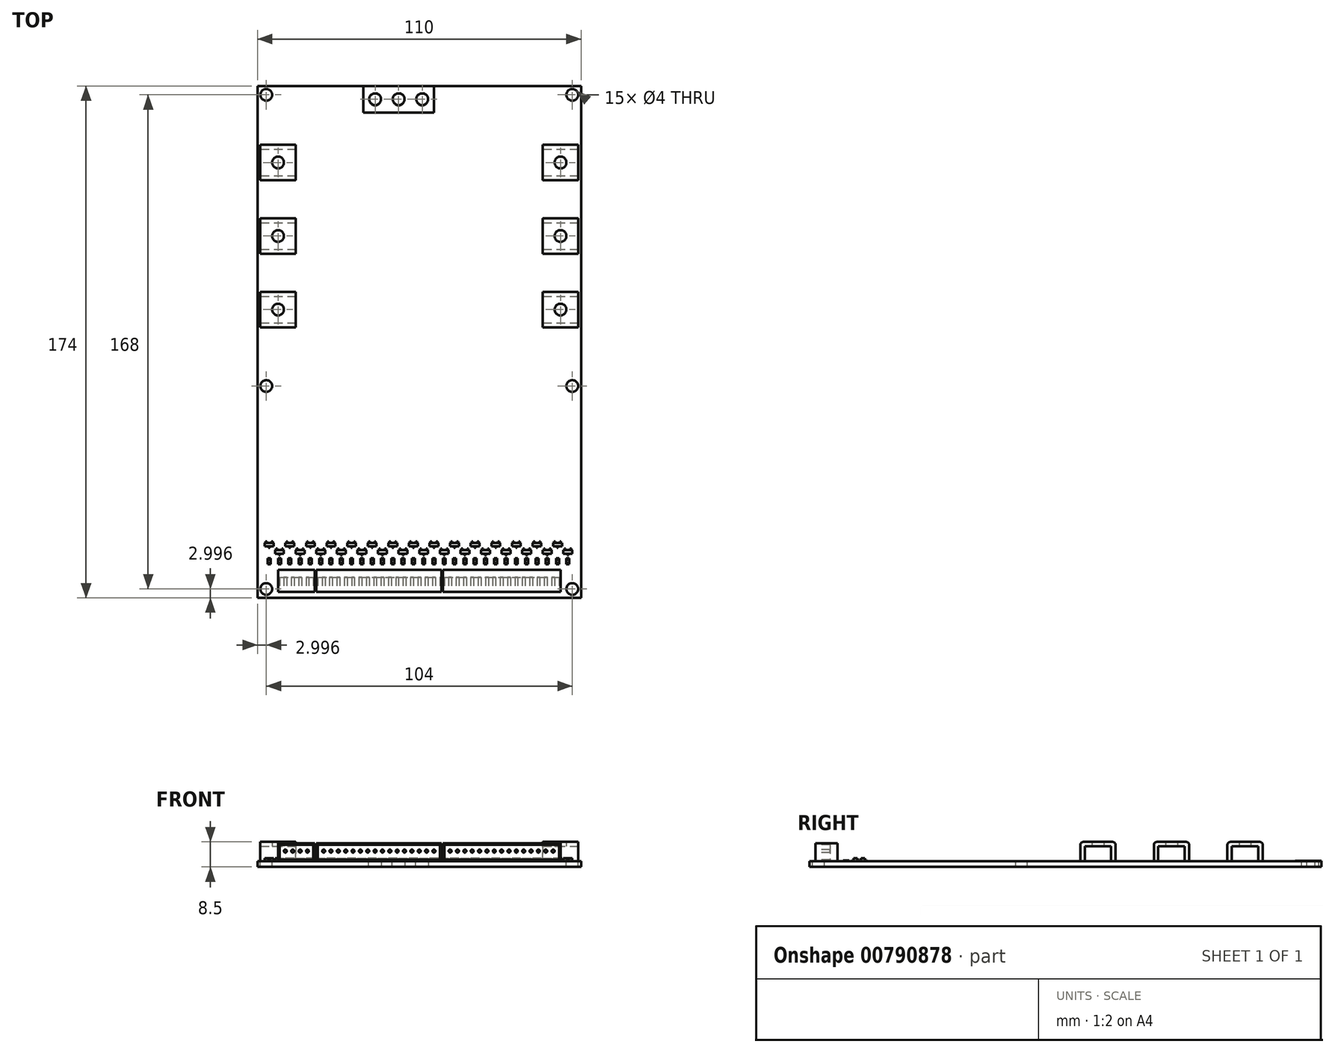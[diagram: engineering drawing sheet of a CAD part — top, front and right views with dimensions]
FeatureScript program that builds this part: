
annotation { "Feature Type Name" : "Feature", "Feature Type Description" : "" }
export const myFeature = defineFeature(function(context is Context, id is Id, definition is map)
    precondition{}
    {
        {
            var Q0;
            Q0=qCreatedBy(makeId("Top.planeOp"),FACE);
            var sketch = newSketch(context, id + "F0", { "sketchPlane" : qUnion([Q0])});
            skLineSegment(sketch, "E0.bottom", {"start": v(-29.84, -54.87) * mm, "end": v(80.16, -54.87) * mm});
            skLineSegment(sketch, "E0.top", {"start": v(-29.84, 119.13) * mm, "end": v(80.16, 119.13) * mm});
            skLineSegment(sketch, "E0.left", {"start": v(-29.84, -54.87) * mm, "end": v(-29.84, 119.13) * mm});
            skLineSegment(sketch, "E0.right", {"start": v(80.16, -54.87) * mm, "end": v(80.16, 119.13) * mm});
            skSolve(sketch);
        }
        {
            var Q0;
            Q0=makeQuery(id+"F0.imprint","IMPRINT",FACE,{"disambiguationData":[TD([[makeQuery(id+"F0.imprint","IMPRINT",EDGE,{"derivedFrom":sQuery(id+"F0.wireOp",EDGE,"E0.bottom")}),1.0]])]});
            extrude(context, id + "F1", {"entities" : qUnion([Q0]), "depth" : 2 * mm, "offsetDistance" : 25 * mm});
        }
        {
            var Q0;
            Q0=makeQuery(id+"F1.opExtrude","CAP_FACE",FACE,{"disambiguationData":[OSD([sQuery(id+"F0.wireOp",EDGE,"E0.bottom"),sQuery(id+"F0.wireOp",EDGE,"E0.top"),sQuery(id+"F0.wireOp",EDGE,"E0.left"),sQuery(id+"F0.wireOp",EDGE,"E0.right")])],"isStart":false});
            var sketch = newSketch(context, id + "F2", { "sketchPlane" : qUnion([Q0])});
            skPoint(sketch, "E1", {"position": v(77.16, 116.13) * mm});
            skPoint(sketch, "E2", {"position": v(-26.84, 116.13) * mm});
            skPoint(sketch, "E3", {"position": v(77.16, -51.87) * mm});
            skPoint(sketch, "E4", {"position": v(-26.84, -51.87) * mm});
            skPoint(sketch, "E5", {"position": v(77.16, 17.13) * mm});
            skPoint(sketch, "E6", {"position": v(-26.84, 17.13) * mm});
            skSolve(sketch);
        }
        {
            var Q0;
            Q0=sQuery(id+"F2.wireOp",VERTEX,"E1");
            var Q1;
            Q1=sQuery(id+"F2.wireOp",VERTEX,"E2");
            var Q2;
            Q2=sQuery(id+"F2.wireOp",VERTEX,"E6");
            var Q3;
            Q3=sQuery(id+"F2.wireOp",VERTEX,"E5");
            var Q4;
            Q4=sQuery(id+"F2.wireOp",VERTEX,"E3");
            var Q5;
            Q5=sQuery(id+"F2.wireOp",VERTEX,"E4");
            var Q6;
            Q6=makeQuery(id+"F1.opExtrude","SWEPT_BODY",BODY,{"disambiguationData":[OSD([sQuery(id+"F0.wireOp",EDGE,"E0.bottom"),sQuery(id+"F0.wireOp",EDGE,"E0.top"),sQuery(id+"F0.wireOp",EDGE,"E0.left"),sQuery(id+"F0.wireOp",EDGE,"E0.right")])]});
            hole(context, id + "F3", {"style" : HoleStyle.SIMPLE, "endStyle" : HoleEndStyle.THROUGH, "holeDiameter" : 4 * mm, "majorDiameter" : 5 * mm, "isTappedThrough" : true, "tappedDepth" : 12 * mm, "tapClearance" : 3, "locations" : qUnion([Q0, Q1, Q2, Q3, Q4, Q5]), "scope" : qUnion([Q6])});
        }
        {
            var Q0;
            Q0=makeQuery(id+"F1.opExtrude","CAP_FACE",FACE,{"disambiguationData":[OSD([sQuery(id+"F0.wireOp",EDGE,"E0.bottom"),sQuery(id+"F0.wireOp",EDGE,"E0.top"),sQuery(id+"F0.wireOp",EDGE,"E0.left"),sQuery(id+"F0.wireOp",EDGE,"E0.right")])],"isStart":false});
            var sketch = newSketch(context, id + "F4", { "sketchPlane" : qUnion([Q0])});
            skLineSegment(sketch, "E7.bottom", {"start": v(74.16, -38.67) * mm, "end": v(77.16, -38.67) * mm});
            skLineSegment(sketch, "E7.top", {"start": v(74.16, -39.87) * mm, "end": v(77.16, -39.87) * mm});
            skLineSegment(sketch, "E7.left", {"start": v(74.16, -38.67) * mm, "end": v(74.16, -39.87) * mm});
            skLineSegment(sketch, "E7.right", {"start": v(77.16, -38.67) * mm, "end": v(77.16, -39.87) * mm});
            skLineSegment(sketch, "E8.1.0.0", {"start": v(67.16, -39.87) * mm, "end": v(70.16, -39.87) * mm});
            skLineSegment(sketch, "E8.1.0.1", {"start": v(67.16, -38.67) * mm, "end": v(70.16, -38.67) * mm});
            skLineSegment(sketch, "E8.1.0.2", {"start": v(70.16, -38.67) * mm, "end": v(70.16, -39.87) * mm});
            skLineSegment(sketch, "E8.1.0.3", {"start": v(67.16, -38.67) * mm, "end": v(67.16, -39.87) * mm});
            skLineSegment(sketch, "E8.2.0.0", {"start": v(60.16, -39.87) * mm, "end": v(63.16, -39.87) * mm});
            skLineSegment(sketch, "E8.2.0.1", {"start": v(60.16, -38.67) * mm, "end": v(63.16, -38.67) * mm});
            skLineSegment(sketch, "E8.2.0.2", {"start": v(63.16, -38.67) * mm, "end": v(63.16, -39.87) * mm});
            skLineSegment(sketch, "E8.2.0.3", {"start": v(60.16, -38.67) * mm, "end": v(60.16, -39.87) * mm});
            skLineSegment(sketch, "E8.3.0.0", {"start": v(53.16, -39.87) * mm, "end": v(56.16, -39.87) * mm});
            skLineSegment(sketch, "E8.3.0.1", {"start": v(53.16, -38.67) * mm, "end": v(56.16, -38.67) * mm});
            skLineSegment(sketch, "E8.3.0.2", {"start": v(56.16, -38.67) * mm, "end": v(56.16, -39.87) * mm});
            skLineSegment(sketch, "E8.3.0.3", {"start": v(53.16, -38.67) * mm, "end": v(53.16, -39.87) * mm});
            skLineSegment(sketch, "E8.4.0.0", {"start": v(46.16, -39.87) * mm, "end": v(49.16, -39.87) * mm});
            skLineSegment(sketch, "E8.4.0.1", {"start": v(46.16, -38.67) * mm, "end": v(49.16, -38.67) * mm});
            skLineSegment(sketch, "E8.4.0.2", {"start": v(49.16, -38.67) * mm, "end": v(49.16, -39.87) * mm});
            skLineSegment(sketch, "E8.4.0.3", {"start": v(46.16, -38.67) * mm, "end": v(46.16, -39.87) * mm});
            skLineSegment(sketch, "E8.5.0.0", {"start": v(39.16, -39.87) * mm, "end": v(42.16, -39.87) * mm});
            skLineSegment(sketch, "E8.5.0.1", {"start": v(39.16, -38.67) * mm, "end": v(42.16, -38.67) * mm});
            skLineSegment(sketch, "E8.5.0.2", {"start": v(42.16, -38.67) * mm, "end": v(42.16, -39.87) * mm});
            skLineSegment(sketch, "E8.5.0.3", {"start": v(39.16, -38.67) * mm, "end": v(39.16, -39.87) * mm});
            skLineSegment(sketch, "E8.6.0.0", {"start": v(32.16, -39.87) * mm, "end": v(35.16, -39.87) * mm});
            skLineSegment(sketch, "E8.6.0.1", {"start": v(32.16, -38.67) * mm, "end": v(35.16, -38.67) * mm});
            skLineSegment(sketch, "E8.6.0.2", {"start": v(35.16, -38.67) * mm, "end": v(35.16, -39.87) * mm});
            skLineSegment(sketch, "E8.6.0.3", {"start": v(32.16, -38.67) * mm, "end": v(32.16, -39.87) * mm});
            skLineSegment(sketch, "E8.7.0.0", {"start": v(25.16, -39.87) * mm, "end": v(28.16, -39.87) * mm});
            skLineSegment(sketch, "E8.7.0.1", {"start": v(25.16, -38.67) * mm, "end": v(28.16, -38.67) * mm});
            skLineSegment(sketch, "E8.7.0.2", {"start": v(28.16, -38.67) * mm, "end": v(28.16, -39.87) * mm});
            skLineSegment(sketch, "E8.7.0.3", {"start": v(25.16, -38.67) * mm, "end": v(25.16, -39.87) * mm});
            skLineSegment(sketch, "E8.8.0.0", {"start": v(18.16, -39.87) * mm, "end": v(21.16, -39.87) * mm});
            skLineSegment(sketch, "E8.8.0.1", {"start": v(18.16, -38.67) * mm, "end": v(21.16, -38.67) * mm});
            skLineSegment(sketch, "E8.8.0.2", {"start": v(21.16, -38.67) * mm, "end": v(21.16, -39.87) * mm});
            skLineSegment(sketch, "E8.8.0.3", {"start": v(18.16, -38.67) * mm, "end": v(18.16, -39.87) * mm});
            skLineSegment(sketch, "E8.9.0.0", {"start": v(11.16, -39.87) * mm, "end": v(14.16, -39.87) * mm});
            skLineSegment(sketch, "E8.9.0.1", {"start": v(11.16, -38.67) * mm, "end": v(14.16, -38.67) * mm});
            skLineSegment(sketch, "E8.9.0.2", {"start": v(14.16, -38.67) * mm, "end": v(14.16, -39.87) * mm});
            skLineSegment(sketch, "E8.9.0.3", {"start": v(11.16, -38.67) * mm, "end": v(11.16, -39.87) * mm});
            skLineSegment(sketch, "E8.10.0.0", {"start": v(4.16, -39.87) * mm, "end": v(7.16, -39.87) * mm});
            skLineSegment(sketch, "E8.10.0.1", {"start": v(4.16, -38.67) * mm, "end": v(7.16, -38.67) * mm});
            skLineSegment(sketch, "E8.10.0.2", {"start": v(7.16, -38.67) * mm, "end": v(7.16, -39.87) * mm});
            skLineSegment(sketch, "E8.10.0.3", {"start": v(4.16, -38.67) * mm, "end": v(4.16, -39.87) * mm});
            skLineSegment(sketch, "E8.11.0.0", {"start": v(-2.84, -39.87) * mm, "end": v(0.16, -39.87) * mm});
            skLineSegment(sketch, "E8.11.0.1", {"start": v(-2.84, -38.67) * mm, "end": v(0.16, -38.67) * mm});
            skLineSegment(sketch, "E8.11.0.2", {"start": v(0.16, -38.67) * mm, "end": v(0.16, -39.87) * mm});
            skLineSegment(sketch, "E8.11.0.3", {"start": v(-2.84, -38.67) * mm, "end": v(-2.84, -39.87) * mm});
            skLineSegment(sketch, "E8.12.0.0", {"start": v(-9.84, -39.87) * mm, "end": v(-6.84, -39.87) * mm});
            skLineSegment(sketch, "E8.12.0.1", {"start": v(-9.84, -38.67) * mm, "end": v(-6.84, -38.67) * mm});
            skLineSegment(sketch, "E8.12.0.2", {"start": v(-6.84, -38.67) * mm, "end": v(-6.84, -39.87) * mm});
            skLineSegment(sketch, "E8.12.0.3", {"start": v(-9.84, -38.67) * mm, "end": v(-9.84, -39.87) * mm});
            skLineSegment(sketch, "E8.13.0.0", {"start": v(-16.84, -39.87) * mm, "end": v(-13.84, -39.87) * mm});
            skLineSegment(sketch, "E8.13.0.1", {"start": v(-16.84, -38.67) * mm, "end": v(-13.84, -38.67) * mm});
            skLineSegment(sketch, "E8.13.0.2", {"start": v(-13.84, -38.67) * mm, "end": v(-13.84, -39.87) * mm});
            skLineSegment(sketch, "E8.13.0.3", {"start": v(-16.84, -38.67) * mm, "end": v(-16.84, -39.87) * mm});
            skLineSegment(sketch, "E8.14.0.0", {"start": v(-23.84, -39.87) * mm, "end": v(-20.84, -39.87) * mm});
            skLineSegment(sketch, "E8.14.0.1", {"start": v(-23.84, -38.67) * mm, "end": v(-20.84, -38.67) * mm});
            skLineSegment(sketch, "E8.14.0.2", {"start": v(-20.84, -38.67) * mm, "end": v(-20.84, -39.87) * mm});
            skLineSegment(sketch, "E8.14.0.3", {"start": v(-23.84, -38.67) * mm, "end": v(-23.84, -39.87) * mm});
            skLineSegment(sketch, "E8.direction1", {"start": v(74.16, -39.87) * mm, "end": v(67.16, -39.87) * mm, "construction": true});
            skLineSegment(sketch, "E9.bottom", {"start": v(73.66, -36.17) * mm, "end": v(70.66, -36.17) * mm});
            skLineSegment(sketch, "E9.top", {"start": v(73.66, -37.37) * mm, "end": v(70.66, -37.37) * mm});
            skLineSegment(sketch, "E9.left", {"start": v(73.66, -36.17) * mm, "end": v(73.66, -37.37) * mm});
            skLineSegment(sketch, "E9.right", {"start": v(70.66, -36.17) * mm, "end": v(70.66, -37.37) * mm});
            skLineSegment(sketch, "E10.1.0.0", {"start": v(66.66, -36.17) * mm, "end": v(63.66, -36.17) * mm});
            skLineSegment(sketch, "E10.1.0.1", {"start": v(66.66, -37.37) * mm, "end": v(63.66, -37.37) * mm});
            skLineSegment(sketch, "E10.1.0.2", {"start": v(66.66, -36.17) * mm, "end": v(66.66, -37.37) * mm});
            skLineSegment(sketch, "E10.1.0.3", {"start": v(63.66, -36.17) * mm, "end": v(63.66, -37.37) * mm});
            skLineSegment(sketch, "E10.2.0.0", {"start": v(59.66, -36.17) * mm, "end": v(56.66, -36.17) * mm});
            skLineSegment(sketch, "E10.2.0.1", {"start": v(59.66, -37.37) * mm, "end": v(56.66, -37.37) * mm});
            skLineSegment(sketch, "E10.2.0.2", {"start": v(59.66, -36.17) * mm, "end": v(59.66, -37.37) * mm});
            skLineSegment(sketch, "E10.2.0.3", {"start": v(56.66, -36.17) * mm, "end": v(56.66, -37.37) * mm});
            skLineSegment(sketch, "E10.3.0.0", {"start": v(52.66, -36.17) * mm, "end": v(49.66, -36.17) * mm});
            skLineSegment(sketch, "E10.3.0.1", {"start": v(52.66, -37.37) * mm, "end": v(49.66, -37.37) * mm});
            skLineSegment(sketch, "E10.3.0.2", {"start": v(52.66, -36.17) * mm, "end": v(52.66, -37.37) * mm});
            skLineSegment(sketch, "E10.3.0.3", {"start": v(49.66, -36.17) * mm, "end": v(49.66, -37.37) * mm});
            skLineSegment(sketch, "E10.4.0.0", {"start": v(45.66, -36.17) * mm, "end": v(42.66, -36.17) * mm});
            skLineSegment(sketch, "E10.4.0.1", {"start": v(45.66, -37.37) * mm, "end": v(42.66, -37.37) * mm});
            skLineSegment(sketch, "E10.4.0.2", {"start": v(45.66, -36.17) * mm, "end": v(45.66, -37.37) * mm});
            skLineSegment(sketch, "E10.4.0.3", {"start": v(42.66, -36.17) * mm, "end": v(42.66, -37.37) * mm});
            skLineSegment(sketch, "E10.5.0.0", {"start": v(38.66, -36.17) * mm, "end": v(35.66, -36.17) * mm});
            skLineSegment(sketch, "E10.5.0.1", {"start": v(38.66, -37.37) * mm, "end": v(35.66, -37.37) * mm});
            skLineSegment(sketch, "E10.5.0.2", {"start": v(38.66, -36.17) * mm, "end": v(38.66, -37.37) * mm});
            skLineSegment(sketch, "E10.5.0.3", {"start": v(35.66, -36.17) * mm, "end": v(35.66, -37.37) * mm});
            skLineSegment(sketch, "E10.6.0.0", {"start": v(31.66, -36.17) * mm, "end": v(28.66, -36.17) * mm});
            skLineSegment(sketch, "E10.6.0.1", {"start": v(31.66, -37.37) * mm, "end": v(28.66, -37.37) * mm});
            skLineSegment(sketch, "E10.6.0.2", {"start": v(31.66, -36.17) * mm, "end": v(31.66, -37.37) * mm});
            skLineSegment(sketch, "E10.6.0.3", {"start": v(28.66, -36.17) * mm, "end": v(28.66, -37.37) * mm});
            skLineSegment(sketch, "E10.7.0.0", {"start": v(24.66, -36.17) * mm, "end": v(21.66, -36.17) * mm});
            skLineSegment(sketch, "E10.7.0.1", {"start": v(24.66, -37.37) * mm, "end": v(21.66, -37.37) * mm});
            skLineSegment(sketch, "E10.7.0.2", {"start": v(24.66, -36.17) * mm, "end": v(24.66, -37.37) * mm});
            skLineSegment(sketch, "E10.7.0.3", {"start": v(21.66, -36.17) * mm, "end": v(21.66, -37.37) * mm});
            skLineSegment(sketch, "E10.8.0.0", {"start": v(17.66, -36.17) * mm, "end": v(14.66, -36.17) * mm});
            skLineSegment(sketch, "E10.8.0.1", {"start": v(17.66, -37.37) * mm, "end": v(14.66, -37.37) * mm});
            skLineSegment(sketch, "E10.8.0.2", {"start": v(17.66, -36.17) * mm, "end": v(17.66, -37.37) * mm});
            skLineSegment(sketch, "E10.8.0.3", {"start": v(14.66, -36.17) * mm, "end": v(14.66, -37.37) * mm});
            skLineSegment(sketch, "E10.9.0.0", {"start": v(10.66, -36.17) * mm, "end": v(7.66, -36.17) * mm});
            skLineSegment(sketch, "E10.9.0.1", {"start": v(10.66, -37.37) * mm, "end": v(7.66, -37.37) * mm});
            skLineSegment(sketch, "E10.9.0.2", {"start": v(10.66, -36.17) * mm, "end": v(10.66, -37.37) * mm});
            skLineSegment(sketch, "E10.9.0.3", {"start": v(7.66, -36.17) * mm, "end": v(7.66, -37.37) * mm});
            skLineSegment(sketch, "E10.10.0.0", {"start": v(3.66, -36.17) * mm, "end": v(0.66, -36.17) * mm});
            skLineSegment(sketch, "E10.10.0.1", {"start": v(3.66, -37.37) * mm, "end": v(0.66, -37.37) * mm});
            skLineSegment(sketch, "E10.10.0.2", {"start": v(3.66, -36.17) * mm, "end": v(3.66, -37.37) * mm});
            skLineSegment(sketch, "E10.10.0.3", {"start": v(0.66, -36.17) * mm, "end": v(0.66, -37.37) * mm});
            skLineSegment(sketch, "E10.11.0.0", {"start": v(-3.34, -36.17) * mm, "end": v(-6.34, -36.17) * mm});
            skLineSegment(sketch, "E10.11.0.1", {"start": v(-3.34, -37.37) * mm, "end": v(-6.34, -37.37) * mm});
            skLineSegment(sketch, "E10.11.0.2", {"start": v(-3.34, -36.17) * mm, "end": v(-3.34, -37.37) * mm});
            skLineSegment(sketch, "E10.11.0.3", {"start": v(-6.34, -36.17) * mm, "end": v(-6.34, -37.37) * mm});
            skLineSegment(sketch, "E10.12.0.0", {"start": v(-10.34, -36.17) * mm, "end": v(-13.34, -36.17) * mm});
            skLineSegment(sketch, "E10.12.0.1", {"start": v(-10.34, -37.37) * mm, "end": v(-13.34, -37.37) * mm});
            skLineSegment(sketch, "E10.12.0.2", {"start": v(-10.34, -36.17) * mm, "end": v(-10.34, -37.37) * mm});
            skLineSegment(sketch, "E10.12.0.3", {"start": v(-13.34, -36.17) * mm, "end": v(-13.34, -37.37) * mm});
            skLineSegment(sketch, "E10.13.0.0", {"start": v(-17.34, -36.17) * mm, "end": v(-20.34, -36.17) * mm});
            skLineSegment(sketch, "E10.13.0.1", {"start": v(-17.34, -37.37) * mm, "end": v(-20.34, -37.37) * mm});
            skLineSegment(sketch, "E10.13.0.2", {"start": v(-17.34, -36.17) * mm, "end": v(-17.34, -37.37) * mm});
            skLineSegment(sketch, "E10.13.0.3", {"start": v(-20.34, -36.17) * mm, "end": v(-20.34, -37.37) * mm});
            skLineSegment(sketch, "E10.14.0.0", {"start": v(-24.34, -36.17) * mm, "end": v(-27.34, -36.17) * mm});
            skLineSegment(sketch, "E10.14.0.1", {"start": v(-24.34, -37.37) * mm, "end": v(-27.34, -37.37) * mm});
            skLineSegment(sketch, "E10.14.0.2", {"start": v(-24.34, -36.17) * mm, "end": v(-24.34, -37.37) * mm});
            skLineSegment(sketch, "E10.14.0.3", {"start": v(-27.34, -36.17) * mm, "end": v(-27.34, -37.37) * mm});
            skLineSegment(sketch, "E10.direction1", {"start": v(70.66, -37.37) * mm, "end": v(63.66, -37.37) * mm, "construction": true});
            skLineSegment(sketch, "E11.bottom", {"start": v(75.16, -41.87) * mm, "end": v(76.16, -41.87) * mm});
            skLineSegment(sketch, "E11.top", {"start": v(75.16, -43.07) * mm, "end": v(76.16, -43.07) * mm});
            skLineSegment(sketch, "E11.left", {"start": v(75.16, -41.87) * mm, "end": v(75.16, -43.07) * mm});
            skLineSegment(sketch, "E11.right", {"start": v(76.16, -41.87) * mm, "end": v(76.16, -43.07) * mm});
            skLineSegment(sketch, "E12.1.0.0", {"start": v(71.66, -43.07) * mm, "end": v(72.66, -43.07) * mm});
            skLineSegment(sketch, "E12.1.0.1", {"start": v(71.66, -41.87) * mm, "end": v(71.66, -43.07) * mm});
            skLineSegment(sketch, "E12.1.0.2", {"start": v(72.66, -41.87) * mm, "end": v(72.66, -43.07) * mm});
            skLineSegment(sketch, "E12.1.0.3", {"start": v(71.66, -41.87) * mm, "end": v(72.66, -41.87) * mm});
            skLineSegment(sketch, "E12.2.0.0", {"start": v(68.16, -43.07) * mm, "end": v(69.16, -43.07) * mm});
            skLineSegment(sketch, "E12.2.0.1", {"start": v(68.16, -41.87) * mm, "end": v(68.16, -43.07) * mm});
            skLineSegment(sketch, "E12.2.0.2", {"start": v(69.16, -41.87) * mm, "end": v(69.16, -43.07) * mm});
            skLineSegment(sketch, "E12.2.0.3", {"start": v(68.16, -41.87) * mm, "end": v(69.16, -41.87) * mm});
            skLineSegment(sketch, "E12.3.0.0", {"start": v(64.66, -43.07) * mm, "end": v(65.66, -43.07) * mm});
            skLineSegment(sketch, "E12.3.0.1", {"start": v(64.66, -41.87) * mm, "end": v(64.66, -43.07) * mm});
            skLineSegment(sketch, "E12.3.0.2", {"start": v(65.66, -41.87) * mm, "end": v(65.66, -43.07) * mm});
            skLineSegment(sketch, "E12.3.0.3", {"start": v(64.66, -41.87) * mm, "end": v(65.66, -41.87) * mm});
            skLineSegment(sketch, "E12.4.0.0", {"start": v(61.16, -43.07) * mm, "end": v(62.16, -43.07) * mm});
            skLineSegment(sketch, "E12.4.0.1", {"start": v(61.16, -41.87) * mm, "end": v(61.16, -43.07) * mm});
            skLineSegment(sketch, "E12.4.0.2", {"start": v(62.16, -41.87) * mm, "end": v(62.16, -43.07) * mm});
            skLineSegment(sketch, "E12.4.0.3", {"start": v(61.16, -41.87) * mm, "end": v(62.16, -41.87) * mm});
            skLineSegment(sketch, "E12.5.0.0", {"start": v(57.66, -43.07) * mm, "end": v(58.66, -43.07) * mm});
            skLineSegment(sketch, "E12.5.0.1", {"start": v(57.66, -41.87) * mm, "end": v(57.66, -43.07) * mm});
            skLineSegment(sketch, "E12.5.0.2", {"start": v(58.66, -41.87) * mm, "end": v(58.66, -43.07) * mm});
            skLineSegment(sketch, "E12.5.0.3", {"start": v(57.66, -41.87) * mm, "end": v(58.66, -41.87) * mm});
            skLineSegment(sketch, "E12.6.0.0", {"start": v(54.16, -43.07) * mm, "end": v(55.16, -43.07) * mm});
            skLineSegment(sketch, "E12.6.0.1", {"start": v(54.16, -41.87) * mm, "end": v(54.16, -43.07) * mm});
            skLineSegment(sketch, "E12.6.0.2", {"start": v(55.16, -41.87) * mm, "end": v(55.16, -43.07) * mm});
            skLineSegment(sketch, "E12.6.0.3", {"start": v(54.16, -41.87) * mm, "end": v(55.16, -41.87) * mm});
            skLineSegment(sketch, "E12.7.0.0", {"start": v(50.66, -43.07) * mm, "end": v(51.66, -43.07) * mm});
            skLineSegment(sketch, "E12.7.0.1", {"start": v(50.66, -41.87) * mm, "end": v(50.66, -43.07) * mm});
            skLineSegment(sketch, "E12.7.0.2", {"start": v(51.66, -41.87) * mm, "end": v(51.66, -43.07) * mm});
            skLineSegment(sketch, "E12.7.0.3", {"start": v(50.66, -41.87) * mm, "end": v(51.66, -41.87) * mm});
            skLineSegment(sketch, "E12.8.0.0", {"start": v(47.16, -43.07) * mm, "end": v(48.16, -43.07) * mm});
            skLineSegment(sketch, "E12.8.0.1", {"start": v(47.16, -41.87) * mm, "end": v(47.16, -43.07) * mm});
            skLineSegment(sketch, "E12.8.0.2", {"start": v(48.16, -41.87) * mm, "end": v(48.16, -43.07) * mm});
            skLineSegment(sketch, "E12.8.0.3", {"start": v(47.16, -41.87) * mm, "end": v(48.16, -41.87) * mm});
            skLineSegment(sketch, "E12.9.0.0", {"start": v(43.66, -43.07) * mm, "end": v(44.66, -43.07) * mm});
            skLineSegment(sketch, "E12.9.0.1", {"start": v(43.66, -41.87) * mm, "end": v(43.66, -43.07) * mm});
            skLineSegment(sketch, "E12.9.0.2", {"start": v(44.66, -41.87) * mm, "end": v(44.66, -43.07) * mm});
            skLineSegment(sketch, "E12.9.0.3", {"start": v(43.66, -41.87) * mm, "end": v(44.66, -41.87) * mm});
            skLineSegment(sketch, "E12.10.0.0", {"start": v(40.16, -43.07) * mm, "end": v(41.16, -43.07) * mm});
            skLineSegment(sketch, "E12.10.0.1", {"start": v(40.16, -41.87) * mm, "end": v(40.16, -43.07) * mm});
            skLineSegment(sketch, "E12.10.0.2", {"start": v(41.16, -41.87) * mm, "end": v(41.16, -43.07) * mm});
            skLineSegment(sketch, "E12.10.0.3", {"start": v(40.16, -41.87) * mm, "end": v(41.16, -41.87) * mm});
            skLineSegment(sketch, "E12.11.0.0", {"start": v(36.66, -43.07) * mm, "end": v(37.66, -43.07) * mm});
            skLineSegment(sketch, "E12.11.0.1", {"start": v(36.66, -41.87) * mm, "end": v(36.66, -43.07) * mm});
            skLineSegment(sketch, "E12.11.0.2", {"start": v(37.66, -41.87) * mm, "end": v(37.66, -43.07) * mm});
            skLineSegment(sketch, "E12.11.0.3", {"start": v(36.66, -41.87) * mm, "end": v(37.66, -41.87) * mm});
            skLineSegment(sketch, "E12.12.0.0", {"start": v(33.16, -43.07) * mm, "end": v(34.16, -43.07) * mm});
            skLineSegment(sketch, "E12.12.0.1", {"start": v(33.16, -41.87) * mm, "end": v(33.16, -43.07) * mm});
            skLineSegment(sketch, "E12.12.0.2", {"start": v(34.16, -41.87) * mm, "end": v(34.16, -43.07) * mm});
            skLineSegment(sketch, "E12.12.0.3", {"start": v(33.16, -41.87) * mm, "end": v(34.16, -41.87) * mm});
            skLineSegment(sketch, "E12.13.0.0", {"start": v(29.66, -43.07) * mm, "end": v(30.66, -43.07) * mm});
            skLineSegment(sketch, "E12.13.0.1", {"start": v(29.66, -41.87) * mm, "end": v(29.66, -43.07) * mm});
            skLineSegment(sketch, "E12.13.0.2", {"start": v(30.66, -41.87) * mm, "end": v(30.66, -43.07) * mm});
            skLineSegment(sketch, "E12.13.0.3", {"start": v(29.66, -41.87) * mm, "end": v(30.66, -41.87) * mm});
            skLineSegment(sketch, "E12.14.0.0", {"start": v(26.16, -43.07) * mm, "end": v(27.16, -43.07) * mm});
            skLineSegment(sketch, "E12.14.0.1", {"start": v(26.16, -41.87) * mm, "end": v(26.16, -43.07) * mm});
            skLineSegment(sketch, "E12.14.0.2", {"start": v(27.16, -41.87) * mm, "end": v(27.16, -43.07) * mm});
            skLineSegment(sketch, "E12.14.0.3", {"start": v(26.16, -41.87) * mm, "end": v(27.16, -41.87) * mm});
            skLineSegment(sketch, "E12.15.0.0", {"start": v(22.66, -43.07) * mm, "end": v(23.66, -43.07) * mm});
            skLineSegment(sketch, "E12.15.0.1", {"start": v(22.66, -41.87) * mm, "end": v(22.66, -43.07) * mm});
            skLineSegment(sketch, "E12.15.0.2", {"start": v(23.66, -41.87) * mm, "end": v(23.66, -43.07) * mm});
            skLineSegment(sketch, "E12.15.0.3", {"start": v(22.66, -41.87) * mm, "end": v(23.66, -41.87) * mm});
            skLineSegment(sketch, "E12.16.0.0", {"start": v(19.16, -43.07) * mm, "end": v(20.16, -43.07) * mm});
            skLineSegment(sketch, "E12.16.0.1", {"start": v(19.16, -41.87) * mm, "end": v(19.16, -43.07) * mm});
            skLineSegment(sketch, "E12.16.0.2", {"start": v(20.16, -41.87) * mm, "end": v(20.16, -43.07) * mm});
            skLineSegment(sketch, "E12.16.0.3", {"start": v(19.16, -41.87) * mm, "end": v(20.16, -41.87) * mm});
            skLineSegment(sketch, "E12.17.0.0", {"start": v(15.66, -43.07) * mm, "end": v(16.66, -43.07) * mm});
            skLineSegment(sketch, "E12.17.0.1", {"start": v(15.66, -41.87) * mm, "end": v(15.66, -43.07) * mm});
            skLineSegment(sketch, "E12.17.0.2", {"start": v(16.66, -41.87) * mm, "end": v(16.66, -43.07) * mm});
            skLineSegment(sketch, "E12.17.0.3", {"start": v(15.66, -41.87) * mm, "end": v(16.66, -41.87) * mm});
            skLineSegment(sketch, "E12.18.0.0", {"start": v(12.16, -43.07) * mm, "end": v(13.16, -43.07) * mm});
            skLineSegment(sketch, "E12.18.0.1", {"start": v(12.16, -41.87) * mm, "end": v(12.16, -43.07) * mm});
            skLineSegment(sketch, "E12.18.0.2", {"start": v(13.16, -41.87) * mm, "end": v(13.16, -43.07) * mm});
            skLineSegment(sketch, "E12.18.0.3", {"start": v(12.16, -41.87) * mm, "end": v(13.16, -41.87) * mm});
            skLineSegment(sketch, "E12.19.0.0", {"start": v(8.66, -43.07) * mm, "end": v(9.66, -43.07) * mm});
            skLineSegment(sketch, "E12.19.0.1", {"start": v(8.66, -41.87) * mm, "end": v(8.66, -43.07) * mm});
            skLineSegment(sketch, "E12.19.0.2", {"start": v(9.66, -41.87) * mm, "end": v(9.66, -43.07) * mm});
            skLineSegment(sketch, "E12.19.0.3", {"start": v(8.66, -41.87) * mm, "end": v(9.66, -41.87) * mm});
            skLineSegment(sketch, "E12.20.0.0", {"start": v(5.16, -43.07) * mm, "end": v(6.16, -43.07) * mm});
            skLineSegment(sketch, "E12.20.0.1", {"start": v(5.16, -41.87) * mm, "end": v(5.16, -43.07) * mm});
            skLineSegment(sketch, "E12.20.0.2", {"start": v(6.16, -41.87) * mm, "end": v(6.16, -43.07) * mm});
            skLineSegment(sketch, "E12.20.0.3", {"start": v(5.16, -41.87) * mm, "end": v(6.16, -41.87) * mm});
            skLineSegment(sketch, "E12.21.0.0", {"start": v(1.66, -43.07) * mm, "end": v(2.66, -43.07) * mm});
            skLineSegment(sketch, "E12.21.0.1", {"start": v(1.66, -41.87) * mm, "end": v(1.66, -43.07) * mm});
            skLineSegment(sketch, "E12.21.0.2", {"start": v(2.66, -41.87) * mm, "end": v(2.66, -43.07) * mm});
            skLineSegment(sketch, "E12.21.0.3", {"start": v(1.66, -41.87) * mm, "end": v(2.66, -41.87) * mm});
            skLineSegment(sketch, "E12.22.0.0", {"start": v(-1.84, -43.07) * mm, "end": v(-0.84, -43.07) * mm});
            skLineSegment(sketch, "E12.22.0.1", {"start": v(-1.84, -41.87) * mm, "end": v(-1.84, -43.07) * mm});
            skLineSegment(sketch, "E12.22.0.2", {"start": v(-0.84, -41.87) * mm, "end": v(-0.84, -43.07) * mm});
            skLineSegment(sketch, "E12.22.0.3", {"start": v(-1.84, -41.87) * mm, "end": v(-0.84, -41.87) * mm});
            skLineSegment(sketch, "E12.23.0.0", {"start": v(-5.34, -43.07) * mm, "end": v(-4.34, -43.07) * mm});
            skLineSegment(sketch, "E12.23.0.1", {"start": v(-5.34, -41.87) * mm, "end": v(-5.34, -43.07) * mm});
            skLineSegment(sketch, "E12.23.0.2", {"start": v(-4.34, -41.87) * mm, "end": v(-4.34, -43.07) * mm});
            skLineSegment(sketch, "E12.23.0.3", {"start": v(-5.34, -41.87) * mm, "end": v(-4.34, -41.87) * mm});
            skLineSegment(sketch, "E12.24.0.0", {"start": v(-8.84, -43.07) * mm, "end": v(-7.84, -43.07) * mm});
            skLineSegment(sketch, "E12.24.0.1", {"start": v(-8.84, -41.87) * mm, "end": v(-8.84, -43.07) * mm});
            skLineSegment(sketch, "E12.24.0.2", {"start": v(-7.84, -41.87) * mm, "end": v(-7.84, -43.07) * mm});
            skLineSegment(sketch, "E12.24.0.3", {"start": v(-8.84, -41.87) * mm, "end": v(-7.84, -41.87) * mm});
            skLineSegment(sketch, "E12.25.0.0", {"start": v(-12.34, -43.07) * mm, "end": v(-11.34, -43.07) * mm});
            skLineSegment(sketch, "E12.25.0.1", {"start": v(-12.34, -41.87) * mm, "end": v(-12.34, -43.07) * mm});
            skLineSegment(sketch, "E12.25.0.2", {"start": v(-11.34, -41.87) * mm, "end": v(-11.34, -43.07) * mm});
            skLineSegment(sketch, "E12.25.0.3", {"start": v(-12.34, -41.87) * mm, "end": v(-11.34, -41.87) * mm});
            skLineSegment(sketch, "E12.26.0.0", {"start": v(-15.84, -43.07) * mm, "end": v(-14.84, -43.07) * mm});
            skLineSegment(sketch, "E12.26.0.1", {"start": v(-15.84, -41.87) * mm, "end": v(-15.84, -43.07) * mm});
            skLineSegment(sketch, "E12.26.0.2", {"start": v(-14.84, -41.87) * mm, "end": v(-14.84, -43.07) * mm});
            skLineSegment(sketch, "E12.26.0.3", {"start": v(-15.84, -41.87) * mm, "end": v(-14.84, -41.87) * mm});
            skLineSegment(sketch, "E12.27.0.0", {"start": v(-19.34, -43.07) * mm, "end": v(-18.34, -43.07) * mm});
            skLineSegment(sketch, "E12.27.0.1", {"start": v(-19.34, -41.87) * mm, "end": v(-19.34, -43.07) * mm});
            skLineSegment(sketch, "E12.27.0.2", {"start": v(-18.34, -41.87) * mm, "end": v(-18.34, -43.07) * mm});
            skLineSegment(sketch, "E12.27.0.3", {"start": v(-19.34, -41.87) * mm, "end": v(-18.34, -41.87) * mm});
            skLineSegment(sketch, "E12.28.0.0", {"start": v(-22.84, -43.07) * mm, "end": v(-21.84, -43.07) * mm});
            skLineSegment(sketch, "E12.28.0.1", {"start": v(-22.84, -41.87) * mm, "end": v(-22.84, -43.07) * mm});
            skLineSegment(sketch, "E12.28.0.2", {"start": v(-21.84, -41.87) * mm, "end": v(-21.84, -43.07) * mm});
            skLineSegment(sketch, "E12.28.0.3", {"start": v(-22.84, -41.87) * mm, "end": v(-21.84, -41.87) * mm});
            skLineSegment(sketch, "E12.29.0.0", {"start": v(-26.34, -43.07) * mm, "end": v(-25.34, -43.07) * mm});
            skLineSegment(sketch, "E12.29.0.1", {"start": v(-26.34, -41.87) * mm, "end": v(-26.34, -43.07) * mm});
            skLineSegment(sketch, "E12.29.0.2", {"start": v(-25.34, -41.87) * mm, "end": v(-25.34, -43.07) * mm});
            skLineSegment(sketch, "E12.29.0.3", {"start": v(-26.34, -41.87) * mm, "end": v(-25.34, -41.87) * mm});
            skLineSegment(sketch, "E12.direction1", {"start": v(75.16, -43.07) * mm, "end": v(71.66, -43.07) * mm, "construction": true});
            skSolve(sketch);
        }
        {
            var Q0;
            Q0=makeQuery(id+"F4.imprint","IMPRINT",FACE,{"disambiguationData":[TD([[makeQuery(id+"F4.imprint","IMPRINT",EDGE,{"derivedFrom":sQuery(id+"F4.wireOp",EDGE,"E8.5.0.0")}),1.0]])]});
            var Q1;
            Q1=makeQuery(id+"F4.imprint","IMPRINT",FACE,{"disambiguationData":[TD([[makeQuery(id+"F4.imprint","IMPRINT",EDGE,{"derivedFrom":sQuery(id+"F4.wireOp",EDGE,"E7.bottom")}),-1.0]])]});
            var Q2;
            Q2=makeQuery(id+"F4.imprint","IMPRINT",FACE,{"disambiguationData":[TD([[makeQuery(id+"F4.imprint","IMPRINT",EDGE,{"derivedFrom":sQuery(id+"F4.wireOp",EDGE,"E10.9.0.0")}),1.0]])]});
            var Q3;
            Q3=makeQuery(id+"F4.imprint","IMPRINT",FACE,{"disambiguationData":[TD([[makeQuery(id+"F4.imprint","IMPRINT",EDGE,{"derivedFrom":sQuery(id+"F4.wireOp",EDGE,"E10.12.0.0")}),1.0]])]});
            var Q4;
            Q4=makeQuery(id+"F4.imprint","IMPRINT",FACE,{"disambiguationData":[TD([[makeQuery(id+"F4.imprint","IMPRINT",EDGE,{"derivedFrom":sQuery(id+"F4.wireOp",EDGE,"E10.7.0.0")}),1.0]])]});
            var Q5;
            Q5=makeQuery(id+"F4.imprint","IMPRINT",FACE,{"disambiguationData":[TD([[makeQuery(id+"F4.imprint","IMPRINT",EDGE,{"derivedFrom":sQuery(id+"F4.wireOp",EDGE,"E10.13.0.0")}),1.0]])]});
            var Q6;
            Q6=makeQuery(id+"F4.imprint","IMPRINT",FACE,{"disambiguationData":[TD([[makeQuery(id+"F4.imprint","IMPRINT",EDGE,{"derivedFrom":sQuery(id+"F4.wireOp",EDGE,"E8.11.0.0")}),1.0]])]});
            var Q7;
            Q7=makeQuery(id+"F4.imprint","IMPRINT",FACE,{"disambiguationData":[TD([[makeQuery(id+"F4.imprint","IMPRINT",EDGE,{"derivedFrom":sQuery(id+"F4.wireOp",EDGE,"E8.9.0.0")}),1.0]])]});
            var Q8;
            Q8=makeQuery(id+"F4.imprint","IMPRINT",FACE,{"disambiguationData":[TD([[makeQuery(id+"F4.imprint","IMPRINT",EDGE,{"derivedFrom":sQuery(id+"F4.wireOp",EDGE,"E10.3.0.0")}),1.0]])]});
            var Q9;
            Q9=makeQuery(id+"F4.imprint","IMPRINT",FACE,{"disambiguationData":[TD([[makeQuery(id+"F4.imprint","IMPRINT",EDGE,{"derivedFrom":sQuery(id+"F4.wireOp",EDGE,"E9.bottom")}),1.0]])]});
            var Q10;
            Q10=makeQuery(id+"F4.imprint","IMPRINT",FACE,{"disambiguationData":[TD([[makeQuery(id+"F4.imprint","IMPRINT",EDGE,{"derivedFrom":sQuery(id+"F4.wireOp",EDGE,"E8.13.0.0")}),1.0]])]});
            var Q11;
            Q11=makeQuery(id+"F4.imprint","IMPRINT",FACE,{"disambiguationData":[TD([[makeQuery(id+"F4.imprint","IMPRINT",EDGE,{"derivedFrom":sQuery(id+"F4.wireOp",EDGE,"E8.3.0.0")}),1.0]])]});
            var Q12;
            Q12=makeQuery(id+"F4.imprint","IMPRINT",FACE,{"disambiguationData":[TD([[makeQuery(id+"F4.imprint","IMPRINT",EDGE,{"derivedFrom":sQuery(id+"F4.wireOp",EDGE,"E8.1.0.0")}),1.0]])]});
            var Q13;
            Q13=makeQuery(id+"F4.imprint","IMPRINT",FACE,{"disambiguationData":[TD([[makeQuery(id+"F4.imprint","IMPRINT",EDGE,{"derivedFrom":sQuery(id+"F4.wireOp",EDGE,"E8.7.0.0")}),1.0]])]});
            var Q14;
            Q14=makeQuery(id+"F4.imprint","IMPRINT",FACE,{"disambiguationData":[TD([[makeQuery(id+"F4.imprint","IMPRINT",EDGE,{"derivedFrom":sQuery(id+"F4.wireOp",EDGE,"E10.4.0.0")}),1.0]])]});
            var Q15;
            Q15=makeQuery(id+"F4.imprint","IMPRINT",FACE,{"disambiguationData":[TD([[makeQuery(id+"F4.imprint","IMPRINT",EDGE,{"derivedFrom":sQuery(id+"F4.wireOp",EDGE,"E10.5.0.0")}),1.0]])]});
            var Q16;
            Q16=makeQuery(id+"F4.imprint","IMPRINT",FACE,{"disambiguationData":[TD([[makeQuery(id+"F4.imprint","IMPRINT",EDGE,{"derivedFrom":sQuery(id+"F4.wireOp",EDGE,"E8.14.0.0")}),1.0]])]});
            var Q17;
            Q17=makeQuery(id+"F4.imprint","IMPRINT",FACE,{"disambiguationData":[TD([[makeQuery(id+"F4.imprint","IMPRINT",EDGE,{"derivedFrom":sQuery(id+"F4.wireOp",EDGE,"E8.10.0.0")}),1.0]])]});
            var Q18;
            Q18=makeQuery(id+"F4.imprint","IMPRINT",FACE,{"disambiguationData":[TD([[makeQuery(id+"F4.imprint","IMPRINT",EDGE,{"derivedFrom":sQuery(id+"F4.wireOp",EDGE,"E10.8.0.0")}),1.0]])]});
            var Q19;
            Q19=makeQuery(id+"F4.imprint","IMPRINT",FACE,{"disambiguationData":[TD([[makeQuery(id+"F4.imprint","IMPRINT",EDGE,{"derivedFrom":sQuery(id+"F4.wireOp",EDGE,"E10.11.0.0")}),1.0]])]});
            var Q20;
            Q20=makeQuery(id+"F4.imprint","IMPRINT",FACE,{"disambiguationData":[TD([[makeQuery(id+"F4.imprint","IMPRINT",EDGE,{"derivedFrom":sQuery(id+"F4.wireOp",EDGE,"E8.6.0.0")}),1.0]])]});
            var Q21;
            Q21=makeQuery(id+"F4.imprint","IMPRINT",FACE,{"disambiguationData":[TD([[makeQuery(id+"F4.imprint","IMPRINT",EDGE,{"derivedFrom":sQuery(id+"F4.wireOp",EDGE,"E8.4.0.0")}),1.0]])]});
            var Q22;
            Q22=makeQuery(id+"F4.imprint","IMPRINT",FACE,{"disambiguationData":[TD([[makeQuery(id+"F4.imprint","IMPRINT",EDGE,{"derivedFrom":sQuery(id+"F4.wireOp",EDGE,"E8.2.0.0")}),1.0]])]});
            var Q23;
            Q23=makeQuery(id+"F4.imprint","IMPRINT",FACE,{"disambiguationData":[TD([[makeQuery(id+"F4.imprint","IMPRINT",EDGE,{"derivedFrom":sQuery(id+"F4.wireOp",EDGE,"E8.8.0.0")}),1.0]])]});
            var Q24;
            Q24=makeQuery(id+"F4.imprint","IMPRINT",FACE,{"disambiguationData":[TD([[makeQuery(id+"F4.imprint","IMPRINT",EDGE,{"derivedFrom":sQuery(id+"F4.wireOp",EDGE,"E10.2.0.0")}),1.0]])]});
            var Q25;
            Q25=makeQuery(id+"F4.imprint","IMPRINT",FACE,{"disambiguationData":[TD([[makeQuery(id+"F4.imprint","IMPRINT",EDGE,{"derivedFrom":sQuery(id+"F4.wireOp",EDGE,"E10.1.0.0")}),1.0]])]});
            var Q26;
            Q26=makeQuery(id+"F4.imprint","IMPRINT",FACE,{"disambiguationData":[TD([[makeQuery(id+"F4.imprint","IMPRINT",EDGE,{"derivedFrom":sQuery(id+"F4.wireOp",EDGE,"E8.12.0.0")}),1.0]])]});
            var Q27;
            Q27=makeQuery(id+"F4.imprint","IMPRINT",FACE,{"disambiguationData":[TD([[makeQuery(id+"F4.imprint","IMPRINT",EDGE,{"derivedFrom":sQuery(id+"F4.wireOp",EDGE,"E10.14.0.0")}),1.0]])]});
            var Q28;
            Q28=makeQuery(id+"F4.imprint","IMPRINT",FACE,{"disambiguationData":[TD([[makeQuery(id+"F4.imprint","IMPRINT",EDGE,{"derivedFrom":sQuery(id+"F4.wireOp",EDGE,"E10.6.0.0")}),1.0]])]});
            var Q29;
            Q29=makeQuery(id+"F4.imprint","IMPRINT",FACE,{"disambiguationData":[TD([[makeQuery(id+"F4.imprint","IMPRINT",EDGE,{"derivedFrom":sQuery(id+"F4.wireOp",EDGE,"E10.10.0.0")}),1.0]])]});
            extrude(context, id + "F5", {"entities" : qUnion([Q0, Q1, Q2, Q3, Q4, Q5, Q6, Q7, Q8, Q9, Q10, Q11, Q12, Q13, Q14, Q15, Q16, Q17, Q18, Q19, Q20, Q21, Q22, Q23, Q24, Q25, Q26, Q27, Q28, Q29]), "depth" : 1 * mm, "offsetDistance" : 25 * mm});
        }
        {
            var Q0;
            Q0=makeQuery(id+"F4.imprint","IMPRINT",FACE,{"disambiguationData":[TD([[makeQuery(id+"F4.imprint","IMPRINT",EDGE,{"derivedFrom":sQuery(id+"F4.wireOp",EDGE,"E7.bottom")}),1.0]])]});
            var sketch = newSketch(context, id + "F6", { "sketchPlane" : qUnion([Q0])});
            skLineSegment(sketch, "E13.bottom", {"start": v(72.38, -37.37) * mm, "end": v(71.93, -37.37) * mm});
            skLineSegment(sketch, "E13.top", {"start": v(72.38, -37.87) * mm, "end": v(71.93, -37.87) * mm});
            skLineSegment(sketch, "E13.left", {"start": v(72.38, -37.37) * mm, "end": v(72.38, -37.87) * mm});
            skLineSegment(sketch, "E13.right", {"start": v(71.93, -37.37) * mm, "end": v(71.93, -37.87) * mm});
            skLineSegment(sketch, "E14.bottom", {"start": v(73.38, -35.67) * mm, "end": v(72.93, -35.67) * mm});
            skLineSegment(sketch, "E14.top", {"start": v(73.38, -36.17) * mm, "end": v(72.93, -36.17) * mm});
            skLineSegment(sketch, "E14.left", {"start": v(73.38, -35.67) * mm, "end": v(73.38, -36.17) * mm});
            skLineSegment(sketch, "E14.right", {"start": v(72.93, -35.67) * mm, "end": v(72.93, -36.17) * mm});
            skLineSegment(sketch, "E15.bottom", {"start": v(74.88, -38.17) * mm, "end": v(74.43, -38.17) * mm});
            skLineSegment(sketch, "E15.top", {"start": v(74.88, -38.67) * mm, "end": v(74.43, -38.67) * mm});
            skLineSegment(sketch, "E15.left", {"start": v(74.88, -38.17) * mm, "end": v(74.88, -38.67) * mm});
            skLineSegment(sketch, "E15.right", {"start": v(74.43, -38.17) * mm, "end": v(74.43, -38.67) * mm});
            skLineSegment(sketch, "E16.bottom", {"start": v(76.88, -38.17) * mm, "end": v(76.43, -38.17) * mm});
            skLineSegment(sketch, "E16.top", {"start": v(76.88, -38.67) * mm, "end": v(76.43, -38.67) * mm});
            skLineSegment(sketch, "E16.left", {"start": v(76.88, -38.17) * mm, "end": v(76.88, -38.67) * mm});
            skLineSegment(sketch, "E16.right", {"start": v(76.43, -38.17) * mm, "end": v(76.43, -38.67) * mm});
            skLineSegment(sketch, "E17.bottom", {"start": v(75.88, -39.87) * mm, "end": v(75.43, -39.87) * mm});
            skLineSegment(sketch, "E17.top", {"start": v(75.88, -40.37) * mm, "end": v(75.43, -40.37) * mm});
            skLineSegment(sketch, "E17.left", {"start": v(75.88, -39.87) * mm, "end": v(75.88, -40.37) * mm});
            skLineSegment(sketch, "E17.right", {"start": v(75.43, -39.87) * mm, "end": v(75.43, -40.37) * mm});
            skLineSegment(sketch, "E18.bottom", {"start": v(71.38, -35.67) * mm, "end": v(70.93, -35.67) * mm});
            skLineSegment(sketch, "E18.top", {"start": v(71.38, -36.17) * mm, "end": v(70.93, -36.17) * mm});
            skLineSegment(sketch, "E18.left", {"start": v(71.38, -35.67) * mm, "end": v(71.38, -36.17) * mm});
            skLineSegment(sketch, "E18.right", {"start": v(70.93, -35.67) * mm, "end": v(70.93, -36.17) * mm});
            skPoint(sketch, "E19", {"position": v(72.16, -37.37) * mm});
            skPoint(sketch, "E20", {"position": v(75.66, -39.87) * mm});
            skPoint(sketch, "E21", {"position": v(73.16, -36.17) * mm});
            skPoint(sketch, "E22", {"position": v(71.16, -36.17) * mm});
            skPoint(sketch, "E23", {"position": v(74.66, -38.67) * mm});
            skPoint(sketch, "E24", {"position": v(76.66, -38.67) * mm});
            skPoint(sketch, "E25.1.0.0", {"position": v(65.16, -37.37) * mm});
            skPoint(sketch, "E25.1.0.1", {"position": v(67.66, -38.67) * mm});
            skPoint(sketch, "E25.1.0.2", {"position": v(64.16, -36.17) * mm});
            skPoint(sketch, "E25.1.0.3", {"position": v(68.66, -39.87) * mm});
            skPoint(sketch, "E25.1.0.4", {"position": v(69.66, -38.67) * mm});
            skPoint(sketch, "E25.1.0.5", {"position": v(66.16, -36.17) * mm});
            skLineSegment(sketch, "E25.1.0.6", {"start": v(68.88, -40.37) * mm, "end": v(68.43, -40.37) * mm});
            skLineSegment(sketch, "E25.1.0.7", {"start": v(68.88, -39.87) * mm, "end": v(68.88, -40.37) * mm});
            skLineSegment(sketch, "E25.1.0.8", {"start": v(67.88, -38.17) * mm, "end": v(67.43, -38.17) * mm});
            skLineSegment(sketch, "E25.1.0.9", {"start": v(66.38, -36.17) * mm, "end": v(65.93, -36.17) * mm});
            skLineSegment(sketch, "E25.1.0.10", {"start": v(69.88, -38.17) * mm, "end": v(69.43, -38.17) * mm});
            skLineSegment(sketch, "E25.1.0.11", {"start": v(64.38, -35.67) * mm, "end": v(63.93, -35.67) * mm});
            skLineSegment(sketch, "E25.1.0.12", {"start": v(64.38, -36.17) * mm, "end": v(63.93, -36.17) * mm});
            skLineSegment(sketch, "E25.1.0.13", {"start": v(65.38, -37.37) * mm, "end": v(65.38, -37.87) * mm});
            skLineSegment(sketch, "E25.1.0.14", {"start": v(68.88, -39.87) * mm, "end": v(68.43, -39.87) * mm});
            skLineSegment(sketch, "E25.1.0.15", {"start": v(66.38, -35.67) * mm, "end": v(66.38, -36.17) * mm});
            skLineSegment(sketch, "E25.1.0.16", {"start": v(64.38, -35.67) * mm, "end": v(64.38, -36.17) * mm});
            skLineSegment(sketch, "E25.1.0.17", {"start": v(67.88, -38.17) * mm, "end": v(67.88, -38.67) * mm});
            skLineSegment(sketch, "E25.1.0.18", {"start": v(66.38, -35.67) * mm, "end": v(65.93, -35.67) * mm});
            skLineSegment(sketch, "E25.1.0.19", {"start": v(69.88, -38.17) * mm, "end": v(69.88, -38.67) * mm});
            skLineSegment(sketch, "E25.1.0.20", {"start": v(65.38, -37.37) * mm, "end": v(64.93, -37.37) * mm});
            skLineSegment(sketch, "E25.1.0.21", {"start": v(65.93, -35.67) * mm, "end": v(65.93, -36.17) * mm});
            skLineSegment(sketch, "E25.1.0.22", {"start": v(65.38, -37.87) * mm, "end": v(64.93, -37.87) * mm});
            skLineSegment(sketch, "E25.1.0.23", {"start": v(68.43, -39.87) * mm, "end": v(68.43, -40.37) * mm});
            skLineSegment(sketch, "E25.1.0.24", {"start": v(67.43, -38.17) * mm, "end": v(67.43, -38.67) * mm});
            skLineSegment(sketch, "E25.1.0.25", {"start": v(69.88, -38.67) * mm, "end": v(69.43, -38.67) * mm});
            skLineSegment(sketch, "E25.1.0.26", {"start": v(69.43, -38.17) * mm, "end": v(69.43, -38.67) * mm});
            skLineSegment(sketch, "E25.1.0.27", {"start": v(67.88, -38.67) * mm, "end": v(67.43, -38.67) * mm});
            skLineSegment(sketch, "E25.1.0.28", {"start": v(63.93, -35.67) * mm, "end": v(63.93, -36.17) * mm});
            skLineSegment(sketch, "E25.1.0.29", {"start": v(64.93, -37.37) * mm, "end": v(64.93, -37.87) * mm});
            skPoint(sketch, "E25.2.0.0", {"position": v(58.16, -37.37) * mm});
            skPoint(sketch, "E25.2.0.1", {"position": v(60.66, -38.67) * mm});
            skPoint(sketch, "E25.2.0.2", {"position": v(57.16, -36.17) * mm});
            skPoint(sketch, "E25.2.0.3", {"position": v(61.66, -39.87) * mm});
            skPoint(sketch, "E25.2.0.4", {"position": v(62.66, -38.67) * mm});
            skPoint(sketch, "E25.2.0.5", {"position": v(59.16, -36.17) * mm});
            skLineSegment(sketch, "E25.2.0.6", {"start": v(61.88, -40.37) * mm, "end": v(61.43, -40.37) * mm});
            skLineSegment(sketch, "E25.2.0.7", {"start": v(61.88, -39.87) * mm, "end": v(61.88, -40.37) * mm});
            skLineSegment(sketch, "E25.2.0.8", {"start": v(60.88, -38.17) * mm, "end": v(60.43, -38.17) * mm});
            skLineSegment(sketch, "E25.2.0.9", {"start": v(59.38, -36.17) * mm, "end": v(58.93, -36.17) * mm});
            skLineSegment(sketch, "E25.2.0.10", {"start": v(62.88, -38.17) * mm, "end": v(62.43, -38.17) * mm});
            skLineSegment(sketch, "E25.2.0.11", {"start": v(57.38, -35.67) * mm, "end": v(56.93, -35.67) * mm});
            skLineSegment(sketch, "E25.2.0.12", {"start": v(57.38, -36.17) * mm, "end": v(56.93, -36.17) * mm});
            skLineSegment(sketch, "E25.2.0.13", {"start": v(58.38, -37.37) * mm, "end": v(58.38, -37.87) * mm});
            skLineSegment(sketch, "E25.2.0.14", {"start": v(61.88, -39.87) * mm, "end": v(61.43, -39.87) * mm});
            skLineSegment(sketch, "E25.2.0.15", {"start": v(59.38, -35.67) * mm, "end": v(59.38, -36.17) * mm});
            skLineSegment(sketch, "E25.2.0.16", {"start": v(57.38, -35.67) * mm, "end": v(57.38, -36.17) * mm});
            skLineSegment(sketch, "E25.2.0.17", {"start": v(60.88, -38.17) * mm, "end": v(60.88, -38.67) * mm});
            skLineSegment(sketch, "E25.2.0.18", {"start": v(59.38, -35.67) * mm, "end": v(58.93, -35.67) * mm});
            skLineSegment(sketch, "E25.2.0.19", {"start": v(62.88, -38.17) * mm, "end": v(62.88, -38.67) * mm});
            skLineSegment(sketch, "E25.2.0.20", {"start": v(58.38, -37.37) * mm, "end": v(57.93, -37.37) * mm});
            skLineSegment(sketch, "E25.2.0.21", {"start": v(58.93, -35.67) * mm, "end": v(58.93, -36.17) * mm});
            skLineSegment(sketch, "E25.2.0.22", {"start": v(58.38, -37.87) * mm, "end": v(57.93, -37.87) * mm});
            skLineSegment(sketch, "E25.2.0.23", {"start": v(61.43, -39.87) * mm, "end": v(61.43, -40.37) * mm});
            skLineSegment(sketch, "E25.2.0.24", {"start": v(60.43, -38.17) * mm, "end": v(60.43, -38.67) * mm});
            skLineSegment(sketch, "E25.2.0.25", {"start": v(62.88, -38.67) * mm, "end": v(62.43, -38.67) * mm});
            skLineSegment(sketch, "E25.2.0.26", {"start": v(62.43, -38.17) * mm, "end": v(62.43, -38.67) * mm});
            skLineSegment(sketch, "E25.2.0.27", {"start": v(60.88, -38.67) * mm, "end": v(60.43, -38.67) * mm});
            skLineSegment(sketch, "E25.2.0.28", {"start": v(56.93, -35.67) * mm, "end": v(56.93, -36.17) * mm});
            skLineSegment(sketch, "E25.2.0.29", {"start": v(57.93, -37.37) * mm, "end": v(57.93, -37.87) * mm});
            skPoint(sketch, "E25.3.0.0", {"position": v(51.16, -37.37) * mm});
            skPoint(sketch, "E25.3.0.1", {"position": v(53.66, -38.67) * mm});
            skPoint(sketch, "E25.3.0.2", {"position": v(50.16, -36.17) * mm});
            skPoint(sketch, "E25.3.0.3", {"position": v(54.66, -39.87) * mm});
            skPoint(sketch, "E25.3.0.4", {"position": v(55.66, -38.67) * mm});
            skPoint(sketch, "E25.3.0.5", {"position": v(52.16, -36.17) * mm});
            skLineSegment(sketch, "E25.3.0.6", {"start": v(54.88, -40.37) * mm, "end": v(54.43, -40.37) * mm});
            skLineSegment(sketch, "E25.3.0.7", {"start": v(54.88, -39.87) * mm, "end": v(54.88, -40.37) * mm});
            skLineSegment(sketch, "E25.3.0.8", {"start": v(53.88, -38.17) * mm, "end": v(53.43, -38.17) * mm});
            skLineSegment(sketch, "E25.3.0.9", {"start": v(52.38, -36.17) * mm, "end": v(51.93, -36.17) * mm});
            skLineSegment(sketch, "E25.3.0.10", {"start": v(55.88, -38.17) * mm, "end": v(55.43, -38.17) * mm});
            skLineSegment(sketch, "E25.3.0.11", {"start": v(50.38, -35.67) * mm, "end": v(49.93, -35.67) * mm});
            skLineSegment(sketch, "E25.3.0.12", {"start": v(50.38, -36.17) * mm, "end": v(49.93, -36.17) * mm});
            skLineSegment(sketch, "E25.3.0.13", {"start": v(51.38, -37.37) * mm, "end": v(51.38, -37.87) * mm});
            skLineSegment(sketch, "E25.3.0.14", {"start": v(54.88, -39.87) * mm, "end": v(54.43, -39.87) * mm});
            skLineSegment(sketch, "E25.3.0.15", {"start": v(52.38, -35.67) * mm, "end": v(52.38, -36.17) * mm});
            skLineSegment(sketch, "E25.3.0.16", {"start": v(50.38, -35.67) * mm, "end": v(50.38, -36.17) * mm});
            skLineSegment(sketch, "E25.3.0.17", {"start": v(53.88, -38.17) * mm, "end": v(53.88, -38.67) * mm});
            skLineSegment(sketch, "E25.3.0.18", {"start": v(52.38, -35.67) * mm, "end": v(51.93, -35.67) * mm});
            skLineSegment(sketch, "E25.3.0.19", {"start": v(55.88, -38.17) * mm, "end": v(55.88, -38.67) * mm});
            skLineSegment(sketch, "E25.3.0.20", {"start": v(51.38, -37.37) * mm, "end": v(50.93, -37.37) * mm});
            skLineSegment(sketch, "E25.3.0.21", {"start": v(51.93, -35.67) * mm, "end": v(51.93, -36.17) * mm});
            skLineSegment(sketch, "E25.3.0.22", {"start": v(51.38, -37.87) * mm, "end": v(50.93, -37.87) * mm});
            skLineSegment(sketch, "E25.3.0.23", {"start": v(54.43, -39.87) * mm, "end": v(54.43, -40.37) * mm});
            skLineSegment(sketch, "E25.3.0.24", {"start": v(53.43, -38.17) * mm, "end": v(53.43, -38.67) * mm});
            skLineSegment(sketch, "E25.3.0.25", {"start": v(55.88, -38.67) * mm, "end": v(55.43, -38.67) * mm});
            skLineSegment(sketch, "E25.3.0.26", {"start": v(55.43, -38.17) * mm, "end": v(55.43, -38.67) * mm});
            skLineSegment(sketch, "E25.3.0.27", {"start": v(53.88, -38.67) * mm, "end": v(53.43, -38.67) * mm});
            skLineSegment(sketch, "E25.3.0.28", {"start": v(49.93, -35.67) * mm, "end": v(49.93, -36.17) * mm});
            skLineSegment(sketch, "E25.3.0.29", {"start": v(50.93, -37.37) * mm, "end": v(50.93, -37.87) * mm});
            skPoint(sketch, "E25.4.0.0", {"position": v(44.16, -37.37) * mm});
            skPoint(sketch, "E25.4.0.1", {"position": v(46.66, -38.67) * mm});
            skPoint(sketch, "E25.4.0.2", {"position": v(43.16, -36.17) * mm});
            skPoint(sketch, "E25.4.0.3", {"position": v(47.66, -39.87) * mm});
            skPoint(sketch, "E25.4.0.4", {"position": v(48.66, -38.67) * mm});
            skPoint(sketch, "E25.4.0.5", {"position": v(45.16, -36.17) * mm});
            skLineSegment(sketch, "E25.4.0.6", {"start": v(47.88, -40.37) * mm, "end": v(47.43, -40.37) * mm});
            skLineSegment(sketch, "E25.4.0.7", {"start": v(47.88, -39.87) * mm, "end": v(47.88, -40.37) * mm});
            skLineSegment(sketch, "E25.4.0.8", {"start": v(46.88, -38.17) * mm, "end": v(46.43, -38.17) * mm});
            skLineSegment(sketch, "E25.4.0.9", {"start": v(45.38, -36.17) * mm, "end": v(44.93, -36.17) * mm});
            skLineSegment(sketch, "E25.4.0.10", {"start": v(48.88, -38.17) * mm, "end": v(48.43, -38.17) * mm});
            skLineSegment(sketch, "E25.4.0.11", {"start": v(43.38, -35.67) * mm, "end": v(42.93, -35.67) * mm});
            skLineSegment(sketch, "E25.4.0.12", {"start": v(43.38, -36.17) * mm, "end": v(42.93, -36.17) * mm});
            skLineSegment(sketch, "E25.4.0.13", {"start": v(44.38, -37.37) * mm, "end": v(44.38, -37.87) * mm});
            skLineSegment(sketch, "E25.4.0.14", {"start": v(47.88, -39.87) * mm, "end": v(47.43, -39.87) * mm});
            skLineSegment(sketch, "E25.4.0.15", {"start": v(45.38, -35.67) * mm, "end": v(45.38, -36.17) * mm});
            skLineSegment(sketch, "E25.4.0.16", {"start": v(43.38, -35.67) * mm, "end": v(43.38, -36.17) * mm});
            skLineSegment(sketch, "E25.4.0.17", {"start": v(46.88, -38.17) * mm, "end": v(46.88, -38.67) * mm});
            skLineSegment(sketch, "E25.4.0.18", {"start": v(45.38, -35.67) * mm, "end": v(44.93, -35.67) * mm});
            skLineSegment(sketch, "E25.4.0.19", {"start": v(48.88, -38.17) * mm, "end": v(48.88, -38.67) * mm});
            skLineSegment(sketch, "E25.4.0.20", {"start": v(44.38, -37.37) * mm, "end": v(43.93, -37.37) * mm});
            skLineSegment(sketch, "E25.4.0.21", {"start": v(44.93, -35.67) * mm, "end": v(44.93, -36.17) * mm});
            skLineSegment(sketch, "E25.4.0.22", {"start": v(44.38, -37.87) * mm, "end": v(43.93, -37.87) * mm});
            skLineSegment(sketch, "E25.4.0.23", {"start": v(47.43, -39.87) * mm, "end": v(47.43, -40.37) * mm});
            skLineSegment(sketch, "E25.4.0.24", {"start": v(46.43, -38.17) * mm, "end": v(46.43, -38.67) * mm});
            skLineSegment(sketch, "E25.4.0.25", {"start": v(48.88, -38.67) * mm, "end": v(48.43, -38.67) * mm});
            skLineSegment(sketch, "E25.4.0.26", {"start": v(48.43, -38.17) * mm, "end": v(48.43, -38.67) * mm});
            skLineSegment(sketch, "E25.4.0.27", {"start": v(46.88, -38.67) * mm, "end": v(46.43, -38.67) * mm});
            skLineSegment(sketch, "E25.4.0.28", {"start": v(42.93, -35.67) * mm, "end": v(42.93, -36.17) * mm});
            skLineSegment(sketch, "E25.4.0.29", {"start": v(43.93, -37.37) * mm, "end": v(43.93, -37.87) * mm});
            skPoint(sketch, "E25.5.0.0", {"position": v(37.16, -37.37) * mm});
            skPoint(sketch, "E25.5.0.1", {"position": v(39.66, -38.67) * mm});
            skPoint(sketch, "E25.5.0.2", {"position": v(36.16, -36.17) * mm});
            skPoint(sketch, "E25.5.0.3", {"position": v(40.66, -39.87) * mm});
            skPoint(sketch, "E25.5.0.4", {"position": v(41.66, -38.67) * mm});
            skPoint(sketch, "E25.5.0.5", {"position": v(38.16, -36.17) * mm});
            skLineSegment(sketch, "E25.5.0.6", {"start": v(40.88, -40.37) * mm, "end": v(40.43, -40.37) * mm});
            skLineSegment(sketch, "E25.5.0.7", {"start": v(40.88, -39.87) * mm, "end": v(40.88, -40.37) * mm});
            skLineSegment(sketch, "E25.5.0.8", {"start": v(39.88, -38.17) * mm, "end": v(39.43, -38.17) * mm});
            skLineSegment(sketch, "E25.5.0.9", {"start": v(38.38, -36.17) * mm, "end": v(37.93, -36.17) * mm});
            skLineSegment(sketch, "E25.5.0.10", {"start": v(41.88, -38.17) * mm, "end": v(41.43, -38.17) * mm});
            skLineSegment(sketch, "E25.5.0.11", {"start": v(36.38, -35.67) * mm, "end": v(35.93, -35.67) * mm});
            skLineSegment(sketch, "E25.5.0.12", {"start": v(36.38, -36.17) * mm, "end": v(35.93, -36.17) * mm});
            skLineSegment(sketch, "E25.5.0.13", {"start": v(37.38, -37.37) * mm, "end": v(37.38, -37.87) * mm});
            skLineSegment(sketch, "E25.5.0.14", {"start": v(40.88, -39.87) * mm, "end": v(40.43, -39.87) * mm});
            skLineSegment(sketch, "E25.5.0.15", {"start": v(38.38, -35.67) * mm, "end": v(38.38, -36.17) * mm});
            skLineSegment(sketch, "E25.5.0.16", {"start": v(36.38, -35.67) * mm, "end": v(36.38, -36.17) * mm});
            skLineSegment(sketch, "E25.5.0.17", {"start": v(39.88, -38.17) * mm, "end": v(39.88, -38.67) * mm});
            skLineSegment(sketch, "E25.5.0.18", {"start": v(38.38, -35.67) * mm, "end": v(37.93, -35.67) * mm});
            skLineSegment(sketch, "E25.5.0.19", {"start": v(41.88, -38.17) * mm, "end": v(41.88, -38.67) * mm});
            skLineSegment(sketch, "E25.5.0.20", {"start": v(37.38, -37.37) * mm, "end": v(36.93, -37.37) * mm});
            skLineSegment(sketch, "E25.5.0.21", {"start": v(37.93, -35.67) * mm, "end": v(37.93, -36.17) * mm});
            skLineSegment(sketch, "E25.5.0.22", {"start": v(37.38, -37.87) * mm, "end": v(36.93, -37.87) * mm});
            skLineSegment(sketch, "E25.5.0.23", {"start": v(40.43, -39.87) * mm, "end": v(40.43, -40.37) * mm});
            skLineSegment(sketch, "E25.5.0.24", {"start": v(39.43, -38.17) * mm, "end": v(39.43, -38.67) * mm});
            skLineSegment(sketch, "E25.5.0.25", {"start": v(41.88, -38.67) * mm, "end": v(41.43, -38.67) * mm});
            skLineSegment(sketch, "E25.5.0.26", {"start": v(41.43, -38.17) * mm, "end": v(41.43, -38.67) * mm});
            skLineSegment(sketch, "E25.5.0.27", {"start": v(39.88, -38.67) * mm, "end": v(39.43, -38.67) * mm});
            skLineSegment(sketch, "E25.5.0.28", {"start": v(35.93, -35.67) * mm, "end": v(35.93, -36.17) * mm});
            skLineSegment(sketch, "E25.5.0.29", {"start": v(36.93, -37.37) * mm, "end": v(36.93, -37.87) * mm});
            skPoint(sketch, "E25.6.0.0", {"position": v(30.16, -37.37) * mm});
            skPoint(sketch, "E25.6.0.1", {"position": v(32.66, -38.67) * mm});
            skPoint(sketch, "E25.6.0.2", {"position": v(29.16, -36.17) * mm});
            skPoint(sketch, "E25.6.0.3", {"position": v(33.66, -39.87) * mm});
            skPoint(sketch, "E25.6.0.4", {"position": v(34.66, -38.67) * mm});
            skPoint(sketch, "E25.6.0.5", {"position": v(31.16, -36.17) * mm});
            skLineSegment(sketch, "E25.6.0.6", {"start": v(33.88, -40.37) * mm, "end": v(33.43, -40.37) * mm});
            skLineSegment(sketch, "E25.6.0.7", {"start": v(33.88, -39.87) * mm, "end": v(33.88, -40.37) * mm});
            skLineSegment(sketch, "E25.6.0.8", {"start": v(32.88, -38.17) * mm, "end": v(32.43, -38.17) * mm});
            skLineSegment(sketch, "E25.6.0.9", {"start": v(31.38, -36.17) * mm, "end": v(30.93, -36.17) * mm});
            skLineSegment(sketch, "E25.6.0.10", {"start": v(34.88, -38.17) * mm, "end": v(34.43, -38.17) * mm});
            skLineSegment(sketch, "E25.6.0.11", {"start": v(29.38, -35.67) * mm, "end": v(28.93, -35.67) * mm});
            skLineSegment(sketch, "E25.6.0.12", {"start": v(29.38, -36.17) * mm, "end": v(28.93, -36.17) * mm});
            skLineSegment(sketch, "E25.6.0.13", {"start": v(30.38, -37.37) * mm, "end": v(30.38, -37.87) * mm});
            skLineSegment(sketch, "E25.6.0.14", {"start": v(33.88, -39.87) * mm, "end": v(33.43, -39.87) * mm});
            skLineSegment(sketch, "E25.6.0.15", {"start": v(31.38, -35.67) * mm, "end": v(31.38, -36.17) * mm});
            skLineSegment(sketch, "E25.6.0.16", {"start": v(29.38, -35.67) * mm, "end": v(29.38, -36.17) * mm});
            skLineSegment(sketch, "E25.6.0.17", {"start": v(32.88, -38.17) * mm, "end": v(32.88, -38.67) * mm});
            skLineSegment(sketch, "E25.6.0.18", {"start": v(31.38, -35.67) * mm, "end": v(30.93, -35.67) * mm});
            skLineSegment(sketch, "E25.6.0.19", {"start": v(34.88, -38.17) * mm, "end": v(34.88, -38.67) * mm});
            skLineSegment(sketch, "E25.6.0.20", {"start": v(30.38, -37.37) * mm, "end": v(29.93, -37.37) * mm});
            skLineSegment(sketch, "E25.6.0.21", {"start": v(30.93, -35.67) * mm, "end": v(30.93, -36.17) * mm});
            skLineSegment(sketch, "E25.6.0.22", {"start": v(30.38, -37.87) * mm, "end": v(29.93, -37.87) * mm});
            skLineSegment(sketch, "E25.6.0.23", {"start": v(33.43, -39.87) * mm, "end": v(33.43, -40.37) * mm});
            skLineSegment(sketch, "E25.6.0.24", {"start": v(32.43, -38.17) * mm, "end": v(32.43, -38.67) * mm});
            skLineSegment(sketch, "E25.6.0.25", {"start": v(34.88, -38.67) * mm, "end": v(34.43, -38.67) * mm});
            skLineSegment(sketch, "E25.6.0.26", {"start": v(34.43, -38.17) * mm, "end": v(34.43, -38.67) * mm});
            skLineSegment(sketch, "E25.6.0.27", {"start": v(32.88, -38.67) * mm, "end": v(32.43, -38.67) * mm});
            skLineSegment(sketch, "E25.6.0.28", {"start": v(28.93, -35.67) * mm, "end": v(28.93, -36.17) * mm});
            skLineSegment(sketch, "E25.6.0.29", {"start": v(29.93, -37.37) * mm, "end": v(29.93, -37.87) * mm});
            skPoint(sketch, "E25.7.0.0", {"position": v(23.16, -37.37) * mm});
            skPoint(sketch, "E25.7.0.1", {"position": v(25.66, -38.67) * mm});
            skPoint(sketch, "E25.7.0.2", {"position": v(22.16, -36.17) * mm});
            skPoint(sketch, "E25.7.0.3", {"position": v(26.66, -39.87) * mm});
            skPoint(sketch, "E25.7.0.4", {"position": v(27.66, -38.67) * mm});
            skPoint(sketch, "E25.7.0.5", {"position": v(24.16, -36.17) * mm});
            skLineSegment(sketch, "E25.7.0.6", {"start": v(26.88, -40.37) * mm, "end": v(26.43, -40.37) * mm});
            skLineSegment(sketch, "E25.7.0.7", {"start": v(26.88, -39.87) * mm, "end": v(26.88, -40.37) * mm});
            skLineSegment(sketch, "E25.7.0.8", {"start": v(25.88, -38.17) * mm, "end": v(25.43, -38.17) * mm});
            skLineSegment(sketch, "E25.7.0.9", {"start": v(24.38, -36.17) * mm, "end": v(23.93, -36.17) * mm});
            skLineSegment(sketch, "E25.7.0.10", {"start": v(27.88, -38.17) * mm, "end": v(27.43, -38.17) * mm});
            skLineSegment(sketch, "E25.7.0.11", {"start": v(22.38, -35.67) * mm, "end": v(21.93, -35.67) * mm});
            skLineSegment(sketch, "E25.7.0.12", {"start": v(22.38, -36.17) * mm, "end": v(21.93, -36.17) * mm});
            skLineSegment(sketch, "E25.7.0.13", {"start": v(23.38, -37.37) * mm, "end": v(23.38, -37.87) * mm});
            skLineSegment(sketch, "E25.7.0.14", {"start": v(26.88, -39.87) * mm, "end": v(26.43, -39.87) * mm});
            skLineSegment(sketch, "E25.7.0.15", {"start": v(24.38, -35.67) * mm, "end": v(24.38, -36.17) * mm});
            skLineSegment(sketch, "E25.7.0.16", {"start": v(22.38, -35.67) * mm, "end": v(22.38, -36.17) * mm});
            skLineSegment(sketch, "E25.7.0.17", {"start": v(25.88, -38.17) * mm, "end": v(25.88, -38.67) * mm});
            skLineSegment(sketch, "E25.7.0.18", {"start": v(24.38, -35.67) * mm, "end": v(23.93, -35.67) * mm});
            skLineSegment(sketch, "E25.7.0.19", {"start": v(27.88, -38.17) * mm, "end": v(27.88, -38.67) * mm});
            skLineSegment(sketch, "E25.7.0.20", {"start": v(23.38, -37.37) * mm, "end": v(22.93, -37.37) * mm});
            skLineSegment(sketch, "E25.7.0.21", {"start": v(23.93, -35.67) * mm, "end": v(23.93, -36.17) * mm});
            skLineSegment(sketch, "E25.7.0.22", {"start": v(23.38, -37.87) * mm, "end": v(22.93, -37.87) * mm});
            skLineSegment(sketch, "E25.7.0.23", {"start": v(26.43, -39.87) * mm, "end": v(26.43, -40.37) * mm});
            skLineSegment(sketch, "E25.7.0.24", {"start": v(25.43, -38.17) * mm, "end": v(25.43, -38.67) * mm});
            skLineSegment(sketch, "E25.7.0.25", {"start": v(27.88, -38.67) * mm, "end": v(27.43, -38.67) * mm});
            skLineSegment(sketch, "E25.7.0.26", {"start": v(27.43, -38.17) * mm, "end": v(27.43, -38.67) * mm});
            skLineSegment(sketch, "E25.7.0.27", {"start": v(25.88, -38.67) * mm, "end": v(25.43, -38.67) * mm});
            skLineSegment(sketch, "E25.7.0.28", {"start": v(21.93, -35.67) * mm, "end": v(21.93, -36.17) * mm});
            skLineSegment(sketch, "E25.7.0.29", {"start": v(22.93, -37.37) * mm, "end": v(22.93, -37.87) * mm});
            skPoint(sketch, "E25.8.0.0", {"position": v(16.16, -37.37) * mm});
            skPoint(sketch, "E25.8.0.1", {"position": v(18.66, -38.67) * mm});
            skPoint(sketch, "E25.8.0.2", {"position": v(15.16, -36.17) * mm});
            skPoint(sketch, "E25.8.0.3", {"position": v(19.66, -39.87) * mm});
            skPoint(sketch, "E25.8.0.4", {"position": v(20.66, -38.67) * mm});
            skPoint(sketch, "E25.8.0.5", {"position": v(17.16, -36.17) * mm});
            skLineSegment(sketch, "E25.8.0.6", {"start": v(19.88, -40.37) * mm, "end": v(19.43, -40.37) * mm});
            skLineSegment(sketch, "E25.8.0.7", {"start": v(19.88, -39.87) * mm, "end": v(19.88, -40.37) * mm});
            skLineSegment(sketch, "E25.8.0.8", {"start": v(18.88, -38.17) * mm, "end": v(18.43, -38.17) * mm});
            skLineSegment(sketch, "E25.8.0.9", {"start": v(17.38, -36.17) * mm, "end": v(16.93, -36.17) * mm});
            skLineSegment(sketch, "E25.8.0.10", {"start": v(20.88, -38.17) * mm, "end": v(20.43, -38.17) * mm});
            skLineSegment(sketch, "E25.8.0.11", {"start": v(15.38, -35.67) * mm, "end": v(14.93, -35.67) * mm});
            skLineSegment(sketch, "E25.8.0.12", {"start": v(15.38, -36.17) * mm, "end": v(14.93, -36.17) * mm});
            skLineSegment(sketch, "E25.8.0.13", {"start": v(16.38, -37.37) * mm, "end": v(16.38, -37.87) * mm});
            skLineSegment(sketch, "E25.8.0.14", {"start": v(19.88, -39.87) * mm, "end": v(19.43, -39.87) * mm});
            skLineSegment(sketch, "E25.8.0.15", {"start": v(17.38, -35.67) * mm, "end": v(17.38, -36.17) * mm});
            skLineSegment(sketch, "E25.8.0.16", {"start": v(15.38, -35.67) * mm, "end": v(15.38, -36.17) * mm});
            skLineSegment(sketch, "E25.8.0.17", {"start": v(18.88, -38.17) * mm, "end": v(18.88, -38.67) * mm});
            skLineSegment(sketch, "E25.8.0.18", {"start": v(17.38, -35.67) * mm, "end": v(16.93, -35.67) * mm});
            skLineSegment(sketch, "E25.8.0.19", {"start": v(20.88, -38.17) * mm, "end": v(20.88, -38.67) * mm});
            skLineSegment(sketch, "E25.8.0.20", {"start": v(16.38, -37.37) * mm, "end": v(15.93, -37.37) * mm});
            skLineSegment(sketch, "E25.8.0.21", {"start": v(16.93, -35.67) * mm, "end": v(16.93, -36.17) * mm});
            skLineSegment(sketch, "E25.8.0.22", {"start": v(16.38, -37.87) * mm, "end": v(15.93, -37.87) * mm});
            skLineSegment(sketch, "E25.8.0.23", {"start": v(19.43, -39.87) * mm, "end": v(19.43, -40.37) * mm});
            skLineSegment(sketch, "E25.8.0.24", {"start": v(18.43, -38.17) * mm, "end": v(18.43, -38.67) * mm});
            skLineSegment(sketch, "E25.8.0.25", {"start": v(20.88, -38.67) * mm, "end": v(20.43, -38.67) * mm});
            skLineSegment(sketch, "E25.8.0.26", {"start": v(20.43, -38.17) * mm, "end": v(20.43, -38.67) * mm});
            skLineSegment(sketch, "E25.8.0.27", {"start": v(18.88, -38.67) * mm, "end": v(18.43, -38.67) * mm});
            skLineSegment(sketch, "E25.8.0.28", {"start": v(14.93, -35.67) * mm, "end": v(14.93, -36.17) * mm});
            skLineSegment(sketch, "E25.8.0.29", {"start": v(15.93, -37.37) * mm, "end": v(15.93, -37.87) * mm});
            skPoint(sketch, "E25.9.0.0", {"position": v(9.16, -37.37) * mm});
            skPoint(sketch, "E25.9.0.1", {"position": v(11.66, -38.67) * mm});
            skPoint(sketch, "E25.9.0.2", {"position": v(8.16, -36.17) * mm});
            skPoint(sketch, "E25.9.0.3", {"position": v(12.66, -39.87) * mm});
            skPoint(sketch, "E25.9.0.4", {"position": v(13.66, -38.67) * mm});
            skPoint(sketch, "E25.9.0.5", {"position": v(10.16, -36.17) * mm});
            skLineSegment(sketch, "E25.9.0.6", {"start": v(12.88, -40.37) * mm, "end": v(12.43, -40.37) * mm});
            skLineSegment(sketch, "E25.9.0.7", {"start": v(12.88, -39.87) * mm, "end": v(12.88, -40.37) * mm});
            skLineSegment(sketch, "E25.9.0.8", {"start": v(11.88, -38.17) * mm, "end": v(11.43, -38.17) * mm});
            skLineSegment(sketch, "E25.9.0.9", {"start": v(10.38, -36.17) * mm, "end": v(9.93, -36.17) * mm});
            skLineSegment(sketch, "E25.9.0.10", {"start": v(13.88, -38.17) * mm, "end": v(13.43, -38.17) * mm});
            skLineSegment(sketch, "E25.9.0.11", {"start": v(8.38, -35.67) * mm, "end": v(7.93, -35.67) * mm});
            skLineSegment(sketch, "E25.9.0.12", {"start": v(8.38, -36.17) * mm, "end": v(7.93, -36.17) * mm});
            skLineSegment(sketch, "E25.9.0.13", {"start": v(9.38, -37.37) * mm, "end": v(9.38, -37.87) * mm});
            skLineSegment(sketch, "E25.9.0.14", {"start": v(12.88, -39.87) * mm, "end": v(12.43, -39.87) * mm});
            skLineSegment(sketch, "E25.9.0.15", {"start": v(10.38, -35.67) * mm, "end": v(10.38, -36.17) * mm});
            skLineSegment(sketch, "E25.9.0.16", {"start": v(8.38, -35.67) * mm, "end": v(8.38, -36.17) * mm});
            skLineSegment(sketch, "E25.9.0.17", {"start": v(11.88, -38.17) * mm, "end": v(11.88, -38.67) * mm});
            skLineSegment(sketch, "E25.9.0.18", {"start": v(10.38, -35.67) * mm, "end": v(9.93, -35.67) * mm});
            skLineSegment(sketch, "E25.9.0.19", {"start": v(13.88, -38.17) * mm, "end": v(13.88, -38.67) * mm});
            skLineSegment(sketch, "E25.9.0.20", {"start": v(9.38, -37.37) * mm, "end": v(8.93, -37.37) * mm});
            skLineSegment(sketch, "E25.9.0.21", {"start": v(9.93, -35.67) * mm, "end": v(9.93, -36.17) * mm});
            skLineSegment(sketch, "E25.9.0.22", {"start": v(9.38, -37.87) * mm, "end": v(8.93, -37.87) * mm});
            skLineSegment(sketch, "E25.9.0.23", {"start": v(12.43, -39.87) * mm, "end": v(12.43, -40.37) * mm});
            skLineSegment(sketch, "E25.9.0.24", {"start": v(11.43, -38.17) * mm, "end": v(11.43, -38.67) * mm});
            skLineSegment(sketch, "E25.9.0.25", {"start": v(13.88, -38.67) * mm, "end": v(13.43, -38.67) * mm});
            skLineSegment(sketch, "E25.9.0.26", {"start": v(13.43, -38.17) * mm, "end": v(13.43, -38.67) * mm});
            skLineSegment(sketch, "E25.9.0.27", {"start": v(11.88, -38.67) * mm, "end": v(11.43, -38.67) * mm});
            skLineSegment(sketch, "E25.9.0.28", {"start": v(7.93, -35.67) * mm, "end": v(7.93, -36.17) * mm});
            skLineSegment(sketch, "E25.9.0.29", {"start": v(8.93, -37.37) * mm, "end": v(8.93, -37.87) * mm});
            skPoint(sketch, "E25.10.0.0", {"position": v(2.16, -37.37) * mm});
            skPoint(sketch, "E25.10.0.1", {"position": v(4.66, -38.67) * mm});
            skPoint(sketch, "E25.10.0.2", {"position": v(1.16, -36.17) * mm});
            skPoint(sketch, "E25.10.0.3", {"position": v(5.66, -39.87) * mm});
            skPoint(sketch, "E25.10.0.4", {"position": v(6.66, -38.67) * mm});
            skPoint(sketch, "E25.10.0.5", {"position": v(3.16, -36.17) * mm});
            skLineSegment(sketch, "E25.10.0.6", {"start": v(5.88, -40.37) * mm, "end": v(5.43, -40.37) * mm});
            skLineSegment(sketch, "E25.10.0.7", {"start": v(5.88, -39.87) * mm, "end": v(5.88, -40.37) * mm});
            skLineSegment(sketch, "E25.10.0.8", {"start": v(4.88, -38.17) * mm, "end": v(4.43, -38.17) * mm});
            skLineSegment(sketch, "E25.10.0.9", {"start": v(3.38, -36.17) * mm, "end": v(2.93, -36.17) * mm});
            skLineSegment(sketch, "E25.10.0.10", {"start": v(6.88, -38.17) * mm, "end": v(6.43, -38.17) * mm});
            skLineSegment(sketch, "E25.10.0.11", {"start": v(1.38, -35.67) * mm, "end": v(0.93, -35.67) * mm});
            skLineSegment(sketch, "E25.10.0.12", {"start": v(1.38, -36.17) * mm, "end": v(0.93, -36.17) * mm});
            skLineSegment(sketch, "E25.10.0.13", {"start": v(2.38, -37.37) * mm, "end": v(2.38, -37.87) * mm});
            skLineSegment(sketch, "E25.10.0.14", {"start": v(5.88, -39.87) * mm, "end": v(5.43, -39.87) * mm});
            skLineSegment(sketch, "E25.10.0.15", {"start": v(3.38, -35.67) * mm, "end": v(3.38, -36.17) * mm});
            skLineSegment(sketch, "E25.10.0.16", {"start": v(1.38, -35.67) * mm, "end": v(1.38, -36.17) * mm});
            skLineSegment(sketch, "E25.10.0.17", {"start": v(4.88, -38.17) * mm, "end": v(4.88, -38.67) * mm});
            skLineSegment(sketch, "E25.10.0.18", {"start": v(3.38, -35.67) * mm, "end": v(2.93, -35.67) * mm});
            skLineSegment(sketch, "E25.10.0.19", {"start": v(6.88, -38.17) * mm, "end": v(6.88, -38.67) * mm});
            skLineSegment(sketch, "E25.10.0.20", {"start": v(2.38, -37.37) * mm, "end": v(1.93, -37.37) * mm});
            skLineSegment(sketch, "E25.10.0.21", {"start": v(2.93, -35.67) * mm, "end": v(2.93, -36.17) * mm});
            skLineSegment(sketch, "E25.10.0.22", {"start": v(2.38, -37.87) * mm, "end": v(1.93, -37.87) * mm});
            skLineSegment(sketch, "E25.10.0.23", {"start": v(5.43, -39.87) * mm, "end": v(5.43, -40.37) * mm});
            skLineSegment(sketch, "E25.10.0.24", {"start": v(4.43, -38.17) * mm, "end": v(4.43, -38.67) * mm});
            skLineSegment(sketch, "E25.10.0.25", {"start": v(6.88, -38.67) * mm, "end": v(6.43, -38.67) * mm});
            skLineSegment(sketch, "E25.10.0.26", {"start": v(6.43, -38.17) * mm, "end": v(6.43, -38.67) * mm});
            skLineSegment(sketch, "E25.10.0.27", {"start": v(4.88, -38.67) * mm, "end": v(4.43, -38.67) * mm});
            skLineSegment(sketch, "E25.10.0.28", {"start": v(0.93, -35.67) * mm, "end": v(0.93, -36.17) * mm});
            skLineSegment(sketch, "E25.10.0.29", {"start": v(1.93, -37.37) * mm, "end": v(1.93, -37.87) * mm});
            skPoint(sketch, "E25.11.0.0", {"position": v(-4.84, -37.37) * mm});
            skPoint(sketch, "E25.11.0.1", {"position": v(-2.34, -38.67) * mm});
            skPoint(sketch, "E25.11.0.2", {"position": v(-5.84, -36.17) * mm});
            skPoint(sketch, "E25.11.0.3", {"position": v(-1.34, -39.87) * mm});
            skPoint(sketch, "E25.11.0.4", {"position": v(-0.34, -38.67) * mm});
            skPoint(sketch, "E25.11.0.5", {"position": v(-3.84, -36.17) * mm});
            skLineSegment(sketch, "E25.11.0.6", {"start": v(-1.12, -40.37) * mm, "end": v(-1.57, -40.37) * mm});
            skLineSegment(sketch, "E25.11.0.7", {"start": v(-1.12, -39.87) * mm, "end": v(-1.12, -40.37) * mm});
            skLineSegment(sketch, "E25.11.0.8", {"start": v(-2.12, -38.17) * mm, "end": v(-2.57, -38.17) * mm});
            skLineSegment(sketch, "E25.11.0.9", {"start": v(-3.62, -36.17) * mm, "end": v(-4.07, -36.17) * mm});
            skLineSegment(sketch, "E25.11.0.10", {"start": v(-0.12, -38.17) * mm, "end": v(-0.57, -38.17) * mm});
            skLineSegment(sketch, "E25.11.0.11", {"start": v(-5.62, -35.67) * mm, "end": v(-6.07, -35.67) * mm});
            skLineSegment(sketch, "E25.11.0.12", {"start": v(-5.62, -36.17) * mm, "end": v(-6.07, -36.17) * mm});
            skLineSegment(sketch, "E25.11.0.13", {"start": v(-4.62, -37.37) * mm, "end": v(-4.62, -37.87) * mm});
            skLineSegment(sketch, "E25.11.0.14", {"start": v(-1.12, -39.87) * mm, "end": v(-1.57, -39.87) * mm});
            skLineSegment(sketch, "E25.11.0.15", {"start": v(-3.62, -35.67) * mm, "end": v(-3.62, -36.17) * mm});
            skLineSegment(sketch, "E25.11.0.16", {"start": v(-5.62, -35.67) * mm, "end": v(-5.62, -36.17) * mm});
            skLineSegment(sketch, "E25.11.0.17", {"start": v(-2.12, -38.17) * mm, "end": v(-2.12, -38.67) * mm});
            skLineSegment(sketch, "E25.11.0.18", {"start": v(-3.62, -35.67) * mm, "end": v(-4.07, -35.67) * mm});
            skLineSegment(sketch, "E25.11.0.19", {"start": v(-0.12, -38.17) * mm, "end": v(-0.12, -38.67) * mm});
            skLineSegment(sketch, "E25.11.0.20", {"start": v(-4.62, -37.37) * mm, "end": v(-5.07, -37.37) * mm});
            skLineSegment(sketch, "E25.11.0.21", {"start": v(-4.07, -35.67) * mm, "end": v(-4.07, -36.17) * mm});
            skLineSegment(sketch, "E25.11.0.22", {"start": v(-4.62, -37.87) * mm, "end": v(-5.07, -37.87) * mm});
            skLineSegment(sketch, "E25.11.0.23", {"start": v(-1.57, -39.87) * mm, "end": v(-1.57, -40.37) * mm});
            skLineSegment(sketch, "E25.11.0.24", {"start": v(-2.57, -38.17) * mm, "end": v(-2.57, -38.67) * mm});
            skLineSegment(sketch, "E25.11.0.25", {"start": v(-0.12, -38.67) * mm, "end": v(-0.57, -38.67) * mm});
            skLineSegment(sketch, "E25.11.0.26", {"start": v(-0.57, -38.17) * mm, "end": v(-0.57, -38.67) * mm});
            skLineSegment(sketch, "E25.11.0.27", {"start": v(-2.12, -38.67) * mm, "end": v(-2.57, -38.67) * mm});
            skLineSegment(sketch, "E25.11.0.28", {"start": v(-6.07, -35.67) * mm, "end": v(-6.07, -36.17) * mm});
            skLineSegment(sketch, "E25.11.0.29", {"start": v(-5.07, -37.37) * mm, "end": v(-5.07, -37.87) * mm});
            skPoint(sketch, "E25.12.0.0", {"position": v(-11.84, -37.37) * mm});
            skPoint(sketch, "E25.12.0.1", {"position": v(-9.34, -38.67) * mm});
            skPoint(sketch, "E25.12.0.2", {"position": v(-12.84, -36.17) * mm});
            skPoint(sketch, "E25.12.0.3", {"position": v(-8.34, -39.87) * mm});
            skPoint(sketch, "E25.12.0.4", {"position": v(-7.34, -38.67) * mm});
            skPoint(sketch, "E25.12.0.5", {"position": v(-10.84, -36.17) * mm});
            skLineSegment(sketch, "E25.12.0.6", {"start": v(-8.12, -40.37) * mm, "end": v(-8.57, -40.37) * mm});
            skLineSegment(sketch, "E25.12.0.7", {"start": v(-8.12, -39.87) * mm, "end": v(-8.12, -40.37) * mm});
            skLineSegment(sketch, "E25.12.0.8", {"start": v(-9.12, -38.17) * mm, "end": v(-9.57, -38.17) * mm});
            skLineSegment(sketch, "E25.12.0.9", {"start": v(-10.62, -36.17) * mm, "end": v(-11.07, -36.17) * mm});
            skLineSegment(sketch, "E25.12.0.10", {"start": v(-7.12, -38.17) * mm, "end": v(-7.57, -38.17) * mm});
            skLineSegment(sketch, "E25.12.0.11", {"start": v(-12.62, -35.67) * mm, "end": v(-13.07, -35.67) * mm});
            skLineSegment(sketch, "E25.12.0.12", {"start": v(-12.62, -36.17) * mm, "end": v(-13.07, -36.17) * mm});
            skLineSegment(sketch, "E25.12.0.13", {"start": v(-11.62, -37.37) * mm, "end": v(-11.62, -37.87) * mm});
            skLineSegment(sketch, "E25.12.0.14", {"start": v(-8.12, -39.87) * mm, "end": v(-8.57, -39.87) * mm});
            skLineSegment(sketch, "E25.12.0.15", {"start": v(-10.62, -35.67) * mm, "end": v(-10.62, -36.17) * mm});
            skLineSegment(sketch, "E25.12.0.16", {"start": v(-12.62, -35.67) * mm, "end": v(-12.62, -36.17) * mm});
            skLineSegment(sketch, "E25.12.0.17", {"start": v(-9.12, -38.17) * mm, "end": v(-9.12, -38.67) * mm});
            skLineSegment(sketch, "E25.12.0.18", {"start": v(-10.62, -35.67) * mm, "end": v(-11.07, -35.67) * mm});
            skLineSegment(sketch, "E25.12.0.19", {"start": v(-7.12, -38.17) * mm, "end": v(-7.12, -38.67) * mm});
            skLineSegment(sketch, "E25.12.0.20", {"start": v(-11.62, -37.37) * mm, "end": v(-12.07, -37.37) * mm});
            skLineSegment(sketch, "E25.12.0.21", {"start": v(-11.07, -35.67) * mm, "end": v(-11.07, -36.17) * mm});
            skLineSegment(sketch, "E25.12.0.22", {"start": v(-11.62, -37.87) * mm, "end": v(-12.07, -37.87) * mm});
            skLineSegment(sketch, "E25.12.0.23", {"start": v(-8.57, -39.87) * mm, "end": v(-8.57, -40.37) * mm});
            skLineSegment(sketch, "E25.12.0.24", {"start": v(-9.57, -38.17) * mm, "end": v(-9.57, -38.67) * mm});
            skLineSegment(sketch, "E25.12.0.25", {"start": v(-7.12, -38.67) * mm, "end": v(-7.57, -38.67) * mm});
            skLineSegment(sketch, "E25.12.0.26", {"start": v(-7.57, -38.17) * mm, "end": v(-7.57, -38.67) * mm});
            skLineSegment(sketch, "E25.12.0.27", {"start": v(-9.12, -38.67) * mm, "end": v(-9.57, -38.67) * mm});
            skLineSegment(sketch, "E25.12.0.28", {"start": v(-13.07, -35.67) * mm, "end": v(-13.07, -36.17) * mm});
            skLineSegment(sketch, "E25.12.0.29", {"start": v(-12.07, -37.37) * mm, "end": v(-12.07, -37.87) * mm});
            skPoint(sketch, "E25.13.0.0", {"position": v(-18.84, -37.37) * mm});
            skPoint(sketch, "E25.13.0.1", {"position": v(-16.34, -38.67) * mm});
            skPoint(sketch, "E25.13.0.2", {"position": v(-19.84, -36.17) * mm});
            skPoint(sketch, "E25.13.0.3", {"position": v(-15.34, -39.87) * mm});
            skPoint(sketch, "E25.13.0.4", {"position": v(-14.34, -38.67) * mm});
            skPoint(sketch, "E25.13.0.5", {"position": v(-17.84, -36.17) * mm});
            skLineSegment(sketch, "E25.13.0.6", {"start": v(-15.12, -40.37) * mm, "end": v(-15.57, -40.37) * mm});
            skLineSegment(sketch, "E25.13.0.7", {"start": v(-15.12, -39.87) * mm, "end": v(-15.12, -40.37) * mm});
            skLineSegment(sketch, "E25.13.0.8", {"start": v(-16.12, -38.17) * mm, "end": v(-16.57, -38.17) * mm});
            skLineSegment(sketch, "E25.13.0.9", {"start": v(-17.62, -36.17) * mm, "end": v(-18.07, -36.17) * mm});
            skLineSegment(sketch, "E25.13.0.10", {"start": v(-14.12, -38.17) * mm, "end": v(-14.57, -38.17) * mm});
            skLineSegment(sketch, "E25.13.0.11", {"start": v(-19.62, -35.67) * mm, "end": v(-20.07, -35.67) * mm});
            skLineSegment(sketch, "E25.13.0.12", {"start": v(-19.62, -36.17) * mm, "end": v(-20.07, -36.17) * mm});
            skLineSegment(sketch, "E25.13.0.13", {"start": v(-18.62, -37.37) * mm, "end": v(-18.62, -37.87) * mm});
            skLineSegment(sketch, "E25.13.0.14", {"start": v(-15.12, -39.87) * mm, "end": v(-15.57, -39.87) * mm});
            skLineSegment(sketch, "E25.13.0.15", {"start": v(-17.62, -35.67) * mm, "end": v(-17.62, -36.17) * mm});
            skLineSegment(sketch, "E25.13.0.16", {"start": v(-19.62, -35.67) * mm, "end": v(-19.62, -36.17) * mm});
            skLineSegment(sketch, "E25.13.0.17", {"start": v(-16.12, -38.17) * mm, "end": v(-16.12, -38.67) * mm});
            skLineSegment(sketch, "E25.13.0.18", {"start": v(-17.62, -35.67) * mm, "end": v(-18.07, -35.67) * mm});
            skLineSegment(sketch, "E25.13.0.19", {"start": v(-14.12, -38.17) * mm, "end": v(-14.12, -38.67) * mm});
            skLineSegment(sketch, "E25.13.0.20", {"start": v(-18.62, -37.37) * mm, "end": v(-19.07, -37.37) * mm});
            skLineSegment(sketch, "E25.13.0.21", {"start": v(-18.07, -35.67) * mm, "end": v(-18.07, -36.17) * mm});
            skLineSegment(sketch, "E25.13.0.22", {"start": v(-18.62, -37.87) * mm, "end": v(-19.07, -37.87) * mm});
            skLineSegment(sketch, "E25.13.0.23", {"start": v(-15.57, -39.87) * mm, "end": v(-15.57, -40.37) * mm});
            skLineSegment(sketch, "E25.13.0.24", {"start": v(-16.57, -38.17) * mm, "end": v(-16.57, -38.67) * mm});
            skLineSegment(sketch, "E25.13.0.25", {"start": v(-14.12, -38.67) * mm, "end": v(-14.57, -38.67) * mm});
            skLineSegment(sketch, "E25.13.0.26", {"start": v(-14.57, -38.17) * mm, "end": v(-14.57, -38.67) * mm});
            skLineSegment(sketch, "E25.13.0.27", {"start": v(-16.12, -38.67) * mm, "end": v(-16.57, -38.67) * mm});
            skLineSegment(sketch, "E25.13.0.28", {"start": v(-20.07, -35.67) * mm, "end": v(-20.07, -36.17) * mm});
            skLineSegment(sketch, "E25.13.0.29", {"start": v(-19.07, -37.37) * mm, "end": v(-19.07, -37.87) * mm});
            skPoint(sketch, "E25.14.0.0", {"position": v(-25.84, -37.37) * mm});
            skPoint(sketch, "E25.14.0.1", {"position": v(-23.34, -38.67) * mm});
            skPoint(sketch, "E25.14.0.2", {"position": v(-26.84, -36.17) * mm});
            skPoint(sketch, "E25.14.0.3", {"position": v(-22.34, -39.87) * mm});
            skPoint(sketch, "E25.14.0.4", {"position": v(-21.34, -38.67) * mm});
            skPoint(sketch, "E25.14.0.5", {"position": v(-24.84, -36.17) * mm});
            skLineSegment(sketch, "E25.14.0.6", {"start": v(-22.12, -40.37) * mm, "end": v(-22.57, -40.37) * mm});
            skLineSegment(sketch, "E25.14.0.7", {"start": v(-22.12, -39.87) * mm, "end": v(-22.12, -40.37) * mm});
            skLineSegment(sketch, "E25.14.0.8", {"start": v(-23.12, -38.17) * mm, "end": v(-23.57, -38.17) * mm});
            skLineSegment(sketch, "E25.14.0.9", {"start": v(-24.62, -36.17) * mm, "end": v(-25.07, -36.17) * mm});
            skLineSegment(sketch, "E25.14.0.10", {"start": v(-21.12, -38.17) * mm, "end": v(-21.57, -38.17) * mm});
            skLineSegment(sketch, "E25.14.0.11", {"start": v(-26.62, -35.67) * mm, "end": v(-27.07, -35.67) * mm});
            skLineSegment(sketch, "E25.14.0.12", {"start": v(-26.62, -36.17) * mm, "end": v(-27.07, -36.17) * mm});
            skLineSegment(sketch, "E25.14.0.13", {"start": v(-25.62, -37.37) * mm, "end": v(-25.62, -37.87) * mm});
            skLineSegment(sketch, "E25.14.0.14", {"start": v(-22.12, -39.87) * mm, "end": v(-22.57, -39.87) * mm});
            skLineSegment(sketch, "E25.14.0.15", {"start": v(-24.62, -35.67) * mm, "end": v(-24.62, -36.17) * mm});
            skLineSegment(sketch, "E25.14.0.16", {"start": v(-26.62, -35.67) * mm, "end": v(-26.62, -36.17) * mm});
            skLineSegment(sketch, "E25.14.0.17", {"start": v(-23.12, -38.17) * mm, "end": v(-23.12, -38.67) * mm});
            skLineSegment(sketch, "E25.14.0.18", {"start": v(-24.62, -35.67) * mm, "end": v(-25.07, -35.67) * mm});
            skLineSegment(sketch, "E25.14.0.19", {"start": v(-21.12, -38.17) * mm, "end": v(-21.12, -38.67) * mm});
            skLineSegment(sketch, "E25.14.0.20", {"start": v(-25.62, -37.37) * mm, "end": v(-26.07, -37.37) * mm});
            skLineSegment(sketch, "E25.14.0.21", {"start": v(-25.07, -35.67) * mm, "end": v(-25.07, -36.17) * mm});
            skLineSegment(sketch, "E25.14.0.22", {"start": v(-25.62, -37.87) * mm, "end": v(-26.07, -37.87) * mm});
            skLineSegment(sketch, "E25.14.0.23", {"start": v(-22.57, -39.87) * mm, "end": v(-22.57, -40.37) * mm});
            skLineSegment(sketch, "E25.14.0.24", {"start": v(-23.57, -38.17) * mm, "end": v(-23.57, -38.67) * mm});
            skLineSegment(sketch, "E25.14.0.25", {"start": v(-21.12, -38.67) * mm, "end": v(-21.57, -38.67) * mm});
            skLineSegment(sketch, "E25.14.0.26", {"start": v(-21.57, -38.17) * mm, "end": v(-21.57, -38.67) * mm});
            skLineSegment(sketch, "E25.14.0.27", {"start": v(-23.12, -38.67) * mm, "end": v(-23.57, -38.67) * mm});
            skLineSegment(sketch, "E25.14.0.28", {"start": v(-27.07, -35.67) * mm, "end": v(-27.07, -36.17) * mm});
            skLineSegment(sketch, "E25.14.0.29", {"start": v(-26.07, -37.37) * mm, "end": v(-26.07, -37.87) * mm});
            skLineSegment(sketch, "E25.direction1", {"start": v(71.93, -37.87) * mm, "end": v(64.93, -37.87) * mm, "construction": true});
            skLineSegment(sketch, "E26.bottom", {"start": v(75.16, -41.87) * mm, "end": v(76.16, -41.87) * mm});
            skLineSegment(sketch, "E26.top", {"start": v(75.16, -41.47) * mm, "end": v(76.16, -41.47) * mm});
            skLineSegment(sketch, "E26.left", {"start": v(75.16, -41.87) * mm, "end": v(75.16, -41.47) * mm});
            skLineSegment(sketch, "E26.right", {"start": v(76.16, -41.87) * mm, "end": v(76.16, -41.47) * mm});
            skLineSegment(sketch, "E27.bottom", {"start": v(75.16, -43.47) * mm, "end": v(76.16, -43.47) * mm});
            skLineSegment(sketch, "E27.top", {"start": v(75.16, -43.07) * mm, "end": v(76.16, -43.07) * mm});
            skLineSegment(sketch, "E27.left", {"start": v(75.16, -43.47) * mm, "end": v(75.16, -43.07) * mm});
            skLineSegment(sketch, "E27.right", {"start": v(76.16, -43.47) * mm, "end": v(76.16, -43.07) * mm});
            skLineSegment(sketch, "E28.1.0.0", {"start": v(71.66, -41.47) * mm, "end": v(72.66, -41.47) * mm});
            skLineSegment(sketch, "E28.1.0.1", {"start": v(72.66, -41.87) * mm, "end": v(72.66, -41.47) * mm});
            skLineSegment(sketch, "E28.1.0.2", {"start": v(71.66, -41.87) * mm, "end": v(71.66, -41.47) * mm});
            skLineSegment(sketch, "E28.1.0.3", {"start": v(71.66, -43.07) * mm, "end": v(72.66, -43.07) * mm});
            skLineSegment(sketch, "E28.1.0.4", {"start": v(71.66, -43.47) * mm, "end": v(72.66, -43.47) * mm});
            skLineSegment(sketch, "E28.1.0.5", {"start": v(72.66, -43.47) * mm, "end": v(72.66, -43.07) * mm});
            skLineSegment(sketch, "E28.1.0.6", {"start": v(71.66, -41.87) * mm, "end": v(72.66, -41.87) * mm});
            skLineSegment(sketch, "E28.1.0.7", {"start": v(71.66, -43.47) * mm, "end": v(71.66, -43.07) * mm});
            skLineSegment(sketch, "E28.2.0.0", {"start": v(68.16, -41.47) * mm, "end": v(69.16, -41.47) * mm});
            skLineSegment(sketch, "E28.2.0.1", {"start": v(69.16, -41.87) * mm, "end": v(69.16, -41.47) * mm});
            skLineSegment(sketch, "E28.2.0.2", {"start": v(68.16, -41.87) * mm, "end": v(68.16, -41.47) * mm});
            skLineSegment(sketch, "E28.2.0.3", {"start": v(68.16, -43.07) * mm, "end": v(69.16, -43.07) * mm});
            skLineSegment(sketch, "E28.2.0.4", {"start": v(68.16, -43.47) * mm, "end": v(69.16, -43.47) * mm});
            skLineSegment(sketch, "E28.2.0.5", {"start": v(69.16, -43.47) * mm, "end": v(69.16, -43.07) * mm});
            skLineSegment(sketch, "E28.2.0.6", {"start": v(68.16, -41.87) * mm, "end": v(69.16, -41.87) * mm});
            skLineSegment(sketch, "E28.2.0.7", {"start": v(68.16, -43.47) * mm, "end": v(68.16, -43.07) * mm});
            skLineSegment(sketch, "E28.3.0.0", {"start": v(64.66, -41.47) * mm, "end": v(65.66, -41.47) * mm});
            skLineSegment(sketch, "E28.3.0.1", {"start": v(65.66, -41.87) * mm, "end": v(65.66, -41.47) * mm});
            skLineSegment(sketch, "E28.3.0.2", {"start": v(64.66, -41.87) * mm, "end": v(64.66, -41.47) * mm});
            skLineSegment(sketch, "E28.3.0.3", {"start": v(64.66, -43.07) * mm, "end": v(65.66, -43.07) * mm});
            skLineSegment(sketch, "E28.3.0.4", {"start": v(64.66, -43.47) * mm, "end": v(65.66, -43.47) * mm});
            skLineSegment(sketch, "E28.3.0.5", {"start": v(65.66, -43.47) * mm, "end": v(65.66, -43.07) * mm});
            skLineSegment(sketch, "E28.3.0.6", {"start": v(64.66, -41.87) * mm, "end": v(65.66, -41.87) * mm});
            skLineSegment(sketch, "E28.3.0.7", {"start": v(64.66, -43.47) * mm, "end": v(64.66, -43.07) * mm});
            skLineSegment(sketch, "E28.4.0.0", {"start": v(61.16, -41.47) * mm, "end": v(62.16, -41.47) * mm});
            skLineSegment(sketch, "E28.4.0.1", {"start": v(62.16, -41.87) * mm, "end": v(62.16, -41.47) * mm});
            skLineSegment(sketch, "E28.4.0.2", {"start": v(61.16, -41.87) * mm, "end": v(61.16, -41.47) * mm});
            skLineSegment(sketch, "E28.4.0.3", {"start": v(61.16, -43.07) * mm, "end": v(62.16, -43.07) * mm});
            skLineSegment(sketch, "E28.4.0.4", {"start": v(61.16, -43.47) * mm, "end": v(62.16, -43.47) * mm});
            skLineSegment(sketch, "E28.4.0.5", {"start": v(62.16, -43.47) * mm, "end": v(62.16, -43.07) * mm});
            skLineSegment(sketch, "E28.4.0.6", {"start": v(61.16, -41.87) * mm, "end": v(62.16, -41.87) * mm});
            skLineSegment(sketch, "E28.4.0.7", {"start": v(61.16, -43.47) * mm, "end": v(61.16, -43.07) * mm});
            skLineSegment(sketch, "E28.5.0.0", {"start": v(57.66, -41.47) * mm, "end": v(58.66, -41.47) * mm});
            skLineSegment(sketch, "E28.5.0.1", {"start": v(58.66, -41.87) * mm, "end": v(58.66, -41.47) * mm});
            skLineSegment(sketch, "E28.5.0.2", {"start": v(57.66, -41.87) * mm, "end": v(57.66, -41.47) * mm});
            skLineSegment(sketch, "E28.5.0.3", {"start": v(57.66, -43.07) * mm, "end": v(58.66, -43.07) * mm});
            skLineSegment(sketch, "E28.5.0.4", {"start": v(57.66, -43.47) * mm, "end": v(58.66, -43.47) * mm});
            skLineSegment(sketch, "E28.5.0.5", {"start": v(58.66, -43.47) * mm, "end": v(58.66, -43.07) * mm});
            skLineSegment(sketch, "E28.5.0.6", {"start": v(57.66, -41.87) * mm, "end": v(58.66, -41.87) * mm});
            skLineSegment(sketch, "E28.5.0.7", {"start": v(57.66, -43.47) * mm, "end": v(57.66, -43.07) * mm});
            skLineSegment(sketch, "E28.6.0.0", {"start": v(54.16, -41.47) * mm, "end": v(55.16, -41.47) * mm});
            skLineSegment(sketch, "E28.6.0.1", {"start": v(55.16, -41.87) * mm, "end": v(55.16, -41.47) * mm});
            skLineSegment(sketch, "E28.6.0.2", {"start": v(54.16, -41.87) * mm, "end": v(54.16, -41.47) * mm});
            skLineSegment(sketch, "E28.6.0.3", {"start": v(54.16, -43.07) * mm, "end": v(55.16, -43.07) * mm});
            skLineSegment(sketch, "E28.6.0.4", {"start": v(54.16, -43.47) * mm, "end": v(55.16, -43.47) * mm});
            skLineSegment(sketch, "E28.6.0.5", {"start": v(55.16, -43.47) * mm, "end": v(55.16, -43.07) * mm});
            skLineSegment(sketch, "E28.6.0.6", {"start": v(54.16, -41.87) * mm, "end": v(55.16, -41.87) * mm});
            skLineSegment(sketch, "E28.6.0.7", {"start": v(54.16, -43.47) * mm, "end": v(54.16, -43.07) * mm});
            skLineSegment(sketch, "E28.7.0.0", {"start": v(50.66, -41.47) * mm, "end": v(51.66, -41.47) * mm});
            skLineSegment(sketch, "E28.7.0.1", {"start": v(51.66, -41.87) * mm, "end": v(51.66, -41.47) * mm});
            skLineSegment(sketch, "E28.7.0.2", {"start": v(50.66, -41.87) * mm, "end": v(50.66, -41.47) * mm});
            skLineSegment(sketch, "E28.7.0.3", {"start": v(50.66, -43.07) * mm, "end": v(51.66, -43.07) * mm});
            skLineSegment(sketch, "E28.7.0.4", {"start": v(50.66, -43.47) * mm, "end": v(51.66, -43.47) * mm});
            skLineSegment(sketch, "E28.7.0.5", {"start": v(51.66, -43.47) * mm, "end": v(51.66, -43.07) * mm});
            skLineSegment(sketch, "E28.7.0.6", {"start": v(50.66, -41.87) * mm, "end": v(51.66, -41.87) * mm});
            skLineSegment(sketch, "E28.7.0.7", {"start": v(50.66, -43.47) * mm, "end": v(50.66, -43.07) * mm});
            skLineSegment(sketch, "E28.8.0.0", {"start": v(47.16, -41.47) * mm, "end": v(48.16, -41.47) * mm});
            skLineSegment(sketch, "E28.8.0.1", {"start": v(48.16, -41.87) * mm, "end": v(48.16, -41.47) * mm});
            skLineSegment(sketch, "E28.8.0.2", {"start": v(47.16, -41.87) * mm, "end": v(47.16, -41.47) * mm});
            skLineSegment(sketch, "E28.8.0.3", {"start": v(47.16, -43.07) * mm, "end": v(48.16, -43.07) * mm});
            skLineSegment(sketch, "E28.8.0.4", {"start": v(47.16, -43.47) * mm, "end": v(48.16, -43.47) * mm});
            skLineSegment(sketch, "E28.8.0.5", {"start": v(48.16, -43.47) * mm, "end": v(48.16, -43.07) * mm});
            skLineSegment(sketch, "E28.8.0.6", {"start": v(47.16, -41.87) * mm, "end": v(48.16, -41.87) * mm});
            skLineSegment(sketch, "E28.8.0.7", {"start": v(47.16, -43.47) * mm, "end": v(47.16, -43.07) * mm});
            skLineSegment(sketch, "E28.9.0.0", {"start": v(43.66, -41.47) * mm, "end": v(44.66, -41.47) * mm});
            skLineSegment(sketch, "E28.9.0.1", {"start": v(44.66, -41.87) * mm, "end": v(44.66, -41.47) * mm});
            skLineSegment(sketch, "E28.9.0.2", {"start": v(43.66, -41.87) * mm, "end": v(43.66, -41.47) * mm});
            skLineSegment(sketch, "E28.9.0.3", {"start": v(43.66, -43.07) * mm, "end": v(44.66, -43.07) * mm});
            skLineSegment(sketch, "E28.9.0.4", {"start": v(43.66, -43.47) * mm, "end": v(44.66, -43.47) * mm});
            skLineSegment(sketch, "E28.9.0.5", {"start": v(44.66, -43.47) * mm, "end": v(44.66, -43.07) * mm});
            skLineSegment(sketch, "E28.9.0.6", {"start": v(43.66, -41.87) * mm, "end": v(44.66, -41.87) * mm});
            skLineSegment(sketch, "E28.9.0.7", {"start": v(43.66, -43.47) * mm, "end": v(43.66, -43.07) * mm});
            skLineSegment(sketch, "E28.10.0.0", {"start": v(40.16, -41.47) * mm, "end": v(41.16, -41.47) * mm});
            skLineSegment(sketch, "E28.10.0.1", {"start": v(41.16, -41.87) * mm, "end": v(41.16, -41.47) * mm});
            skLineSegment(sketch, "E28.10.0.2", {"start": v(40.16, -41.87) * mm, "end": v(40.16, -41.47) * mm});
            skLineSegment(sketch, "E28.10.0.3", {"start": v(40.16, -43.07) * mm, "end": v(41.16, -43.07) * mm});
            skLineSegment(sketch, "E28.10.0.4", {"start": v(40.16, -43.47) * mm, "end": v(41.16, -43.47) * mm});
            skLineSegment(sketch, "E28.10.0.5", {"start": v(41.16, -43.47) * mm, "end": v(41.16, -43.07) * mm});
            skLineSegment(sketch, "E28.10.0.6", {"start": v(40.16, -41.87) * mm, "end": v(41.16, -41.87) * mm});
            skLineSegment(sketch, "E28.10.0.7", {"start": v(40.16, -43.47) * mm, "end": v(40.16, -43.07) * mm});
            skLineSegment(sketch, "E28.11.0.0", {"start": v(36.66, -41.47) * mm, "end": v(37.66, -41.47) * mm});
            skLineSegment(sketch, "E28.11.0.1", {"start": v(37.66, -41.87) * mm, "end": v(37.66, -41.47) * mm});
            skLineSegment(sketch, "E28.11.0.2", {"start": v(36.66, -41.87) * mm, "end": v(36.66, -41.47) * mm});
            skLineSegment(sketch, "E28.11.0.3", {"start": v(36.66, -43.07) * mm, "end": v(37.66, -43.07) * mm});
            skLineSegment(sketch, "E28.11.0.4", {"start": v(36.66, -43.47) * mm, "end": v(37.66, -43.47) * mm});
            skLineSegment(sketch, "E28.11.0.5", {"start": v(37.66, -43.47) * mm, "end": v(37.66, -43.07) * mm});
            skLineSegment(sketch, "E28.11.0.6", {"start": v(36.66, -41.87) * mm, "end": v(37.66, -41.87) * mm});
            skLineSegment(sketch, "E28.11.0.7", {"start": v(36.66, -43.47) * mm, "end": v(36.66, -43.07) * mm});
            skLineSegment(sketch, "E28.12.0.0", {"start": v(33.16, -41.47) * mm, "end": v(34.16, -41.47) * mm});
            skLineSegment(sketch, "E28.12.0.1", {"start": v(34.16, -41.87) * mm, "end": v(34.16, -41.47) * mm});
            skLineSegment(sketch, "E28.12.0.2", {"start": v(33.16, -41.87) * mm, "end": v(33.16, -41.47) * mm});
            skLineSegment(sketch, "E28.12.0.3", {"start": v(33.16, -43.07) * mm, "end": v(34.16, -43.07) * mm});
            skLineSegment(sketch, "E28.12.0.4", {"start": v(33.16, -43.47) * mm, "end": v(34.16, -43.47) * mm});
            skLineSegment(sketch, "E28.12.0.5", {"start": v(34.16, -43.47) * mm, "end": v(34.16, -43.07) * mm});
            skLineSegment(sketch, "E28.12.0.6", {"start": v(33.16, -41.87) * mm, "end": v(34.16, -41.87) * mm});
            skLineSegment(sketch, "E28.12.0.7", {"start": v(33.16, -43.47) * mm, "end": v(33.16, -43.07) * mm});
            skLineSegment(sketch, "E28.13.0.0", {"start": v(29.66, -41.47) * mm, "end": v(30.66, -41.47) * mm});
            skLineSegment(sketch, "E28.13.0.1", {"start": v(30.66, -41.87) * mm, "end": v(30.66, -41.47) * mm});
            skLineSegment(sketch, "E28.13.0.2", {"start": v(29.66, -41.87) * mm, "end": v(29.66, -41.47) * mm});
            skLineSegment(sketch, "E28.13.0.3", {"start": v(29.66, -43.07) * mm, "end": v(30.66, -43.07) * mm});
            skLineSegment(sketch, "E28.13.0.4", {"start": v(29.66, -43.47) * mm, "end": v(30.66, -43.47) * mm});
            skLineSegment(sketch, "E28.13.0.5", {"start": v(30.66, -43.47) * mm, "end": v(30.66, -43.07) * mm});
            skLineSegment(sketch, "E28.13.0.6", {"start": v(29.66, -41.87) * mm, "end": v(30.66, -41.87) * mm});
            skLineSegment(sketch, "E28.13.0.7", {"start": v(29.66, -43.47) * mm, "end": v(29.66, -43.07) * mm});
            skLineSegment(sketch, "E28.14.0.0", {"start": v(26.16, -41.47) * mm, "end": v(27.16, -41.47) * mm});
            skLineSegment(sketch, "E28.14.0.1", {"start": v(27.16, -41.87) * mm, "end": v(27.16, -41.47) * mm});
            skLineSegment(sketch, "E28.14.0.2", {"start": v(26.16, -41.87) * mm, "end": v(26.16, -41.47) * mm});
            skLineSegment(sketch, "E28.14.0.3", {"start": v(26.16, -43.07) * mm, "end": v(27.16, -43.07) * mm});
            skLineSegment(sketch, "E28.14.0.4", {"start": v(26.16, -43.47) * mm, "end": v(27.16, -43.47) * mm});
            skLineSegment(sketch, "E28.14.0.5", {"start": v(27.16, -43.47) * mm, "end": v(27.16, -43.07) * mm});
            skLineSegment(sketch, "E28.14.0.6", {"start": v(26.16, -41.87) * mm, "end": v(27.16, -41.87) * mm});
            skLineSegment(sketch, "E28.14.0.7", {"start": v(26.16, -43.47) * mm, "end": v(26.16, -43.07) * mm});
            skLineSegment(sketch, "E28.15.0.0", {"start": v(22.66, -41.47) * mm, "end": v(23.66, -41.47) * mm});
            skLineSegment(sketch, "E28.15.0.1", {"start": v(23.66, -41.87) * mm, "end": v(23.66, -41.47) * mm});
            skLineSegment(sketch, "E28.15.0.2", {"start": v(22.66, -41.87) * mm, "end": v(22.66, -41.47) * mm});
            skLineSegment(sketch, "E28.15.0.3", {"start": v(22.66, -43.07) * mm, "end": v(23.66, -43.07) * mm});
            skLineSegment(sketch, "E28.15.0.4", {"start": v(22.66, -43.47) * mm, "end": v(23.66, -43.47) * mm});
            skLineSegment(sketch, "E28.15.0.5", {"start": v(23.66, -43.47) * mm, "end": v(23.66, -43.07) * mm});
            skLineSegment(sketch, "E28.15.0.6", {"start": v(22.66, -41.87) * mm, "end": v(23.66, -41.87) * mm});
            skLineSegment(sketch, "E28.15.0.7", {"start": v(22.66, -43.47) * mm, "end": v(22.66, -43.07) * mm});
            skLineSegment(sketch, "E28.16.0.0", {"start": v(19.16, -41.47) * mm, "end": v(20.16, -41.47) * mm});
            skLineSegment(sketch, "E28.16.0.1", {"start": v(20.16, -41.87) * mm, "end": v(20.16, -41.47) * mm});
            skLineSegment(sketch, "E28.16.0.2", {"start": v(19.16, -41.87) * mm, "end": v(19.16, -41.47) * mm});
            skLineSegment(sketch, "E28.16.0.3", {"start": v(19.16, -43.07) * mm, "end": v(20.16, -43.07) * mm});
            skLineSegment(sketch, "E28.16.0.4", {"start": v(19.16, -43.47) * mm, "end": v(20.16, -43.47) * mm});
            skLineSegment(sketch, "E28.16.0.5", {"start": v(20.16, -43.47) * mm, "end": v(20.16, -43.07) * mm});
            skLineSegment(sketch, "E28.16.0.6", {"start": v(19.16, -41.87) * mm, "end": v(20.16, -41.87) * mm});
            skLineSegment(sketch, "E28.16.0.7", {"start": v(19.16, -43.47) * mm, "end": v(19.16, -43.07) * mm});
            skLineSegment(sketch, "E28.17.0.0", {"start": v(15.66, -41.47) * mm, "end": v(16.66, -41.47) * mm});
            skLineSegment(sketch, "E28.17.0.1", {"start": v(16.66, -41.87) * mm, "end": v(16.66, -41.47) * mm});
            skLineSegment(sketch, "E28.17.0.2", {"start": v(15.66, -41.87) * mm, "end": v(15.66, -41.47) * mm});
            skLineSegment(sketch, "E28.17.0.3", {"start": v(15.66, -43.07) * mm, "end": v(16.66, -43.07) * mm});
            skLineSegment(sketch, "E28.17.0.4", {"start": v(15.66, -43.47) * mm, "end": v(16.66, -43.47) * mm});
            skLineSegment(sketch, "E28.17.0.5", {"start": v(16.66, -43.47) * mm, "end": v(16.66, -43.07) * mm});
            skLineSegment(sketch, "E28.17.0.6", {"start": v(15.66, -41.87) * mm, "end": v(16.66, -41.87) * mm});
            skLineSegment(sketch, "E28.17.0.7", {"start": v(15.66, -43.47) * mm, "end": v(15.66, -43.07) * mm});
            skLineSegment(sketch, "E28.18.0.0", {"start": v(12.16, -41.47) * mm, "end": v(13.16, -41.47) * mm});
            skLineSegment(sketch, "E28.18.0.1", {"start": v(13.16, -41.87) * mm, "end": v(13.16, -41.47) * mm});
            skLineSegment(sketch, "E28.18.0.2", {"start": v(12.16, -41.87) * mm, "end": v(12.16, -41.47) * mm});
            skLineSegment(sketch, "E28.18.0.3", {"start": v(12.16, -43.07) * mm, "end": v(13.16, -43.07) * mm});
            skLineSegment(sketch, "E28.18.0.4", {"start": v(12.16, -43.47) * mm, "end": v(13.16, -43.47) * mm});
            skLineSegment(sketch, "E28.18.0.5", {"start": v(13.16, -43.47) * mm, "end": v(13.16, -43.07) * mm});
            skLineSegment(sketch, "E28.18.0.6", {"start": v(12.16, -41.87) * mm, "end": v(13.16, -41.87) * mm});
            skLineSegment(sketch, "E28.18.0.7", {"start": v(12.16, -43.47) * mm, "end": v(12.16, -43.07) * mm});
            skLineSegment(sketch, "E28.19.0.0", {"start": v(8.66, -41.47) * mm, "end": v(9.66, -41.47) * mm});
            skLineSegment(sketch, "E28.19.0.1", {"start": v(9.66, -41.87) * mm, "end": v(9.66, -41.47) * mm});
            skLineSegment(sketch, "E28.19.0.2", {"start": v(8.66, -41.87) * mm, "end": v(8.66, -41.47) * mm});
            skLineSegment(sketch, "E28.19.0.3", {"start": v(8.66, -43.07) * mm, "end": v(9.66, -43.07) * mm});
            skLineSegment(sketch, "E28.19.0.4", {"start": v(8.66, -43.47) * mm, "end": v(9.66, -43.47) * mm});
            skLineSegment(sketch, "E28.19.0.5", {"start": v(9.66, -43.47) * mm, "end": v(9.66, -43.07) * mm});
            skLineSegment(sketch, "E28.19.0.6", {"start": v(8.66, -41.87) * mm, "end": v(9.66, -41.87) * mm});
            skLineSegment(sketch, "E28.19.0.7", {"start": v(8.66, -43.47) * mm, "end": v(8.66, -43.07) * mm});
            skLineSegment(sketch, "E28.20.0.0", {"start": v(5.16, -41.47) * mm, "end": v(6.16, -41.47) * mm});
            skLineSegment(sketch, "E28.20.0.1", {"start": v(6.16, -41.87) * mm, "end": v(6.16, -41.47) * mm});
            skLineSegment(sketch, "E28.20.0.2", {"start": v(5.16, -41.87) * mm, "end": v(5.16, -41.47) * mm});
            skLineSegment(sketch, "E28.20.0.3", {"start": v(5.16, -43.07) * mm, "end": v(6.16, -43.07) * mm});
            skLineSegment(sketch, "E28.20.0.4", {"start": v(5.16, -43.47) * mm, "end": v(6.16, -43.47) * mm});
            skLineSegment(sketch, "E28.20.0.5", {"start": v(6.16, -43.47) * mm, "end": v(6.16, -43.07) * mm});
            skLineSegment(sketch, "E28.20.0.6", {"start": v(5.16, -41.87) * mm, "end": v(6.16, -41.87) * mm});
            skLineSegment(sketch, "E28.20.0.7", {"start": v(5.16, -43.47) * mm, "end": v(5.16, -43.07) * mm});
            skLineSegment(sketch, "E28.21.0.0", {"start": v(1.66, -41.47) * mm, "end": v(2.66, -41.47) * mm});
            skLineSegment(sketch, "E28.21.0.1", {"start": v(2.66, -41.87) * mm, "end": v(2.66, -41.47) * mm});
            skLineSegment(sketch, "E28.21.0.2", {"start": v(1.66, -41.87) * mm, "end": v(1.66, -41.47) * mm});
            skLineSegment(sketch, "E28.21.0.3", {"start": v(1.66, -43.07) * mm, "end": v(2.66, -43.07) * mm});
            skLineSegment(sketch, "E28.21.0.4", {"start": v(1.66, -43.47) * mm, "end": v(2.66, -43.47) * mm});
            skLineSegment(sketch, "E28.21.0.5", {"start": v(2.66, -43.47) * mm, "end": v(2.66, -43.07) * mm});
            skLineSegment(sketch, "E28.21.0.6", {"start": v(1.66, -41.87) * mm, "end": v(2.66, -41.87) * mm});
            skLineSegment(sketch, "E28.21.0.7", {"start": v(1.66, -43.47) * mm, "end": v(1.66, -43.07) * mm});
            skLineSegment(sketch, "E28.22.0.0", {"start": v(-1.84, -41.47) * mm, "end": v(-0.84, -41.47) * mm});
            skLineSegment(sketch, "E28.22.0.1", {"start": v(-0.84, -41.87) * mm, "end": v(-0.84, -41.47) * mm});
            skLineSegment(sketch, "E28.22.0.2", {"start": v(-1.84, -41.87) * mm, "end": v(-1.84, -41.47) * mm});
            skLineSegment(sketch, "E28.22.0.3", {"start": v(-1.84, -43.07) * mm, "end": v(-0.84, -43.07) * mm});
            skLineSegment(sketch, "E28.22.0.4", {"start": v(-1.84, -43.47) * mm, "end": v(-0.84, -43.47) * mm});
            skLineSegment(sketch, "E28.22.0.5", {"start": v(-0.84, -43.47) * mm, "end": v(-0.84, -43.07) * mm});
            skLineSegment(sketch, "E28.22.0.6", {"start": v(-1.84, -41.87) * mm, "end": v(-0.84, -41.87) * mm});
            skLineSegment(sketch, "E28.22.0.7", {"start": v(-1.84, -43.47) * mm, "end": v(-1.84, -43.07) * mm});
            skLineSegment(sketch, "E28.23.0.0", {"start": v(-5.34, -41.47) * mm, "end": v(-4.34, -41.47) * mm});
            skLineSegment(sketch, "E28.23.0.1", {"start": v(-4.34, -41.87) * mm, "end": v(-4.34, -41.47) * mm});
            skLineSegment(sketch, "E28.23.0.2", {"start": v(-5.34, -41.87) * mm, "end": v(-5.34, -41.47) * mm});
            skLineSegment(sketch, "E28.23.0.3", {"start": v(-5.34, -43.07) * mm, "end": v(-4.34, -43.07) * mm});
            skLineSegment(sketch, "E28.23.0.4", {"start": v(-5.34, -43.47) * mm, "end": v(-4.34, -43.47) * mm});
            skLineSegment(sketch, "E28.23.0.5", {"start": v(-4.34, -43.47) * mm, "end": v(-4.34, -43.07) * mm});
            skLineSegment(sketch, "E28.23.0.6", {"start": v(-5.34, -41.87) * mm, "end": v(-4.34, -41.87) * mm});
            skLineSegment(sketch, "E28.23.0.7", {"start": v(-5.34, -43.47) * mm, "end": v(-5.34, -43.07) * mm});
            skLineSegment(sketch, "E28.24.0.0", {"start": v(-8.84, -41.47) * mm, "end": v(-7.84, -41.47) * mm});
            skLineSegment(sketch, "E28.24.0.1", {"start": v(-7.84, -41.87) * mm, "end": v(-7.84, -41.47) * mm});
            skLineSegment(sketch, "E28.24.0.2", {"start": v(-8.84, -41.87) * mm, "end": v(-8.84, -41.47) * mm});
            skLineSegment(sketch, "E28.24.0.3", {"start": v(-8.84, -43.07) * mm, "end": v(-7.84, -43.07) * mm});
            skLineSegment(sketch, "E28.24.0.4", {"start": v(-8.84, -43.47) * mm, "end": v(-7.84, -43.47) * mm});
            skLineSegment(sketch, "E28.24.0.5", {"start": v(-7.84, -43.47) * mm, "end": v(-7.84, -43.07) * mm});
            skLineSegment(sketch, "E28.24.0.6", {"start": v(-8.84, -41.87) * mm, "end": v(-7.84, -41.87) * mm});
            skLineSegment(sketch, "E28.24.0.7", {"start": v(-8.84, -43.47) * mm, "end": v(-8.84, -43.07) * mm});
            skLineSegment(sketch, "E28.25.0.0", {"start": v(-12.34, -41.47) * mm, "end": v(-11.34, -41.47) * mm});
            skLineSegment(sketch, "E28.25.0.1", {"start": v(-11.34, -41.87) * mm, "end": v(-11.34, -41.47) * mm});
            skLineSegment(sketch, "E28.25.0.2", {"start": v(-12.34, -41.87) * mm, "end": v(-12.34, -41.47) * mm});
            skLineSegment(sketch, "E28.25.0.3", {"start": v(-12.34, -43.07) * mm, "end": v(-11.34, -43.07) * mm});
            skLineSegment(sketch, "E28.25.0.4", {"start": v(-12.34, -43.47) * mm, "end": v(-11.34, -43.47) * mm});
            skLineSegment(sketch, "E28.25.0.5", {"start": v(-11.34, -43.47) * mm, "end": v(-11.34, -43.07) * mm});
            skLineSegment(sketch, "E28.25.0.6", {"start": v(-12.34, -41.87) * mm, "end": v(-11.34, -41.87) * mm});
            skLineSegment(sketch, "E28.25.0.7", {"start": v(-12.34, -43.47) * mm, "end": v(-12.34, -43.07) * mm});
            skLineSegment(sketch, "E28.26.0.0", {"start": v(-15.84, -41.47) * mm, "end": v(-14.84, -41.47) * mm});
            skLineSegment(sketch, "E28.26.0.1", {"start": v(-14.84, -41.87) * mm, "end": v(-14.84, -41.47) * mm});
            skLineSegment(sketch, "E28.26.0.2", {"start": v(-15.84, -41.87) * mm, "end": v(-15.84, -41.47) * mm});
            skLineSegment(sketch, "E28.26.0.3", {"start": v(-15.84, -43.07) * mm, "end": v(-14.84, -43.07) * mm});
            skLineSegment(sketch, "E28.26.0.4", {"start": v(-15.84, -43.47) * mm, "end": v(-14.84, -43.47) * mm});
            skLineSegment(sketch, "E28.26.0.5", {"start": v(-14.84, -43.47) * mm, "end": v(-14.84, -43.07) * mm});
            skLineSegment(sketch, "E28.26.0.6", {"start": v(-15.84, -41.87) * mm, "end": v(-14.84, -41.87) * mm});
            skLineSegment(sketch, "E28.26.0.7", {"start": v(-15.84, -43.47) * mm, "end": v(-15.84, -43.07) * mm});
            skLineSegment(sketch, "E28.27.0.0", {"start": v(-19.34, -41.47) * mm, "end": v(-18.34, -41.47) * mm});
            skLineSegment(sketch, "E28.27.0.1", {"start": v(-18.34, -41.87) * mm, "end": v(-18.34, -41.47) * mm});
            skLineSegment(sketch, "E28.27.0.2", {"start": v(-19.34, -41.87) * mm, "end": v(-19.34, -41.47) * mm});
            skLineSegment(sketch, "E28.27.0.3", {"start": v(-19.34, -43.07) * mm, "end": v(-18.34, -43.07) * mm});
            skLineSegment(sketch, "E28.27.0.4", {"start": v(-19.34, -43.47) * mm, "end": v(-18.34, -43.47) * mm});
            skLineSegment(sketch, "E28.27.0.5", {"start": v(-18.34, -43.47) * mm, "end": v(-18.34, -43.07) * mm});
            skLineSegment(sketch, "E28.27.0.6", {"start": v(-19.34, -41.87) * mm, "end": v(-18.34, -41.87) * mm});
            skLineSegment(sketch, "E28.27.0.7", {"start": v(-19.34, -43.47) * mm, "end": v(-19.34, -43.07) * mm});
            skLineSegment(sketch, "E28.28.0.0", {"start": v(-22.84, -41.47) * mm, "end": v(-21.84, -41.47) * mm});
            skLineSegment(sketch, "E28.28.0.1", {"start": v(-21.84, -41.87) * mm, "end": v(-21.84, -41.47) * mm});
            skLineSegment(sketch, "E28.28.0.2", {"start": v(-22.84, -41.87) * mm, "end": v(-22.84, -41.47) * mm});
            skLineSegment(sketch, "E28.28.0.3", {"start": v(-22.84, -43.07) * mm, "end": v(-21.84, -43.07) * mm});
            skLineSegment(sketch, "E28.28.0.4", {"start": v(-22.84, -43.47) * mm, "end": v(-21.84, -43.47) * mm});
            skLineSegment(sketch, "E28.28.0.5", {"start": v(-21.84, -43.47) * mm, "end": v(-21.84, -43.07) * mm});
            skLineSegment(sketch, "E28.28.0.6", {"start": v(-22.84, -41.87) * mm, "end": v(-21.84, -41.87) * mm});
            skLineSegment(sketch, "E28.28.0.7", {"start": v(-22.84, -43.47) * mm, "end": v(-22.84, -43.07) * mm});
            skLineSegment(sketch, "E28.29.0.0", {"start": v(-26.34, -41.47) * mm, "end": v(-25.34, -41.47) * mm});
            skLineSegment(sketch, "E28.29.0.1", {"start": v(-25.34, -41.87) * mm, "end": v(-25.34, -41.47) * mm});
            skLineSegment(sketch, "E28.29.0.2", {"start": v(-26.34, -41.87) * mm, "end": v(-26.34, -41.47) * mm});
            skLineSegment(sketch, "E28.29.0.3", {"start": v(-26.34, -43.07) * mm, "end": v(-25.34, -43.07) * mm});
            skLineSegment(sketch, "E28.29.0.4", {"start": v(-26.34, -43.47) * mm, "end": v(-25.34, -43.47) * mm});
            skLineSegment(sketch, "E28.29.0.5", {"start": v(-25.34, -43.47) * mm, "end": v(-25.34, -43.07) * mm});
            skLineSegment(sketch, "E28.29.0.6", {"start": v(-26.34, -41.87) * mm, "end": v(-25.34, -41.87) * mm});
            skLineSegment(sketch, "E28.29.0.7", {"start": v(-26.34, -43.47) * mm, "end": v(-26.34, -43.07) * mm});
            skLineSegment(sketch, "E28.direction1", {"start": v(75.16, -43.47) * mm, "end": v(71.66, -43.47) * mm, "construction": true});
            skSolve(sketch);
        }
        {
            var Q0;
            Q0=makeQuery(id+"F6.imprint","IMPRINT",FACE,{"disambiguationData":[TD([[makeQuery(id+"F6.imprint","IMPRINT",EDGE,{"derivedFrom":sQuery(id+"F6.wireOp",EDGE,"E25.9.0.6")}),-1.0]])]});
            var Q1;
            Q1=makeQuery(id+"F6.imprint","IMPRINT",FACE,{"disambiguationData":[TD([[makeQuery(id+"F6.imprint","IMPRINT",EDGE,{"derivedFrom":sQuery(id+"F6.wireOp",EDGE,"E25.11.0.10")}),1.0]])]});
            var Q2;
            Q2=makeQuery(id+"F6.imprint","IMPRINT",FACE,{"disambiguationData":[TD([[makeQuery(id+"F6.imprint","IMPRINT",EDGE,{"derivedFrom":sQuery(id+"F6.wireOp",EDGE,"E25.3.0.9")}),-1.0]])]});
            var Q3;
            Q3=makeQuery(id+"F6.imprint","IMPRINT",FACE,{"disambiguationData":[TD([[makeQuery(id+"F6.imprint","IMPRINT",EDGE,{"derivedFrom":sQuery(id+"F6.wireOp",EDGE,"E15.bottom")}),1.0]])]});
            var Q4;
            Q4=makeQuery(id+"F6.imprint","IMPRINT",FACE,{"disambiguationData":[TD([[makeQuery(id+"F6.imprint","IMPRINT",EDGE,{"derivedFrom":sQuery(id+"F6.wireOp",EDGE,"E25.1.0.8")}),1.0]])]});
            var Q5;
            Q5=makeQuery(id+"F6.imprint","IMPRINT",FACE,{"disambiguationData":[TD([[makeQuery(id+"F6.imprint","IMPRINT",EDGE,{"derivedFrom":sQuery(id+"F6.wireOp",EDGE,"E25.7.0.8")}),1.0]])]});
            var Q6;
            Q6=makeQuery(id+"F6.imprint","IMPRINT",FACE,{"disambiguationData":[TD([[makeQuery(id+"F6.imprint","IMPRINT",EDGE,{"derivedFrom":sQuery(id+"F6.wireOp",EDGE,"E18.bottom")}),1.0]])]});
            var Q7;
            Q7=makeQuery(id+"F6.imprint","IMPRINT",FACE,{"disambiguationData":[TD([[makeQuery(id+"F6.imprint","IMPRINT",EDGE,{"derivedFrom":sQuery(id+"F6.wireOp",EDGE,"E25.13.0.6")}),-1.0]])]});
            var Q8;
            Q8=makeQuery(id+"F6.imprint","IMPRINT",FACE,{"disambiguationData":[TD([[makeQuery(id+"F6.imprint","IMPRINT",EDGE,{"derivedFrom":sQuery(id+"F6.wireOp",EDGE,"E25.8.0.11")}),1.0]])]});
            var Q9;
            Q9=makeQuery(id+"F6.imprint","IMPRINT",FACE,{"disambiguationData":[TD([[makeQuery(id+"F6.imprint","IMPRINT",EDGE,{"derivedFrom":sQuery(id+"F6.wireOp",EDGE,"E25.14.0.8")}),1.0]])]});
            var Q10;
            Q10=makeQuery(id+"F6.imprint","IMPRINT",FACE,{"disambiguationData":[TD([[makeQuery(id+"F6.imprint","IMPRINT",EDGE,{"derivedFrom":sQuery(id+"F6.wireOp",EDGE,"E25.9.0.10")}),1.0]])]});
            var Q11;
            Q11=makeQuery(id+"F6.imprint","IMPRINT",FACE,{"disambiguationData":[TD([[makeQuery(id+"F6.imprint","IMPRINT",EDGE,{"derivedFrom":sQuery(id+"F6.wireOp",EDGE,"E25.11.0.11")}),1.0]])]});
            var Q12;
            Q12=makeQuery(id+"F6.imprint","IMPRINT",FACE,{"disambiguationData":[TD([[makeQuery(id+"F6.imprint","IMPRINT",EDGE,{"derivedFrom":sQuery(id+"F6.wireOp",EDGE,"E25.7.0.10")}),1.0]])]});
            var Q13;
            Q13=makeQuery(id+"F6.imprint","IMPRINT",FACE,{"disambiguationData":[TD([[makeQuery(id+"F6.imprint","IMPRINT",EDGE,{"derivedFrom":sQuery(id+"F6.wireOp",EDGE,"E25.4.0.11")}),1.0]])]});
            var Q14;
            Q14=makeQuery(id+"F6.imprint","IMPRINT",FACE,{"disambiguationData":[TD([[makeQuery(id+"F6.imprint","IMPRINT",EDGE,{"derivedFrom":sQuery(id+"F6.wireOp",EDGE,"E25.5.0.10")}),1.0]])]});
            var Q15;
            Q15=makeQuery(id+"F6.imprint","IMPRINT",FACE,{"disambiguationData":[TD([[makeQuery(id+"F6.imprint","IMPRINT",EDGE,{"derivedFrom":sQuery(id+"F6.wireOp",EDGE,"E25.12.0.9")}),-1.0]])]});
            var Q16;
            Q16=makeQuery(id+"F6.imprint","IMPRINT",FACE,{"disambiguationData":[TD([[makeQuery(id+"F6.imprint","IMPRINT",EDGE,{"derivedFrom":sQuery(id+"F6.wireOp",EDGE,"E25.13.0.11")}),1.0]])]});
            var Q17;
            Q17=makeQuery(id+"F6.imprint","IMPRINT",FACE,{"disambiguationData":[TD([[makeQuery(id+"F6.imprint","IMPRINT",EDGE,{"derivedFrom":sQuery(id+"F6.wireOp",EDGE,"E25.4.0.13")}),-1.0]])]});
            var Q18;
            Q18=makeQuery(id+"F6.imprint","IMPRINT",FACE,{"disambiguationData":[TD([[makeQuery(id+"F6.imprint","IMPRINT",EDGE,{"derivedFrom":sQuery(id+"F6.wireOp",EDGE,"E25.8.0.10")}),1.0]])]});
            var Q19;
            Q19=makeQuery(id+"F6.imprint","IMPRINT",FACE,{"disambiguationData":[TD([[makeQuery(id+"F6.imprint","IMPRINT",EDGE,{"derivedFrom":sQuery(id+"F6.wireOp",EDGE,"E25.4.0.8")}),1.0]])]});
            var Q20;
            Q20=makeQuery(id+"F6.imprint","IMPRINT",FACE,{"disambiguationData":[TD([[makeQuery(id+"F6.imprint","IMPRINT",EDGE,{"derivedFrom":sQuery(id+"F6.wireOp",EDGE,"E25.11.0.8")}),1.0]])]});
            var Q21;
            Q21=makeQuery(id+"F6.imprint","IMPRINT",FACE,{"disambiguationData":[TD([[makeQuery(id+"F6.imprint","IMPRINT",EDGE,{"derivedFrom":sQuery(id+"F6.wireOp",EDGE,"E25.12.0.6")}),-1.0]])]});
            var Q22;
            Q22=makeQuery(id+"F6.imprint","IMPRINT",FACE,{"disambiguationData":[TD([[makeQuery(id+"F6.imprint","IMPRINT",EDGE,{"derivedFrom":sQuery(id+"F6.wireOp",EDGE,"E25.13.0.13")}),-1.0]])]});
            var Q23;
            Q23=makeQuery(id+"F6.imprint","IMPRINT",FACE,{"disambiguationData":[TD([[makeQuery(id+"F6.imprint","IMPRINT",EDGE,{"derivedFrom":sQuery(id+"F6.wireOp",EDGE,"E25.11.0.6")}),-1.0]])]});
            var Q24;
            Q24=makeQuery(id+"F6.imprint","IMPRINT",FACE,{"disambiguationData":[TD([[makeQuery(id+"F6.imprint","IMPRINT",EDGE,{"derivedFrom":sQuery(id+"F6.wireOp",EDGE,"E25.6.0.8")}),1.0]])]});
            var Q25;
            Q25=makeQuery(id+"F6.imprint","IMPRINT",FACE,{"disambiguationData":[TD([[makeQuery(id+"F6.imprint","IMPRINT",EDGE,{"derivedFrom":sQuery(id+"F6.wireOp",EDGE,"E25.1.0.9")}),-1.0]])]});
            var Q26;
            Q26=makeQuery(id+"F6.imprint","IMPRINT",FACE,{"disambiguationData":[TD([[makeQuery(id+"F6.imprint","IMPRINT",EDGE,{"derivedFrom":sQuery(id+"F6.wireOp",EDGE,"E25.8.0.13")}),-1.0]])]});
            var Q27;
            Q27=makeQuery(id+"F6.imprint","IMPRINT",FACE,{"disambiguationData":[TD([[makeQuery(id+"F6.imprint","IMPRINT",EDGE,{"derivedFrom":sQuery(id+"F6.wireOp",EDGE,"E25.7.0.6")}),-1.0]])]});
            var Q28;
            Q28=makeQuery(id+"F6.imprint","IMPRINT",FACE,{"disambiguationData":[TD([[makeQuery(id+"F6.imprint","IMPRINT",EDGE,{"derivedFrom":sQuery(id+"F6.wireOp",EDGE,"E25.3.0.11")}),1.0]])]});
            var Q29;
            Q29=makeQuery(id+"F6.imprint","IMPRINT",FACE,{"disambiguationData":[TD([[makeQuery(id+"F6.imprint","IMPRINT",EDGE,{"derivedFrom":sQuery(id+"F6.wireOp",EDGE,"E25.7.0.9")}),-1.0]])]});
            var Q30;
            Q30=makeQuery(id+"F6.imprint","IMPRINT",FACE,{"disambiguationData":[TD([[makeQuery(id+"F6.imprint","IMPRINT",EDGE,{"derivedFrom":sQuery(id+"F6.wireOp",EDGE,"E25.5.0.11")}),1.0]])]});
            var Q31;
            Q31=makeQuery(id+"F6.imprint","IMPRINT",FACE,{"disambiguationData":[TD([[makeQuery(id+"F6.imprint","IMPRINT",EDGE,{"derivedFrom":sQuery(id+"F6.wireOp",EDGE,"E25.5.0.13")}),-1.0]])]});
            var Q32;
            Q32=makeQuery(id+"F6.imprint","IMPRINT",FACE,{"disambiguationData":[TD([[makeQuery(id+"F6.imprint","IMPRINT",EDGE,{"derivedFrom":sQuery(id+"F6.wireOp",EDGE,"E25.6.0.10")}),1.0]])]});
            var Q33;
            Q33=makeQuery(id+"F6.imprint","IMPRINT",FACE,{"disambiguationData":[TD([[makeQuery(id+"F6.imprint","IMPRINT",EDGE,{"derivedFrom":sQuery(id+"F6.wireOp",EDGE,"E25.3.0.8")}),1.0]])]});
            var Q34;
            Q34=makeQuery(id+"F6.imprint","IMPRINT",FACE,{"disambiguationData":[TD([[makeQuery(id+"F6.imprint","IMPRINT",EDGE,{"derivedFrom":sQuery(id+"F6.wireOp",EDGE,"E25.3.0.10")}),1.0]])]});
            var Q35;
            Q35=makeQuery(id+"F6.imprint","IMPRINT",FACE,{"disambiguationData":[TD([[makeQuery(id+"F6.imprint","IMPRINT",EDGE,{"derivedFrom":sQuery(id+"F6.wireOp",EDGE,"E25.11.0.9")}),-1.0]])]});
            var Q36;
            Q36=makeQuery(id+"F6.imprint","IMPRINT",FACE,{"disambiguationData":[TD([[makeQuery(id+"F6.imprint","IMPRINT",EDGE,{"derivedFrom":sQuery(id+"F6.wireOp",EDGE,"E25.8.0.9")}),-1.0]])]});
            var Q37;
            Q37=makeQuery(id+"F6.imprint","IMPRINT",FACE,{"disambiguationData":[TD([[makeQuery(id+"F6.imprint","IMPRINT",EDGE,{"derivedFrom":sQuery(id+"F6.wireOp",EDGE,"E25.14.0.10")}),1.0]])]});
            var Q38;
            Q38=makeQuery(id+"F6.imprint","IMPRINT",FACE,{"disambiguationData":[TD([[makeQuery(id+"F6.imprint","IMPRINT",EDGE,{"derivedFrom":sQuery(id+"F6.wireOp",EDGE,"E25.3.0.6")}),-1.0]])]});
            var Q39;
            Q39=makeQuery(id+"F6.imprint","IMPRINT",FACE,{"disambiguationData":[TD([[makeQuery(id+"F6.imprint","IMPRINT",EDGE,{"derivedFrom":sQuery(id+"F6.wireOp",EDGE,"E25.1.0.6")}),-1.0]])]});
            var Q40;
            Q40=makeQuery(id+"F6.imprint","IMPRINT",FACE,{"disambiguationData":[TD([[makeQuery(id+"F6.imprint","IMPRINT",EDGE,{"derivedFrom":sQuery(id+"F6.wireOp",EDGE,"E25.12.0.10")}),1.0]])]});
            var Q41;
            Q41=makeQuery(id+"F6.imprint","IMPRINT",FACE,{"disambiguationData":[TD([[makeQuery(id+"F6.imprint","IMPRINT",EDGE,{"derivedFrom":sQuery(id+"F6.wireOp",EDGE,"E25.5.0.6")}),-1.0]])]});
            var Q42;
            Q42=makeQuery(id+"F6.imprint","IMPRINT",FACE,{"disambiguationData":[TD([[makeQuery(id+"F6.imprint","IMPRINT",EDGE,{"derivedFrom":sQuery(id+"F6.wireOp",EDGE,"E25.2.0.10")}),1.0]])]});
            var Q43;
            Q43=makeQuery(id+"F6.imprint","IMPRINT",FACE,{"disambiguationData":[TD([[makeQuery(id+"F6.imprint","IMPRINT",EDGE,{"derivedFrom":sQuery(id+"F6.wireOp",EDGE,"E25.6.0.11")}),1.0]])]});
            var Q44;
            Q44=makeQuery(id+"F6.imprint","IMPRINT",FACE,{"disambiguationData":[TD([[makeQuery(id+"F6.imprint","IMPRINT",EDGE,{"derivedFrom":sQuery(id+"F6.wireOp",EDGE,"E25.11.0.13")}),-1.0]])]});
            var Q45;
            Q45=makeQuery(id+"F6.imprint","IMPRINT",FACE,{"disambiguationData":[TD([[makeQuery(id+"F6.imprint","IMPRINT",EDGE,{"derivedFrom":sQuery(id+"F6.wireOp",EDGE,"E25.1.0.11")}),1.0]])]});
            var Q46;
            Q46=makeQuery(id+"F6.imprint","IMPRINT",FACE,{"disambiguationData":[TD([[makeQuery(id+"F6.imprint","IMPRINT",EDGE,{"derivedFrom":sQuery(id+"F6.wireOp",EDGE,"E25.9.0.11")}),1.0]])]});
            var Q47;
            Q47=makeQuery(id+"F6.imprint","IMPRINT",FACE,{"disambiguationData":[TD([[makeQuery(id+"F6.imprint","IMPRINT",EDGE,{"derivedFrom":sQuery(id+"F6.wireOp",EDGE,"E25.4.0.10")}),1.0]])]});
            var Q48;
            Q48=makeQuery(id+"F6.imprint","IMPRINT",FACE,{"disambiguationData":[TD([[makeQuery(id+"F6.imprint","IMPRINT",EDGE,{"derivedFrom":sQuery(id+"F6.wireOp",EDGE,"E25.13.0.9")}),-1.0]])]});
            var Q49;
            Q49=makeQuery(id+"F6.imprint","IMPRINT",FACE,{"disambiguationData":[TD([[makeQuery(id+"F6.imprint","IMPRINT",EDGE,{"derivedFrom":sQuery(id+"F6.wireOp",EDGE,"E25.5.0.9")}),-1.0]])]});
            var Q50;
            Q50=makeQuery(id+"F6.imprint","IMPRINT",FACE,{"disambiguationData":[TD([[makeQuery(id+"F6.imprint","IMPRINT",EDGE,{"derivedFrom":sQuery(id+"F6.wireOp",EDGE,"E25.1.0.10")}),1.0]])]});
            var Q51;
            Q51=makeQuery(id+"F6.imprint","IMPRINT",FACE,{"disambiguationData":[TD([[makeQuery(id+"F6.imprint","IMPRINT",EDGE,{"derivedFrom":sQuery(id+"F6.wireOp",EDGE,"E25.9.0.9")}),-1.0]])]});
            var Q52;
            Q52=makeQuery(id+"F6.imprint","IMPRINT",FACE,{"disambiguationData":[TD([[makeQuery(id+"F6.imprint","IMPRINT",EDGE,{"derivedFrom":sQuery(id+"F6.wireOp",EDGE,"E25.14.0.11")}),1.0]])]});
            var Q53;
            Q53=makeQuery(id+"F6.imprint","IMPRINT",FACE,{"disambiguationData":[TD([[makeQuery(id+"F6.imprint","IMPRINT",EDGE,{"derivedFrom":sQuery(id+"F6.wireOp",EDGE,"E25.2.0.11")}),1.0]])]});
            var Q54;
            Q54=makeQuery(id+"F6.imprint","IMPRINT",FACE,{"disambiguationData":[TD([[makeQuery(id+"F6.imprint","IMPRINT",EDGE,{"derivedFrom":sQuery(id+"F6.wireOp",EDGE,"E16.bottom")}),1.0]])]});
            var Q55;
            Q55=makeQuery(id+"F6.imprint","IMPRINT",FACE,{"disambiguationData":[TD([[makeQuery(id+"F6.imprint","IMPRINT",EDGE,{"derivedFrom":sQuery(id+"F6.wireOp",EDGE,"E25.5.0.8")}),1.0]])]});
            var Q56;
            Q56=makeQuery(id+"F6.imprint","IMPRINT",FACE,{"disambiguationData":[TD([[makeQuery(id+"F6.imprint","IMPRINT",EDGE,{"derivedFrom":sQuery(id+"F6.wireOp",EDGE,"E25.1.0.13")}),-1.0]])]});
            var Q57;
            Q57=makeQuery(id+"F6.imprint","IMPRINT",FACE,{"disambiguationData":[TD([[makeQuery(id+"F6.imprint","IMPRINT",EDGE,{"derivedFrom":sQuery(id+"F6.wireOp",EDGE,"E25.9.0.8")}),1.0]])]});
            var Q58;
            Q58=makeQuery(id+"F6.imprint","IMPRINT",FACE,{"disambiguationData":[TD([[makeQuery(id+"F6.imprint","IMPRINT",EDGE,{"derivedFrom":sQuery(id+"F6.wireOp",EDGE,"E25.7.0.13")}),-1.0]])]});
            var Q59;
            Q59=makeQuery(id+"F6.imprint","IMPRINT",FACE,{"disambiguationData":[TD([[makeQuery(id+"F6.imprint","IMPRINT",EDGE,{"derivedFrom":sQuery(id+"F6.wireOp",EDGE,"E25.10.0.11")}),1.0]])]});
            var Q60;
            Q60=makeQuery(id+"F6.imprint","IMPRINT",FACE,{"disambiguationData":[TD([[makeQuery(id+"F6.imprint","IMPRINT",EDGE,{"derivedFrom":sQuery(id+"F6.wireOp",EDGE,"E25.3.0.13")}),-1.0]])]});
            var Q61;
            Q61=makeQuery(id+"F6.imprint","IMPRINT",FACE,{"disambiguationData":[TD([[makeQuery(id+"F6.imprint","IMPRINT",EDGE,{"derivedFrom":sQuery(id+"F6.wireOp",EDGE,"E25.7.0.11")}),1.0]])]});
            var Q62;
            Q62=makeQuery(id+"F6.imprint","IMPRINT",FACE,{"disambiguationData":[TD([[makeQuery(id+"F6.imprint","IMPRINT",EDGE,{"derivedFrom":sQuery(id+"F6.wireOp",EDGE,"E25.12.0.11")}),1.0]])]});
            var Q63;
            Q63=makeQuery(id+"F6.imprint","IMPRINT",FACE,{"disambiguationData":[TD([[makeQuery(id+"F6.imprint","IMPRINT",EDGE,{"derivedFrom":sQuery(id+"F6.wireOp",EDGE,"E25.9.0.13")}),-1.0]])]});
            var Q64;
            Q64=makeQuery(id+"F6.imprint","IMPRINT",FACE,{"disambiguationData":[TD([[makeQuery(id+"F6.imprint","IMPRINT",EDGE,{"derivedFrom":sQuery(id+"F6.wireOp",EDGE,"E25.8.0.6")}),-1.0]])]});
            var Q65;
            Q65=makeQuery(id+"F6.imprint","IMPRINT",FACE,{"disambiguationData":[TD([[makeQuery(id+"F6.imprint","IMPRINT",EDGE,{"derivedFrom":sQuery(id+"F6.wireOp",EDGE,"E25.10.0.10")}),1.0]])]});
            var Q66;
            Q66=makeQuery(id+"F6.imprint","IMPRINT",FACE,{"disambiguationData":[TD([[makeQuery(id+"F6.imprint","IMPRINT",EDGE,{"derivedFrom":sQuery(id+"F6.wireOp",EDGE,"E25.13.0.8")}),1.0]])]});
            var Q67;
            Q67=makeQuery(id+"F6.imprint","IMPRINT",FACE,{"disambiguationData":[TD([[makeQuery(id+"F6.imprint","IMPRINT",EDGE,{"derivedFrom":sQuery(id+"F6.wireOp",EDGE,"E25.14.0.6")}),-1.0]])]});
            var Q68;
            Q68=makeQuery(id+"F6.imprint","IMPRINT",FACE,{"disambiguationData":[TD([[makeQuery(id+"F6.imprint","IMPRINT",EDGE,{"derivedFrom":sQuery(id+"F6.wireOp",EDGE,"E25.13.0.10")}),1.0]])]});
            var Q69;
            Q69=makeQuery(id+"F6.imprint","IMPRINT",FACE,{"disambiguationData":[TD([[makeQuery(id+"F6.imprint","IMPRINT",EDGE,{"derivedFrom":sQuery(id+"F6.wireOp",EDGE,"E17.bottom")}),-1.0]])]});
            var Q70;
            Q70=makeQuery(id+"F6.imprint","IMPRINT",FACE,{"disambiguationData":[TD([[makeQuery(id+"F6.imprint","IMPRINT",EDGE,{"derivedFrom":sQuery(id+"F6.wireOp",EDGE,"E14.bottom")}),1.0]])]});
            var Q71;
            Q71=makeQuery(id+"F6.imprint","IMPRINT",FACE,{"disambiguationData":[TD([[makeQuery(id+"F6.imprint","IMPRINT",EDGE,{"derivedFrom":sQuery(id+"F6.wireOp",EDGE,"E25.10.0.13")}),-1.0]])]});
            var Q72;
            Q72=makeQuery(id+"F6.imprint","IMPRINT",FACE,{"disambiguationData":[TD([[makeQuery(id+"F6.imprint","IMPRINT",EDGE,{"derivedFrom":sQuery(id+"F6.wireOp",EDGE,"E25.4.0.9")}),-1.0]])]});
            var Q73;
            Q73=makeQuery(id+"F6.imprint","IMPRINT",FACE,{"disambiguationData":[TD([[makeQuery(id+"F6.imprint","IMPRINT",EDGE,{"derivedFrom":sQuery(id+"F6.wireOp",EDGE,"E25.14.0.9")}),-1.0]])]});
            var Q74;
            Q74=makeQuery(id+"F6.imprint","IMPRINT",FACE,{"disambiguationData":[TD([[makeQuery(id+"F6.imprint","IMPRINT",EDGE,{"derivedFrom":sQuery(id+"F6.wireOp",EDGE,"E25.2.0.13")}),-1.0]])]});
            var Q75;
            Q75=makeQuery(id+"F6.imprint","IMPRINT",FACE,{"disambiguationData":[TD([[makeQuery(id+"F6.imprint","IMPRINT",EDGE,{"derivedFrom":sQuery(id+"F6.wireOp",EDGE,"E25.8.0.8")}),1.0]])]});
            var Q76;
            Q76=makeQuery(id+"F6.imprint","IMPRINT",FACE,{"disambiguationData":[TD([[makeQuery(id+"F6.imprint","IMPRINT",EDGE,{"derivedFrom":sQuery(id+"F6.wireOp",EDGE,"E25.4.0.6")}),-1.0]])]});
            var Q77;
            Q77=makeQuery(id+"F6.imprint","IMPRINT",FACE,{"disambiguationData":[TD([[makeQuery(id+"F6.imprint","IMPRINT",EDGE,{"derivedFrom":sQuery(id+"F6.wireOp",EDGE,"E25.6.0.6")}),-1.0]])]});
            var Q78;
            Q78=makeQuery(id+"F6.imprint","IMPRINT",FACE,{"disambiguationData":[TD([[makeQuery(id+"F6.imprint","IMPRINT",EDGE,{"derivedFrom":sQuery(id+"F6.wireOp",EDGE,"E25.6.0.9")}),-1.0]])]});
            var Q79;
            Q79=makeQuery(id+"F6.imprint","IMPRINT",FACE,{"disambiguationData":[TD([[makeQuery(id+"F6.imprint","IMPRINT",EDGE,{"derivedFrom":sQuery(id+"F6.wireOp",EDGE,"E25.6.0.13")}),-1.0]])]});
            var Q80;
            Q80=makeQuery(id+"F6.imprint","IMPRINT",FACE,{"disambiguationData":[TD([[makeQuery(id+"F6.imprint","IMPRINT",EDGE,{"derivedFrom":sQuery(id+"F6.wireOp",EDGE,"E25.14.0.13")}),-1.0]])]});
            var Q81;
            Q81=makeQuery(id+"F6.imprint","IMPRINT",FACE,{"disambiguationData":[TD([[makeQuery(id+"F6.imprint","IMPRINT",EDGE,{"derivedFrom":sQuery(id+"F6.wireOp",EDGE,"E25.2.0.8")}),1.0]])]});
            var Q82;
            Q82=makeQuery(id+"F6.imprint","IMPRINT",FACE,{"disambiguationData":[TD([[makeQuery(id+"F6.imprint","IMPRINT",EDGE,{"derivedFrom":sQuery(id+"F6.wireOp",EDGE,"E25.12.0.8")}),1.0]])]});
            var Q83;
            Q83=makeQuery(id+"F6.imprint","IMPRINT",FACE,{"disambiguationData":[TD([[makeQuery(id+"F6.imprint","IMPRINT",EDGE,{"derivedFrom":sQuery(id+"F6.wireOp",EDGE,"E25.2.0.6")}),-1.0]])]});
            var Q84;
            Q84=makeQuery(id+"F6.imprint","IMPRINT",FACE,{"disambiguationData":[TD([[makeQuery(id+"F6.imprint","IMPRINT",EDGE,{"derivedFrom":sQuery(id+"F6.wireOp",EDGE,"E25.12.0.13")}),-1.0]])]});
            var Q85;
            Q85=makeQuery(id+"F6.imprint","IMPRINT",FACE,{"disambiguationData":[TD([[makeQuery(id+"F6.imprint","IMPRINT",EDGE,{"derivedFrom":sQuery(id+"F6.wireOp",EDGE,"E25.10.0.9")}),-1.0]])]});
            var Q86;
            Q86=makeQuery(id+"F6.imprint","IMPRINT",FACE,{"disambiguationData":[TD([[makeQuery(id+"F6.imprint","IMPRINT",EDGE,{"derivedFrom":sQuery(id+"F6.wireOp",EDGE,"E25.10.0.6")}),-1.0]])]});
            var Q87;
            Q87=makeQuery(id+"F6.imprint","IMPRINT",FACE,{"disambiguationData":[TD([[makeQuery(id+"F6.imprint","IMPRINT",EDGE,{"derivedFrom":sQuery(id+"F6.wireOp",EDGE,"E25.2.0.9")}),-1.0]])]});
            var Q88;
            Q88=makeQuery(id+"F6.imprint","IMPRINT",FACE,{"disambiguationData":[TD([[makeQuery(id+"F6.imprint","IMPRINT",EDGE,{"derivedFrom":sQuery(id+"F6.wireOp",EDGE,"E25.10.0.8")}),1.0]])]});
            var Q89;
            Q89=makeQuery(id+"F6.imprint","IMPRINT",FACE,{"disambiguationData":[TD([[makeQuery(id+"F6.imprint","IMPRINT",EDGE,{"derivedFrom":sQuery(id+"F6.wireOp",EDGE,"E13.bottom")}),1.0]])]});
            extrude(context, id + "F7", {"entities" : qUnion([Q0, Q1, Q2, Q3, Q4, Q5, Q6, Q7, Q8, Q9, Q10, Q11, Q12, Q13, Q14, Q15, Q16, Q17, Q18, Q19, Q20, Q21, Q22, Q23, Q24, Q25, Q26, Q27, Q28, Q29, Q30, Q31, Q32, Q33, Q34, Q35, Q36, Q37, Q38, Q39, Q40, Q41, Q42, Q43, Q44, Q45, Q46, Q47, Q48, Q49, Q50, Q51, Q52, Q53, Q54, Q55, Q56, Q57, Q58, Q59, Q60, Q61, Q62, Q63, Q64, Q65, Q66, Q67, Q68, Q69, Q70, Q71, Q72, Q73, Q74, Q75, Q76, Q77, Q78, Q79, Q80, Q81, Q82, Q83, Q84, Q85, Q86, Q87, Q88, Q89]), "depth" : 0.5 * mm, "offsetDistance" : 25 * mm});
        }
        {
            var Q0;
            Q0=makeQuery(id+"F4.imprint","IMPRINT",FACE,{"disambiguationData":[TD([[makeQuery(id+"F4.imprint","IMPRINT",EDGE,{"derivedFrom":sQuery(id+"F4.wireOp",EDGE,"E12.27.0.0")}),1.0]])]});
            var Q1;
            Q1=makeQuery(id+"F4.imprint","IMPRINT",FACE,{"disambiguationData":[TD([[makeQuery(id+"F4.imprint","IMPRINT",EDGE,{"derivedFrom":sQuery(id+"F4.wireOp",EDGE,"E12.28.0.0")}),1.0]])]});
            var Q2;
            Q2=makeQuery(id+"F4.imprint","IMPRINT",FACE,{"disambiguationData":[TD([[makeQuery(id+"F4.imprint","IMPRINT",EDGE,{"derivedFrom":sQuery(id+"F4.wireOp",EDGE,"E12.14.0.0")}),1.0]])]});
            var Q3;
            Q3=makeQuery(id+"F4.imprint","IMPRINT",FACE,{"disambiguationData":[TD([[makeQuery(id+"F4.imprint","IMPRINT",EDGE,{"derivedFrom":sQuery(id+"F4.wireOp",EDGE,"E12.29.0.0")}),1.0]])]});
            var Q4;
            Q4=makeQuery(id+"F4.imprint","IMPRINT",FACE,{"disambiguationData":[TD([[makeQuery(id+"F4.imprint","IMPRINT",EDGE,{"derivedFrom":sQuery(id+"F4.wireOp",EDGE,"E12.7.0.0")}),1.0]])]});
            var Q5;
            Q5=makeQuery(id+"F4.imprint","IMPRINT",FACE,{"disambiguationData":[TD([[makeQuery(id+"F4.imprint","IMPRINT",EDGE,{"derivedFrom":sQuery(id+"F4.wireOp",EDGE,"E12.9.0.0")}),1.0]])]});
            var Q6;
            Q6=makeQuery(id+"F4.imprint","IMPRINT",FACE,{"disambiguationData":[TD([[makeQuery(id+"F4.imprint","IMPRINT",EDGE,{"derivedFrom":sQuery(id+"F4.wireOp",EDGE,"E12.3.0.0")}),1.0]])]});
            var Q7;
            Q7=makeQuery(id+"F4.imprint","IMPRINT",FACE,{"disambiguationData":[TD([[makeQuery(id+"F4.imprint","IMPRINT",EDGE,{"derivedFrom":sQuery(id+"F4.wireOp",EDGE,"E12.4.0.0")}),1.0]])]});
            var Q8;
            Q8=makeQuery(id+"F4.imprint","IMPRINT",FACE,{"disambiguationData":[TD([[makeQuery(id+"F4.imprint","IMPRINT",EDGE,{"derivedFrom":sQuery(id+"F4.wireOp",EDGE,"E12.10.0.0")}),1.0]])]});
            var Q9;
            Q9=makeQuery(id+"F4.imprint","IMPRINT",FACE,{"disambiguationData":[TD([[makeQuery(id+"F4.imprint","IMPRINT",EDGE,{"derivedFrom":sQuery(id+"F4.wireOp",EDGE,"E12.12.0.0")}),1.0]])]});
            var Q10;
            Q10=makeQuery(id+"F4.imprint","IMPRINT",FACE,{"disambiguationData":[TD([[makeQuery(id+"F4.imprint","IMPRINT",EDGE,{"derivedFrom":sQuery(id+"F4.wireOp",EDGE,"E11.bottom")}),-1.0]])]});
            var Q11;
            Q11=makeQuery(id+"F4.imprint","IMPRINT",FACE,{"disambiguationData":[TD([[makeQuery(id+"F4.imprint","IMPRINT",EDGE,{"derivedFrom":sQuery(id+"F4.wireOp",EDGE,"E12.6.0.0")}),1.0]])]});
            var Q12;
            Q12=makeQuery(id+"F4.imprint","IMPRINT",FACE,{"disambiguationData":[TD([[makeQuery(id+"F4.imprint","IMPRINT",EDGE,{"derivedFrom":sQuery(id+"F4.wireOp",EDGE,"E12.8.0.0")}),1.0]])]});
            var Q13;
            Q13=makeQuery(id+"F4.imprint","IMPRINT",FACE,{"disambiguationData":[TD([[makeQuery(id+"F4.imprint","IMPRINT",EDGE,{"derivedFrom":sQuery(id+"F4.wireOp",EDGE,"E12.26.0.0")}),1.0]])]});
            var Q14;
            Q14=makeQuery(id+"F4.imprint","IMPRINT",FACE,{"disambiguationData":[TD([[makeQuery(id+"F4.imprint","IMPRINT",EDGE,{"derivedFrom":sQuery(id+"F4.wireOp",EDGE,"E12.18.0.0")}),1.0]])]});
            var Q15;
            Q15=makeQuery(id+"F4.imprint","IMPRINT",FACE,{"disambiguationData":[TD([[makeQuery(id+"F4.imprint","IMPRINT",EDGE,{"derivedFrom":sQuery(id+"F4.wireOp",EDGE,"E12.24.0.0")}),1.0]])]});
            var Q16;
            Q16=makeQuery(id+"F4.imprint","IMPRINT",FACE,{"disambiguationData":[TD([[makeQuery(id+"F4.imprint","IMPRINT",EDGE,{"derivedFrom":sQuery(id+"F4.wireOp",EDGE,"E12.22.0.0")}),1.0]])]});
            var Q17;
            Q17=makeQuery(id+"F4.imprint","IMPRINT",FACE,{"disambiguationData":[TD([[makeQuery(id+"F4.imprint","IMPRINT",EDGE,{"derivedFrom":sQuery(id+"F4.wireOp",EDGE,"E12.16.0.0")}),1.0]])]});
            var Q18;
            Q18=makeQuery(id+"F4.imprint","IMPRINT",FACE,{"disambiguationData":[TD([[makeQuery(id+"F4.imprint","IMPRINT",EDGE,{"derivedFrom":sQuery(id+"F4.wireOp",EDGE,"E12.20.0.0")}),1.0]])]});
            var Q19;
            Q19=makeQuery(id+"F4.imprint","IMPRINT",FACE,{"disambiguationData":[TD([[makeQuery(id+"F4.imprint","IMPRINT",EDGE,{"derivedFrom":sQuery(id+"F4.wireOp",EDGE,"E12.1.0.0")}),1.0]])]});
            var Q20;
            Q20=makeQuery(id+"F4.imprint","IMPRINT",FACE,{"disambiguationData":[TD([[makeQuery(id+"F4.imprint","IMPRINT",EDGE,{"derivedFrom":sQuery(id+"F4.wireOp",EDGE,"E12.5.0.0")}),1.0]])]});
            var Q21;
            Q21=makeQuery(id+"F4.imprint","IMPRINT",FACE,{"disambiguationData":[TD([[makeQuery(id+"F4.imprint","IMPRINT",EDGE,{"derivedFrom":sQuery(id+"F4.wireOp",EDGE,"E12.13.0.0")}),1.0]])]});
            var Q22;
            Q22=makeQuery(id+"F4.imprint","IMPRINT",FACE,{"disambiguationData":[TD([[makeQuery(id+"F4.imprint","IMPRINT",EDGE,{"derivedFrom":sQuery(id+"F4.wireOp",EDGE,"E12.19.0.0")}),1.0]])]});
            var Q23;
            Q23=makeQuery(id+"F4.imprint","IMPRINT",FACE,{"disambiguationData":[TD([[makeQuery(id+"F4.imprint","IMPRINT",EDGE,{"derivedFrom":sQuery(id+"F4.wireOp",EDGE,"E12.25.0.0")}),1.0]])]});
            var Q24;
            Q24=makeQuery(id+"F4.imprint","IMPRINT",FACE,{"disambiguationData":[TD([[makeQuery(id+"F4.imprint","IMPRINT",EDGE,{"derivedFrom":sQuery(id+"F4.wireOp",EDGE,"E12.23.0.0")}),1.0]])]});
            var Q25;
            Q25=makeQuery(id+"F4.imprint","IMPRINT",FACE,{"disambiguationData":[TD([[makeQuery(id+"F4.imprint","IMPRINT",EDGE,{"derivedFrom":sQuery(id+"F4.wireOp",EDGE,"E12.17.0.0")}),1.0]])]});
            var Q26;
            Q26=makeQuery(id+"F4.imprint","IMPRINT",FACE,{"disambiguationData":[TD([[makeQuery(id+"F4.imprint","IMPRINT",EDGE,{"derivedFrom":sQuery(id+"F4.wireOp",EDGE,"E12.15.0.0")}),1.0]])]});
            var Q27;
            Q27=makeQuery(id+"F4.imprint","IMPRINT",FACE,{"disambiguationData":[TD([[makeQuery(id+"F4.imprint","IMPRINT",EDGE,{"derivedFrom":sQuery(id+"F4.wireOp",EDGE,"E12.21.0.0")}),1.0]])]});
            var Q28;
            Q28=makeQuery(id+"F4.imprint","IMPRINT",FACE,{"disambiguationData":[TD([[makeQuery(id+"F4.imprint","IMPRINT",EDGE,{"derivedFrom":sQuery(id+"F4.wireOp",EDGE,"E12.2.0.0")}),1.0]])]});
            var Q29;
            Q29=makeQuery(id+"F4.imprint","IMPRINT",FACE,{"disambiguationData":[TD([[makeQuery(id+"F4.imprint","IMPRINT",EDGE,{"derivedFrom":sQuery(id+"F4.wireOp",EDGE,"E12.11.0.0")}),1.0]])]});
            var Q30;
            Q30=makeQuery(id+"F6.imprint","IMPRINT",FACE,{"disambiguationData":[TD([[makeQuery(id+"F6.imprint","IMPRINT",EDGE,{"derivedFrom":sQuery(id+"F6.wireOp",EDGE,"E28.21.0.3")}),1.0]])]});
            var Q31;
            Q31=makeQuery(id+"F6.imprint","IMPRINT",FACE,{"disambiguationData":[TD([[makeQuery(id+"F6.imprint","IMPRINT",EDGE,{"derivedFrom":sQuery(id+"F6.wireOp",EDGE,"E28.12.0.3")}),1.0]])]});
            var Q32;
            Q32=makeQuery(id+"F6.imprint","IMPRINT",FACE,{"disambiguationData":[TD([[makeQuery(id+"F6.imprint","IMPRINT",EDGE,{"derivedFrom":sQuery(id+"F6.wireOp",EDGE,"E28.22.0.3")}),1.0]])]});
            var Q33;
            Q33=makeQuery(id+"F6.imprint","IMPRINT",FACE,{"disambiguationData":[TD([[makeQuery(id+"F6.imprint","IMPRINT",EDGE,{"derivedFrom":sQuery(id+"F6.wireOp",EDGE,"E28.15.0.3")}),1.0]])]});
            var Q34;
            Q34=makeQuery(id+"F6.imprint","IMPRINT",FACE,{"disambiguationData":[TD([[makeQuery(id+"F6.imprint","IMPRINT",EDGE,{"derivedFrom":sQuery(id+"F6.wireOp",EDGE,"E28.17.0.3")}),1.0]])]});
            var Q35;
            Q35=makeQuery(id+"F6.imprint","IMPRINT",FACE,{"disambiguationData":[TD([[makeQuery(id+"F6.imprint","IMPRINT",EDGE,{"derivedFrom":sQuery(id+"F6.wireOp",EDGE,"E28.20.0.3")}),1.0]])]});
            var Q36;
            Q36=makeQuery(id+"F6.imprint","IMPRINT",FACE,{"disambiguationData":[TD([[makeQuery(id+"F6.imprint","IMPRINT",EDGE,{"derivedFrom":sQuery(id+"F6.wireOp",EDGE,"E28.6.0.3")}),1.0]])]});
            var Q37;
            Q37=makeQuery(id+"F6.imprint","IMPRINT",FACE,{"disambiguationData":[TD([[makeQuery(id+"F6.imprint","IMPRINT",EDGE,{"derivedFrom":sQuery(id+"F6.wireOp",EDGE,"E28.13.0.3")}),1.0]])]});
            var Q38;
            Q38=makeQuery(id+"F6.imprint","IMPRINT",FACE,{"disambiguationData":[TD([[makeQuery(id+"F6.imprint","IMPRINT",EDGE,{"derivedFrom":sQuery(id+"F6.wireOp",EDGE,"E28.28.0.3")}),1.0]])]});
            var Q39;
            Q39=makeQuery(id+"F6.imprint","IMPRINT",FACE,{"disambiguationData":[TD([[makeQuery(id+"F6.imprint","IMPRINT",EDGE,{"derivedFrom":sQuery(id+"F6.wireOp",EDGE,"E28.2.0.3")}),1.0]])]});
            var Q40;
            Q40=makeQuery(id+"F6.imprint","IMPRINT",FACE,{"disambiguationData":[TD([[makeQuery(id+"F6.imprint","IMPRINT",EDGE,{"derivedFrom":sQuery(id+"F6.wireOp",EDGE,"E28.27.0.3")}),1.0]])]});
            var Q41;
            Q41=makeQuery(id+"F6.imprint","IMPRINT",FACE,{"disambiguationData":[TD([[makeQuery(id+"F6.imprint","IMPRINT",EDGE,{"derivedFrom":sQuery(id+"F6.wireOp",EDGE,"E28.26.0.3")}),1.0]])]});
            var Q42;
            Q42=makeQuery(id+"F6.imprint","IMPRINT",FACE,{"disambiguationData":[TD([[makeQuery(id+"F6.imprint","IMPRINT",EDGE,{"derivedFrom":sQuery(id+"F6.wireOp",EDGE,"E28.11.0.3")}),1.0]])]});
            var Q43;
            Q43=makeQuery(id+"F6.imprint","IMPRINT",FACE,{"disambiguationData":[TD([[makeQuery(id+"F6.imprint","IMPRINT",EDGE,{"derivedFrom":sQuery(id+"F6.wireOp",EDGE,"E28.29.0.3")}),1.0]])]});
            var Q44;
            Q44=makeQuery(id+"F6.imprint","IMPRINT",FACE,{"disambiguationData":[TD([[makeQuery(id+"F6.imprint","IMPRINT",EDGE,{"derivedFrom":sQuery(id+"F6.wireOp",EDGE,"E28.16.0.3")}),1.0]])]});
            var Q45;
            Q45=makeQuery(id+"F6.imprint","IMPRINT",FACE,{"disambiguationData":[TD([[makeQuery(id+"F6.imprint","IMPRINT",EDGE,{"derivedFrom":sQuery(id+"F6.wireOp",EDGE,"E28.14.0.3")}),1.0]])]});
            var Q46;
            Q46=makeQuery(id+"F6.imprint","IMPRINT",FACE,{"disambiguationData":[TD([[makeQuery(id+"F6.imprint","IMPRINT",EDGE,{"derivedFrom":sQuery(id+"F6.wireOp",EDGE,"E26.bottom")}),-1.0]])]});
            var Q47;
            Q47=makeQuery(id+"F6.imprint","IMPRINT",FACE,{"disambiguationData":[TD([[makeQuery(id+"F6.imprint","IMPRINT",EDGE,{"derivedFrom":sQuery(id+"F6.wireOp",EDGE,"E28.23.0.3")}),1.0]])]});
            var Q48;
            Q48=makeQuery(id+"F6.imprint","IMPRINT",FACE,{"disambiguationData":[TD([[makeQuery(id+"F6.imprint","IMPRINT",EDGE,{"derivedFrom":sQuery(id+"F6.wireOp",EDGE,"E28.5.0.3")}),1.0]])]});
            var Q49;
            Q49=makeQuery(id+"F6.imprint","IMPRINT",FACE,{"disambiguationData":[TD([[makeQuery(id+"F6.imprint","IMPRINT",EDGE,{"derivedFrom":sQuery(id+"F6.wireOp",EDGE,"E28.10.0.3")}),1.0]])]});
            var Q50;
            Q50=makeQuery(id+"F6.imprint","IMPRINT",FACE,{"disambiguationData":[TD([[makeQuery(id+"F6.imprint","IMPRINT",EDGE,{"derivedFrom":sQuery(id+"F6.wireOp",EDGE,"E28.1.0.3")}),1.0]])]});
            var Q51;
            Q51=makeQuery(id+"F6.imprint","IMPRINT",FACE,{"disambiguationData":[TD([[makeQuery(id+"F6.imprint","IMPRINT",EDGE,{"derivedFrom":sQuery(id+"F6.wireOp",EDGE,"E28.19.0.3")}),1.0]])]});
            var Q52;
            Q52=makeQuery(id+"F6.imprint","IMPRINT",FACE,{"disambiguationData":[TD([[makeQuery(id+"F6.imprint","IMPRINT",EDGE,{"derivedFrom":sQuery(id+"F6.wireOp",EDGE,"E28.3.0.3")}),1.0]])]});
            var Q53;
            Q53=makeQuery(id+"F6.imprint","IMPRINT",FACE,{"disambiguationData":[TD([[makeQuery(id+"F6.imprint","IMPRINT",EDGE,{"derivedFrom":sQuery(id+"F6.wireOp",EDGE,"E28.9.0.3")}),1.0]])]});
            var Q54;
            Q54=makeQuery(id+"F6.imprint","IMPRINT",FACE,{"disambiguationData":[TD([[makeQuery(id+"F6.imprint","IMPRINT",EDGE,{"derivedFrom":sQuery(id+"F6.wireOp",EDGE,"E28.18.0.3")}),1.0]])]});
            var Q55;
            Q55=makeQuery(id+"F6.imprint","IMPRINT",FACE,{"disambiguationData":[TD([[makeQuery(id+"F6.imprint","IMPRINT",EDGE,{"derivedFrom":sQuery(id+"F6.wireOp",EDGE,"E28.4.0.3")}),1.0]])]});
            var Q56;
            Q56=makeQuery(id+"F6.imprint","IMPRINT",FACE,{"disambiguationData":[TD([[makeQuery(id+"F6.imprint","IMPRINT",EDGE,{"derivedFrom":sQuery(id+"F6.wireOp",EDGE,"E28.25.0.3")}),1.0]])]});
            var Q57;
            Q57=makeQuery(id+"F6.imprint","IMPRINT",FACE,{"disambiguationData":[TD([[makeQuery(id+"F6.imprint","IMPRINT",EDGE,{"derivedFrom":sQuery(id+"F6.wireOp",EDGE,"E28.8.0.3")}),1.0]])]});
            var Q58;
            Q58=makeQuery(id+"F6.imprint","IMPRINT",FACE,{"disambiguationData":[TD([[makeQuery(id+"F6.imprint","IMPRINT",EDGE,{"derivedFrom":sQuery(id+"F6.wireOp",EDGE,"E28.7.0.3")}),1.0]])]});
            var Q59;
            Q59=makeQuery(id+"F6.imprint","IMPRINT",FACE,{"disambiguationData":[TD([[makeQuery(id+"F6.imprint","IMPRINT",EDGE,{"derivedFrom":sQuery(id+"F6.wireOp",EDGE,"E28.24.0.3")}),1.0]])]});
            extrude(context, id + "F8", {"entities" : qUnion([Q0, Q1, Q2, Q3, Q4, Q5, Q6, Q7, Q8, Q9, Q10, Q11, Q12, Q13, Q14, Q15, Q16, Q17, Q18, Q19, Q20, Q21, Q22, Q23, Q24, Q25, Q26, Q27, Q28, Q29, Q30, Q31, Q32, Q33, Q34, Q35, Q36, Q37, Q38, Q39, Q40, Q41, Q42, Q43, Q44, Q45, Q46, Q47, Q48, Q49, Q50, Q51, Q52, Q53, Q54, Q55, Q56, Q57, Q58, Q59]), "depth" : 0.25 * mm, "offsetDistance" : 25 * mm});
        }
        {
            var Q0;
            Q0=makeQuery(id+"F6.imprint","IMPRINT",FACE,{"disambiguationData":[TD([[makeQuery(id+"F6.imprint","IMPRINT",EDGE,{"derivedFrom":sQuery(id+"F6.wireOp",EDGE,"E28.6.0.0")}),-1.0]])]});
            var Q1;
            Q1=makeQuery(id+"F6.imprint","IMPRINT",FACE,{"disambiguationData":[TD([[makeQuery(id+"F6.imprint","IMPRINT",EDGE,{"derivedFrom":sQuery(id+"F6.wireOp",EDGE,"E28.14.0.0")}),-1.0]])]});
            var Q2;
            Q2=makeQuery(id+"F6.imprint","IMPRINT",FACE,{"disambiguationData":[TD([[makeQuery(id+"F6.imprint","IMPRINT",EDGE,{"derivedFrom":sQuery(id+"F6.wireOp",EDGE,"E28.22.0.0")}),-1.0]])]});
            var Q3;
            Q3=makeQuery(id+"F6.imprint","IMPRINT",FACE,{"disambiguationData":[TD([[makeQuery(id+"F6.imprint","IMPRINT",EDGE,{"derivedFrom":sQuery(id+"F6.wireOp",EDGE,"E28.12.0.0")}),-1.0]])]});
            var Q4;
            Q4=makeQuery(id+"F6.imprint","IMPRINT",FACE,{"disambiguationData":[TD([[makeQuery(id+"F6.imprint","IMPRINT",EDGE,{"derivedFrom":sQuery(id+"F6.wireOp",EDGE,"E28.11.0.0")}),-1.0]])]});
            var Q5;
            Q5=makeQuery(id+"F6.imprint","IMPRINT",FACE,{"disambiguationData":[TD([[makeQuery(id+"F6.imprint","IMPRINT",EDGE,{"derivedFrom":sQuery(id+"F6.wireOp",EDGE,"E28.15.0.0")}),-1.0]])]});
            var Q6;
            Q6=makeQuery(id+"F6.imprint","IMPRINT",FACE,{"disambiguationData":[TD([[makeQuery(id+"F6.imprint","IMPRINT",EDGE,{"derivedFrom":sQuery(id+"F6.wireOp",EDGE,"E28.24.0.0")}),-1.0]])]});
            var Q7;
            Q7=makeQuery(id+"F6.imprint","IMPRINT",FACE,{"disambiguationData":[TD([[makeQuery(id+"F6.imprint","IMPRINT",EDGE,{"derivedFrom":sQuery(id+"F6.wireOp",EDGE,"E28.21.0.0")}),-1.0]])]});
            var Q8;
            Q8=makeQuery(id+"F6.imprint","IMPRINT",FACE,{"disambiguationData":[TD([[makeQuery(id+"F6.imprint","IMPRINT",EDGE,{"derivedFrom":sQuery(id+"F6.wireOp",EDGE,"E28.10.0.0")}),-1.0]])]});
            var Q9;
            Q9=makeQuery(id+"F6.imprint","IMPRINT",FACE,{"disambiguationData":[TD([[makeQuery(id+"F6.imprint","IMPRINT",EDGE,{"derivedFrom":sQuery(id+"F6.wireOp",EDGE,"E28.2.0.0")}),-1.0]])]});
            var Q10;
            Q10=makeQuery(id+"F6.imprint","IMPRINT",FACE,{"disambiguationData":[TD([[makeQuery(id+"F6.imprint","IMPRINT",EDGE,{"derivedFrom":sQuery(id+"F6.wireOp",EDGE,"E28.20.0.0")}),-1.0]])]});
            var Q11;
            Q11=makeQuery(id+"F6.imprint","IMPRINT",FACE,{"disambiguationData":[TD([[makeQuery(id+"F6.imprint","IMPRINT",EDGE,{"derivedFrom":sQuery(id+"F6.wireOp",EDGE,"E28.13.0.0")}),-1.0]])]});
            var Q12;
            Q12=makeQuery(id+"F6.imprint","IMPRINT",FACE,{"disambiguationData":[TD([[makeQuery(id+"F6.imprint","IMPRINT",EDGE,{"derivedFrom":sQuery(id+"F6.wireOp",EDGE,"E28.5.0.0")}),-1.0]])]});
            var Q13;
            Q13=makeQuery(id+"F6.imprint","IMPRINT",FACE,{"disambiguationData":[TD([[makeQuery(id+"F6.imprint","IMPRINT",EDGE,{"derivedFrom":sQuery(id+"F6.wireOp",EDGE,"E28.29.0.0")}),-1.0]])]});
            var Q14;
            Q14=makeQuery(id+"F6.imprint","IMPRINT",FACE,{"disambiguationData":[TD([[makeQuery(id+"F6.imprint","IMPRINT",EDGE,{"derivedFrom":sQuery(id+"F6.wireOp",EDGE,"E28.28.0.0")}),-1.0]])]});
            var Q15;
            Q15=makeQuery(id+"F6.imprint","IMPRINT",FACE,{"disambiguationData":[TD([[makeQuery(id+"F6.imprint","IMPRINT",EDGE,{"derivedFrom":sQuery(id+"F6.wireOp",EDGE,"E28.4.0.0")}),-1.0]])]});
            var Q16;
            Q16=makeQuery(id+"F6.imprint","IMPRINT",FACE,{"disambiguationData":[TD([[makeQuery(id+"F6.imprint","IMPRINT",EDGE,{"derivedFrom":sQuery(id+"F6.wireOp",EDGE,"E28.8.0.0")}),-1.0]])]});
            var Q17;
            Q17=makeQuery(id+"F6.imprint","IMPRINT",FACE,{"disambiguationData":[TD([[makeQuery(id+"F6.imprint","IMPRINT",EDGE,{"derivedFrom":sQuery(id+"F6.wireOp",EDGE,"E28.27.0.0")}),-1.0]])]});
            var Q18;
            Q18=makeQuery(id+"F6.imprint","IMPRINT",FACE,{"disambiguationData":[TD([[makeQuery(id+"F6.imprint","IMPRINT",EDGE,{"derivedFrom":sQuery(id+"F6.wireOp",EDGE,"E28.26.0.0")}),-1.0]])]});
            var Q19;
            Q19=makeQuery(id+"F6.imprint","IMPRINT",FACE,{"disambiguationData":[TD([[makeQuery(id+"F6.imprint","IMPRINT",EDGE,{"derivedFrom":sQuery(id+"F6.wireOp",EDGE,"E28.25.0.0")}),-1.0]])]});
            var Q20;
            Q20=makeQuery(id+"F6.imprint","IMPRINT",FACE,{"disambiguationData":[TD([[makeQuery(id+"F6.imprint","IMPRINT",EDGE,{"derivedFrom":sQuery(id+"F6.wireOp",EDGE,"E28.9.0.0")}),-1.0]])]});
            var Q21;
            Q21=makeQuery(id+"F6.imprint","IMPRINT",FACE,{"disambiguationData":[TD([[makeQuery(id+"F6.imprint","IMPRINT",EDGE,{"derivedFrom":sQuery(id+"F6.wireOp",EDGE,"E28.7.0.0")}),-1.0]])]});
            var Q22;
            Q22=makeQuery(id+"F6.imprint","IMPRINT",FACE,{"disambiguationData":[TD([[makeQuery(id+"F6.imprint","IMPRINT",EDGE,{"derivedFrom":sQuery(id+"F6.wireOp",EDGE,"E26.bottom")}),1.0]])]});
            var Q23;
            Q23=makeQuery(id+"F6.imprint","IMPRINT",FACE,{"disambiguationData":[TD([[makeQuery(id+"F6.imprint","IMPRINT",EDGE,{"derivedFrom":sQuery(id+"F6.wireOp",EDGE,"E28.18.0.0")}),-1.0]])]});
            var Q24;
            Q24=makeQuery(id+"F6.imprint","IMPRINT",FACE,{"disambiguationData":[TD([[makeQuery(id+"F6.imprint","IMPRINT",EDGE,{"derivedFrom":sQuery(id+"F6.wireOp",EDGE,"E28.1.0.0")}),-1.0]])]});
            var Q25;
            Q25=makeQuery(id+"F6.imprint","IMPRINT",FACE,{"disambiguationData":[TD([[makeQuery(id+"F6.imprint","IMPRINT",EDGE,{"derivedFrom":sQuery(id+"F6.wireOp",EDGE,"E28.23.0.0")}),-1.0]])]});
            var Q26;
            Q26=makeQuery(id+"F6.imprint","IMPRINT",FACE,{"disambiguationData":[TD([[makeQuery(id+"F6.imprint","IMPRINT",EDGE,{"derivedFrom":sQuery(id+"F6.wireOp",EDGE,"E28.19.0.0")}),-1.0]])]});
            var Q27;
            Q27=makeQuery(id+"F6.imprint","IMPRINT",FACE,{"disambiguationData":[TD([[makeQuery(id+"F6.imprint","IMPRINT",EDGE,{"derivedFrom":sQuery(id+"F6.wireOp",EDGE,"E28.17.0.0")}),-1.0]])]});
            var Q28;
            Q28=makeQuery(id+"F6.imprint","IMPRINT",FACE,{"disambiguationData":[TD([[makeQuery(id+"F6.imprint","IMPRINT",EDGE,{"derivedFrom":sQuery(id+"F6.wireOp",EDGE,"E28.16.0.0")}),-1.0]])]});
            var Q29;
            Q29=makeQuery(id+"F6.imprint","IMPRINT",FACE,{"disambiguationData":[TD([[makeQuery(id+"F6.imprint","IMPRINT",EDGE,{"derivedFrom":sQuery(id+"F6.wireOp",EDGE,"E28.3.0.0")}),-1.0]])]});
            var Q30;
            Q30=makeQuery(id+"F6.imprint","IMPRINT",FACE,{"disambiguationData":[TD([[makeQuery(id+"F6.imprint","IMPRINT",EDGE,{"derivedFrom":sQuery(id+"F6.wireOp",EDGE,"E28.3.0.3")}),-1.0]])]});
            var Q31;
            Q31=makeQuery(id+"F6.imprint","IMPRINT",FACE,{"disambiguationData":[TD([[makeQuery(id+"F6.imprint","IMPRINT",EDGE,{"derivedFrom":sQuery(id+"F6.wireOp",EDGE,"E28.29.0.3")}),-1.0]])]});
            var Q32;
            Q32=makeQuery(id+"F6.imprint","IMPRINT",FACE,{"disambiguationData":[TD([[makeQuery(id+"F6.imprint","IMPRINT",EDGE,{"derivedFrom":sQuery(id+"F6.wireOp",EDGE,"E28.15.0.3")}),-1.0]])]});
            var Q33;
            Q33=makeQuery(id+"F6.imprint","IMPRINT",FACE,{"disambiguationData":[TD([[makeQuery(id+"F6.imprint","IMPRINT",EDGE,{"derivedFrom":sQuery(id+"F6.wireOp",EDGE,"E28.1.0.3")}),-1.0]])]});
            var Q34;
            Q34=makeQuery(id+"F6.imprint","IMPRINT",FACE,{"disambiguationData":[TD([[makeQuery(id+"F6.imprint","IMPRINT",EDGE,{"derivedFrom":sQuery(id+"F6.wireOp",EDGE,"E28.9.0.3")}),-1.0]])]});
            var Q35;
            Q35=makeQuery(id+"F6.imprint","IMPRINT",FACE,{"disambiguationData":[TD([[makeQuery(id+"F6.imprint","IMPRINT",EDGE,{"derivedFrom":sQuery(id+"F6.wireOp",EDGE,"E28.23.0.3")}),-1.0]])]});
            var Q36;
            Q36=makeQuery(id+"F6.imprint","IMPRINT",FACE,{"disambiguationData":[TD([[makeQuery(id+"F6.imprint","IMPRINT",EDGE,{"derivedFrom":sQuery(id+"F6.wireOp",EDGE,"E28.4.0.3")}),-1.0]])]});
            var Q37;
            Q37=makeQuery(id+"F6.imprint","IMPRINT",FACE,{"disambiguationData":[TD([[makeQuery(id+"F6.imprint","IMPRINT",EDGE,{"derivedFrom":sQuery(id+"F6.wireOp",EDGE,"E28.26.0.3")}),-1.0]])]});
            var Q38;
            Q38=makeQuery(id+"F6.imprint","IMPRINT",FACE,{"disambiguationData":[TD([[makeQuery(id+"F6.imprint","IMPRINT",EDGE,{"derivedFrom":sQuery(id+"F6.wireOp",EDGE,"E28.18.0.3")}),-1.0]])]});
            var Q39;
            Q39=makeQuery(id+"F6.imprint","IMPRINT",FACE,{"disambiguationData":[TD([[makeQuery(id+"F6.imprint","IMPRINT",EDGE,{"derivedFrom":sQuery(id+"F6.wireOp",EDGE,"E28.16.0.3")}),-1.0]])]});
            var Q40;
            Q40=makeQuery(id+"F6.imprint","IMPRINT",FACE,{"disambiguationData":[TD([[makeQuery(id+"F6.imprint","IMPRINT",EDGE,{"derivedFrom":sQuery(id+"F6.wireOp",EDGE,"E28.12.0.3")}),-1.0]])]});
            var Q41;
            Q41=makeQuery(id+"F6.imprint","IMPRINT",FACE,{"disambiguationData":[TD([[makeQuery(id+"F6.imprint","IMPRINT",EDGE,{"derivedFrom":sQuery(id+"F6.wireOp",EDGE,"E28.28.0.3")}),-1.0]])]});
            var Q42;
            Q42=makeQuery(id+"F6.imprint","IMPRINT",FACE,{"disambiguationData":[TD([[makeQuery(id+"F6.imprint","IMPRINT",EDGE,{"derivedFrom":sQuery(id+"F6.wireOp",EDGE,"E28.6.0.3")}),-1.0]])]});
            var Q43;
            Q43=makeQuery(id+"F6.imprint","IMPRINT",FACE,{"disambiguationData":[TD([[makeQuery(id+"F6.imprint","IMPRINT",EDGE,{"derivedFrom":sQuery(id+"F6.wireOp",EDGE,"E28.5.0.3")}),-1.0]])]});
            var Q44;
            Q44=makeQuery(id+"F6.imprint","IMPRINT",FACE,{"disambiguationData":[TD([[makeQuery(id+"F6.imprint","IMPRINT",EDGE,{"derivedFrom":sQuery(id+"F6.wireOp",EDGE,"E28.19.0.3")}),-1.0]])]});
            var Q45;
            Q45=makeQuery(id+"F6.imprint","IMPRINT",FACE,{"disambiguationData":[TD([[makeQuery(id+"F6.imprint","IMPRINT",EDGE,{"derivedFrom":sQuery(id+"F6.wireOp",EDGE,"E28.11.0.3")}),-1.0]])]});
            var Q46;
            Q46=makeQuery(id+"F6.imprint","IMPRINT",FACE,{"disambiguationData":[TD([[makeQuery(id+"F6.imprint","IMPRINT",EDGE,{"derivedFrom":sQuery(id+"F6.wireOp",EDGE,"E28.13.0.3")}),-1.0]])]});
            var Q47;
            Q47=makeQuery(id+"F6.imprint","IMPRINT",FACE,{"disambiguationData":[TD([[makeQuery(id+"F6.imprint","IMPRINT",EDGE,{"derivedFrom":sQuery(id+"F6.wireOp",EDGE,"E28.2.0.3")}),-1.0]])]});
            var Q48;
            Q48=makeQuery(id+"F6.imprint","IMPRINT",FACE,{"disambiguationData":[TD([[makeQuery(id+"F6.imprint","IMPRINT",EDGE,{"derivedFrom":sQuery(id+"F6.wireOp",EDGE,"E28.22.0.3")}),-1.0]])]});
            var Q49;
            Q49=makeQuery(id+"F6.imprint","IMPRINT",FACE,{"disambiguationData":[TD([[makeQuery(id+"F6.imprint","IMPRINT",EDGE,{"derivedFrom":sQuery(id+"F6.wireOp",EDGE,"E28.21.0.3")}),-1.0]])]});
            var Q50;
            Q50=makeQuery(id+"F6.imprint","IMPRINT",FACE,{"disambiguationData":[TD([[makeQuery(id+"F6.imprint","IMPRINT",EDGE,{"derivedFrom":sQuery(id+"F6.wireOp",EDGE,"E28.20.0.3")}),-1.0]])]});
            var Q51;
            Q51=makeQuery(id+"F6.imprint","IMPRINT",FACE,{"disambiguationData":[TD([[makeQuery(id+"F6.imprint","IMPRINT",EDGE,{"derivedFrom":sQuery(id+"F6.wireOp",EDGE,"E28.27.0.3")}),-1.0]])]});
            var Q52;
            Q52=makeQuery(id+"F6.imprint","IMPRINT",FACE,{"disambiguationData":[TD([[makeQuery(id+"F6.imprint","IMPRINT",EDGE,{"derivedFrom":sQuery(id+"F6.wireOp",EDGE,"E28.10.0.3")}),-1.0]])]});
            var Q53;
            Q53=makeQuery(id+"F6.imprint","IMPRINT",FACE,{"disambiguationData":[TD([[makeQuery(id+"F6.imprint","IMPRINT",EDGE,{"derivedFrom":sQuery(id+"F6.wireOp",EDGE,"E28.8.0.3")}),-1.0]])]});
            var Q54;
            Q54=makeQuery(id+"F6.imprint","IMPRINT",FACE,{"disambiguationData":[TD([[makeQuery(id+"F6.imprint","IMPRINT",EDGE,{"derivedFrom":sQuery(id+"F6.wireOp",EDGE,"E28.25.0.3")}),-1.0]])]});
            var Q55;
            Q55=makeQuery(id+"F6.imprint","IMPRINT",FACE,{"disambiguationData":[TD([[makeQuery(id+"F6.imprint","IMPRINT",EDGE,{"derivedFrom":sQuery(id+"F6.wireOp",EDGE,"E28.7.0.3")}),-1.0]])]});
            var Q56;
            Q56=makeQuery(id+"F6.imprint","IMPRINT",FACE,{"disambiguationData":[TD([[makeQuery(id+"F6.imprint","IMPRINT",EDGE,{"derivedFrom":sQuery(id+"F6.wireOp",EDGE,"E28.24.0.3")}),-1.0]])]});
            var Q57;
            Q57=makeQuery(id+"F6.imprint","IMPRINT",FACE,{"disambiguationData":[TD([[makeQuery(id+"F6.imprint","IMPRINT",EDGE,{"derivedFrom":sQuery(id+"F6.wireOp",EDGE,"E28.17.0.3")}),-1.0]])]});
            var Q58;
            Q58=makeQuery(id+"F6.imprint","IMPRINT",FACE,{"disambiguationData":[TD([[makeQuery(id+"F6.imprint","IMPRINT",EDGE,{"derivedFrom":sQuery(id+"F6.wireOp",EDGE,"E28.14.0.3")}),-1.0]])]});
            var Q59;
            Q59=makeQuery(id+"F6.imprint","IMPRINT",FACE,{"disambiguationData":[TD([[makeQuery(id+"F6.imprint","IMPRINT",EDGE,{"derivedFrom":sQuery(id+"F6.wireOp",EDGE,"E27.bottom")}),1.0]])]});
            extrude(context, id + "F9", {"entities" : qUnion([Q0, Q1, Q2, Q3, Q4, Q5, Q6, Q7, Q8, Q9, Q10, Q11, Q12, Q13, Q14, Q15, Q16, Q17, Q18, Q19, Q20, Q21, Q22, Q23, Q24, Q25, Q26, Q27, Q28, Q29, Q30, Q31, Q32, Q33, Q34, Q35, Q36, Q37, Q38, Q39, Q40, Q41, Q42, Q43, Q44, Q45, Q46, Q47, Q48, Q49, Q50, Q51, Q52, Q53, Q54, Q55, Q56, Q57, Q58, Q59]), "depth" : 0.25 * mm, "offsetDistance" : 25 * mm});
        }
        {
            var Q0;
            Q0=makeQuery(id+"F1.opExtrude","CAP_FACE",FACE,{"disambiguationData":[OSD([sQuery(id+"F0.wireOp",EDGE,"E0.bottom"),sQuery(id+"F0.wireOp",EDGE,"E0.top"),sQuery(id+"F0.wireOp",EDGE,"E0.left"),sQuery(id+"F0.wireOp",EDGE,"E0.right")])],"isStart":false});
            var sketch = newSketch(context, id + "F10", { "sketchPlane" : qUnion([Q0])});
            skLineSegment(sketch, "E29.bottom", {"start": v(-9.84, -52.87) * mm, "end": v(32.66, -52.87) * mm});
            skLineSegment(sketch, "E29.top", {"start": v(-9.84, -45.37) * mm, "end": v(32.66, -45.37) * mm});
            skLineSegment(sketch, "E29.left", {"start": v(-9.84, -52.87) * mm, "end": v(-9.84, -45.37) * mm});
            skLineSegment(sketch, "E29.right", {"start": v(32.66, -52.87) * mm, "end": v(32.66, -45.37) * mm});
            skLineSegment(sketch, "E30.bottom", {"start": v(33.16, -52.87) * mm, "end": v(73.16, -52.87) * mm});
            skLineSegment(sketch, "E30.top", {"start": v(33.16, -45.37) * mm, "end": v(73.16, -45.37) * mm});
            skLineSegment(sketch, "E30.left", {"start": v(33.16, -52.87) * mm, "end": v(33.16, -45.37) * mm});
            skLineSegment(sketch, "E30.right", {"start": v(73.16, -52.87) * mm, "end": v(73.16, -45.37) * mm});
            skLineSegment(sketch, "E31.bottom", {"start": v(-10.34, -52.87) * mm, "end": v(-22.84, -52.87) * mm});
            skLineSegment(sketch, "E31.top", {"start": v(-10.34, -45.37) * mm, "end": v(-22.84, -45.37) * mm});
            skLineSegment(sketch, "E31.left", {"start": v(-10.34, -52.87) * mm, "end": v(-10.34, -45.37) * mm});
            skLineSegment(sketch, "E31.right", {"start": v(-22.84, -52.87) * mm, "end": v(-22.84, -45.37) * mm});
            skSolve(sketch);
        }
        {
            var Q0;
            Q0=makeQuery(id+"F10.imprint","IMPRINT",FACE,{"disambiguationData":[TD([[makeQuery(id+"F10.imprint","IMPRINT",EDGE,{"derivedFrom":sQuery(id+"F10.wireOp",EDGE,"E31.bottom")}),-1.0]])]});
            var Q1;
            Q1=makeQuery(id+"F10.imprint","IMPRINT",FACE,{"disambiguationData":[TD([[makeQuery(id+"F10.imprint","IMPRINT",EDGE,{"derivedFrom":sQuery(id+"F10.wireOp",EDGE,"E29.bottom")}),1.0]])]});
            var Q2;
            Q2=makeQuery(id+"F10.imprint","IMPRINT",FACE,{"disambiguationData":[TD([[makeQuery(id+"F10.imprint","IMPRINT",EDGE,{"derivedFrom":sQuery(id+"F10.wireOp",EDGE,"E30.bottom")}),1.0]])]});
            extrude(context, id + "F11", {"entities" : qUnion([Q0, Q1, Q2]), "depth" : 6 * mm, "offsetDistance" : 25 * mm});
        }
        {
            var Q0;
            Q0=makeQuery(id+"F1.opExtrude","CAP_FACE",FACE,{"disambiguationData":[OSD([sQuery(id+"F0.wireOp",EDGE,"E0.bottom"),sQuery(id+"F0.wireOp",EDGE,"E0.top"),sQuery(id+"F0.wireOp",EDGE,"E0.left"),sQuery(id+"F0.wireOp",EDGE,"E0.right")])],"isStart":false});
            var sketch = newSketch(context, id + "F12", { "sketchPlane" : qUnion([Q0])});
            skLineSegment(sketch, "E32.bottom", {"start": v(-28.84, 99.13) * mm, "end": v(-16.84, 99.13) * mm});
            skLineSegment(sketch, "E32.top", {"start": v(-28.84, 87.13) * mm, "end": v(-16.84, 87.13) * mm});
            skLineSegment(sketch, "E32.left", {"start": v(-28.84, 99.13) * mm, "end": v(-28.84, 87.13) * mm});
            skLineSegment(sketch, "E32.right", {"start": v(-16.84, 99.13) * mm, "end": v(-16.84, 87.13) * mm});
            skLineSegment(sketch, "E33.0.1.0", {"start": v(-28.84, 62.13) * mm, "end": v(-16.84, 62.13) * mm});
            skLineSegment(sketch, "E33.0.1.1", {"start": v(-28.84, 74.13) * mm, "end": v(-16.84, 74.13) * mm});
            skLineSegment(sketch, "E33.0.1.2", {"start": v(-16.84, 74.13) * mm, "end": v(-16.84, 62.13) * mm});
            skLineSegment(sketch, "E33.0.1.3", {"start": v(-28.84, 74.13) * mm, "end": v(-28.84, 62.13) * mm});
            skLineSegment(sketch, "E33.0.2.0", {"start": v(-28.84, 37.13) * mm, "end": v(-16.84, 37.13) * mm});
            skLineSegment(sketch, "E33.0.2.1", {"start": v(-28.84, 49.13) * mm, "end": v(-16.84, 49.13) * mm});
            skLineSegment(sketch, "E33.0.2.2", {"start": v(-16.84, 49.13) * mm, "end": v(-16.84, 37.13) * mm});
            skLineSegment(sketch, "E33.0.2.3", {"start": v(-28.84, 49.13) * mm, "end": v(-28.84, 37.13) * mm});
            skLineSegment(sketch, "E33.1.0.0", {"start": v(67.16, 87.13) * mm, "end": v(79.16, 87.13) * mm});
            skLineSegment(sketch, "E33.1.0.1", {"start": v(67.16, 99.13) * mm, "end": v(79.16, 99.13) * mm});
            skLineSegment(sketch, "E33.1.0.2", {"start": v(79.16, 99.13) * mm, "end": v(79.16, 87.13) * mm});
            skLineSegment(sketch, "E33.1.0.3", {"start": v(67.16, 99.13) * mm, "end": v(67.16, 87.13) * mm});
            skLineSegment(sketch, "E33.1.1.0", {"start": v(67.16, 62.13) * mm, "end": v(79.16, 62.13) * mm});
            skLineSegment(sketch, "E33.1.1.1", {"start": v(67.16, 74.13) * mm, "end": v(79.16, 74.13) * mm});
            skLineSegment(sketch, "E33.1.1.2", {"start": v(79.16, 74.13) * mm, "end": v(79.16, 62.13) * mm});
            skLineSegment(sketch, "E33.1.1.3", {"start": v(67.16, 74.13) * mm, "end": v(67.16, 62.13) * mm});
            skLineSegment(sketch, "E33.1.2.0", {"start": v(67.16, 37.13) * mm, "end": v(79.16, 37.13) * mm});
            skLineSegment(sketch, "E33.1.2.1", {"start": v(67.16, 49.13) * mm, "end": v(79.16, 49.13) * mm});
            skLineSegment(sketch, "E33.1.2.2", {"start": v(79.16, 49.13) * mm, "end": v(79.16, 37.13) * mm});
            skLineSegment(sketch, "E33.1.2.3", {"start": v(67.16, 49.13) * mm, "end": v(67.16, 37.13) * mm});
            skLineSegment(sketch, "E33.direction1", {"start": v(-28.84, 87.13) * mm, "end": v(67.16, 87.13) * mm, "construction": true});
            skLineSegment(sketch, "E33.direction2", {"start": v(-28.84, 87.13) * mm, "end": v(-28.84, 62.13) * mm, "construction": true});
            skCircle(sketch, "E34", {"center": v(-22.84, 93.13) * mm, "radius": 2 * mm});
            skPoint(sketch, "E34.centerSnap0", {"position": v(-22.84, 99.13) * mm});
            skPoint(sketch, "E34.centerSnap1", {"position": v(-28.84, 93.13) * mm});
            skCircle(sketch, "E35.0.1.0", {"center": v(-22.84, 68.13) * mm, "radius": 2 * mm});
            skPoint(sketch, "E35.0.1.1", {"position": v(-22.84, 74.13) * mm});
            skCircle(sketch, "E35.0.2.0", {"center": v(-22.84, 43.13) * mm, "radius": 2 * mm});
            skPoint(sketch, "E35.0.2.1", {"position": v(-22.84, 49.13) * mm});
            skCircle(sketch, "E35.1.0.0", {"center": v(73.16, 93.13) * mm, "radius": 2 * mm});
            skPoint(sketch, "E35.1.0.1", {"position": v(73.16, 99.13) * mm});
            skCircle(sketch, "E35.1.1.0", {"center": v(73.16, 68.13) * mm, "radius": 2 * mm});
            skPoint(sketch, "E35.1.1.1", {"position": v(73.16, 74.13) * mm});
            skCircle(sketch, "E35.1.2.0", {"center": v(73.16, 43.13) * mm, "radius": 2 * mm});
            skPoint(sketch, "E35.1.2.1", {"position": v(73.16, 49.13) * mm});
            skLineSegment(sketch, "E35.direction1", {"start": v(-22.84, 93.13) * mm, "end": v(73.16, 93.13) * mm, "construction": true});
            skLineSegment(sketch, "E35.direction2", {"start": v(-22.84, 93.13) * mm, "end": v(-22.84, 68.13) * mm, "construction": true});
            skSolve(sketch);
        }
        {
            var Q0;
            Q0=makeQuery(id+"F12.imprint","IMPRINT",FACE,{"disambiguationData":[TD([[makeQuery(id+"F12.imprint","IMPRINT",EDGE,{"derivedFrom":sQuery(id+"F12.wireOp",EDGE,"E32.bottom")}),-1.0]])]});
            var Q1;
            Q1=makeQuery(id+"F12.imprint","IMPRINT",FACE,{"disambiguationData":[TD([[makeQuery(id+"F12.imprint","IMPRINT",EDGE,{"derivedFrom":sQuery(id+"F12.wireOp",EDGE,"E33.1.0.0")}),1.0]])]});
            var Q2;
            Q2=makeQuery(id+"F12.imprint","IMPRINT",FACE,{"disambiguationData":[TD([[makeQuery(id+"F12.imprint","IMPRINT",EDGE,{"derivedFrom":sQuery(id+"F12.wireOp",EDGE,"E33.1.1.0")}),1.0]])]});
            var Q3;
            Q3=makeQuery(id+"F12.imprint","IMPRINT",FACE,{"disambiguationData":[TD([[makeQuery(id+"F12.imprint","IMPRINT",EDGE,{"derivedFrom":sQuery(id+"F12.wireOp",EDGE,"E33.0.1.0")}),1.0]])]});
            var Q4;
            Q4=makeQuery(id+"F12.imprint","IMPRINT",FACE,{"disambiguationData":[TD([[makeQuery(id+"F12.imprint","IMPRINT",EDGE,{"derivedFrom":sQuery(id+"F12.wireOp",EDGE,"E33.0.2.0")}),1.0]])]});
            var Q5;
            Q5=makeQuery(id+"F12.imprint","IMPRINT",FACE,{"disambiguationData":[TD([[makeQuery(id+"F12.imprint","IMPRINT",EDGE,{"derivedFrom":sQuery(id+"F12.wireOp",EDGE,"E33.1.2.0")}),1.0]])]});
            extrude(context, id + "F13", {"entities" : qUnion([Q0, Q1, Q2, Q3, Q4, Q5]), "depth" : 6.5 * mm, "offsetDistance" : 25 * mm});
        }
        {
            var Q0;
            Q0=makeQuery(id+"F13.opExtrude","SWEPT_FACE",FACE,{"disambiguationData":[OSD([sQuery(id+"F12.wireOp",EDGE,"E33.1.2.2")])]});
            var sketch = newSketch(context, id + "F14", { "sketchPlane" : qUnion([Q0])});
            skLineSegment(sketch, "E36.bottom", {"start": v(38.63, 2) * mm, "end": v(47.63, 2) * mm});
            skLineSegment(sketch, "E36.top", {"start": v(38.63, 7) * mm, "end": v(47.63, 7) * mm});
            skLineSegment(sketch, "E36.left", {"start": v(38.63, 2) * mm, "end": v(38.63, 7) * mm});
            skLineSegment(sketch, "E36.right", {"start": v(47.63, 2) * mm, "end": v(47.63, 7) * mm});
            skLineSegment(sketch, "E37.1.0.0", {"start": v(63.63, 2) * mm, "end": v(63.63, 7) * mm});
            skLineSegment(sketch, "E37.1.0.1", {"start": v(72.63, 2) * mm, "end": v(72.63, 7) * mm});
            skLineSegment(sketch, "E37.1.0.2", {"start": v(63.63, 7) * mm, "end": v(72.63, 7) * mm});
            skLineSegment(sketch, "E37.1.0.3", {"start": v(63.63, 2) * mm, "end": v(72.63, 2) * mm});
            skLineSegment(sketch, "E37.2.0.0", {"start": v(88.63, 2) * mm, "end": v(88.63, 7) * mm});
            skLineSegment(sketch, "E37.2.0.1", {"start": v(97.63, 2) * mm, "end": v(97.63, 7) * mm});
            skLineSegment(sketch, "E37.2.0.2", {"start": v(88.63, 7) * mm, "end": v(97.63, 7) * mm});
            skLineSegment(sketch, "E37.2.0.3", {"start": v(88.63, 2) * mm, "end": v(97.63, 2) * mm});
            skLineSegment(sketch, "E37.direction1", {"start": v(38.63, 2) * mm, "end": v(63.63, 2) * mm, "construction": true});
            skSolve(sketch);
        }
        {
            var Q0;
            Q0 = qSketchRegion(id + "F14", true);
            extrude(context, id + "F15", {"entities" : qUnion([Q0]), "operationType" : NewBodyOperationType.REMOVE, "endBound" : BoundingType.THROUGH_ALL, "oppositeDirection" : true, "depth" : 25 * mm, "offsetDistance" : 25 * mm});
        }
        {
            var Q0;
            Q0=makeQuery(id+"F13.opExtrude","CAP_EDGE",EDGE,{"disambiguationData":[OSD([sQuery(id+"F12.wireOp",EDGE,"E33.0.2.0")])],"isStart":false});
            var Q1;
            Q1=makeQuery(id+"F13.opExtrude","CAP_EDGE",EDGE,{"disambiguationData":[OSD([sQuery(id+"F12.wireOp",EDGE,"E33.0.2.1")])],"isStart":false});
            var Q2;
            Q2=makeQuery(id+"F13.opExtrude","CAP_EDGE",EDGE,{"disambiguationData":[OSD([sQuery(id+"F12.wireOp",EDGE,"E33.0.1.0")])],"isStart":false});
            var Q3;
            Q3=makeQuery(id+"F13.opExtrude","CAP_EDGE",EDGE,{"disambiguationData":[OSD([sQuery(id+"F12.wireOp",EDGE,"E33.0.1.1")])],"isStart":false});
            var Q4;
            Q4=makeQuery(id+"F13.opExtrude","CAP_EDGE",EDGE,{"disambiguationData":[OSD([sQuery(id+"F12.wireOp",EDGE,"E32.top")])],"isStart":false});
            var Q5;
            Q5=makeQuery(id+"F13.opExtrude","CAP_EDGE",EDGE,{"disambiguationData":[OSD([sQuery(id+"F12.wireOp",EDGE,"E32.bottom")])],"isStart":false});
            var Q6;
            Q6=makeQuery(id+"F13.opExtrude","CAP_EDGE",EDGE,{"disambiguationData":[OSD([sQuery(id+"F12.wireOp",EDGE,"E33.1.2.0")])],"isStart":false});
            var Q7;
            Q7=makeQuery(id+"F13.opExtrude","CAP_EDGE",EDGE,{"disambiguationData":[OSD([sQuery(id+"F12.wireOp",EDGE,"E33.1.2.1")])],"isStart":false});
            var Q8;
            Q8=makeQuery(id+"F13.opExtrude","CAP_EDGE",EDGE,{"disambiguationData":[OSD([sQuery(id+"F12.wireOp",EDGE,"E33.1.1.0")])],"isStart":false});
            var Q9;
            Q9=makeQuery(id+"F13.opExtrude","CAP_EDGE",EDGE,{"disambiguationData":[OSD([sQuery(id+"F12.wireOp",EDGE,"E33.1.0.0")])],"isStart":false});
            var Q10;
            Q10=makeQuery(id+"F13.opExtrude","CAP_EDGE",EDGE,{"disambiguationData":[OSD([sQuery(id+"F12.wireOp",EDGE,"E33.1.1.1")])],"isStart":false});
            var Q11;
            Q11=makeQuery(id+"F13.opExtrude","CAP_EDGE",EDGE,{"disambiguationData":[OSD([sQuery(id+"F12.wireOp",EDGE,"E33.1.0.1")])],"isStart":false});
            fillet(context, id + "F16", {"entities" : qUnion([Q0, Q1, Q2, Q3, Q4, Q5, Q6, Q7, Q8, Q9, Q10, Q11]), "tangentPropagation" : true, "radius" : 1 * mm, "defaultsChanged" : true, "vertexSettings" : [], "allowEdgeOverflow" : false});
        }
        {
            var Q0;
            Q0=makeQuery(id+"F1.opExtrude","CAP_FACE",FACE,{"disambiguationData":[OSD([sQuery(id+"F0.wireOp",EDGE,"E0.bottom"),sQuery(id+"F0.wireOp",EDGE,"E0.top"),sQuery(id+"F0.wireOp",EDGE,"E0.left"),sQuery(id+"F0.wireOp",EDGE,"E0.right")])],"isStart":false});
            var sketch = newSketch(context, id + "F17", { "sketchPlane" : qUnion([Q0])});
            skCircle(sketch, "E38", {"center": v(10.16, 114.63) * mm, "radius": 2 * mm});
            skCircle(sketch, "E39.1.0.0", {"center": v(18.16, 114.63) * mm, "radius": 2 * mm});
            skCircle(sketch, "E39.2.0.0", {"center": v(26.16, 114.63) * mm, "radius": 2 * mm});
            skLineSegment(sketch, "E39.direction1", {"start": v(-4.84, 114.13) * mm, "end": v(3.16, 114.13) * mm, "construction": true});
            skLineSegment(sketch, "E40.bottom", {"start": v(6.16, 119.13) * mm, "end": v(30.16, 119.13) * mm});
            skLineSegment(sketch, "E40.top", {"start": v(6.16, 110.13) * mm, "end": v(30.16, 110.13) * mm});
            skLineSegment(sketch, "E40.left", {"start": v(6.16, 119.13) * mm, "end": v(6.16, 110.13) * mm});
            skLineSegment(sketch, "E40.right", {"start": v(30.16, 119.13) * mm, "end": v(30.16, 110.13) * mm});
            skSolve(sketch);
        }
        {
            var Q0;
            Q0=makeQuery(id+"F17.imprint","IMPRINT",FACE,{"disambiguationData":[TD([[makeQuery(id+"F17.imprint","IMPRINT",EDGE,{"derivedFrom":sQuery(id+"F17.wireOp",EDGE,"E38")}),-1.0]])]});
            extrude(context, id + "F18", {"entities" : qUnion([Q0]), "depth" : 0.1 * mm, "offsetDistance" : 25 * mm});
        }
        {
            var Q0;
            Q0=sQuery(id+"F17.wireOp",VERTEX,"E38.center");
            var Q1;
            Q1=sQuery(id+"F17.wireOp",VERTEX,"E39.1.0.0.center");
            var Q2;
            Q2=sQuery(id+"F17.wireOp",VERTEX,"E39.2.0.0.center");
            var Q3;
            Q3=makeQuery(id+"F1.opExtrude","SWEPT_BODY",BODY,{"disambiguationData":[OSD([sQuery(id+"F0.wireOp",EDGE,"E0.bottom"),sQuery(id+"F0.wireOp",EDGE,"E0.top"),sQuery(id+"F0.wireOp",EDGE,"E0.left"),sQuery(id+"F0.wireOp",EDGE,"E0.right")])]});
            var Q4;
            Q4=makeQuery(id+"F18.opExtrude","SWEPT_BODY",BODY,{"disambiguationData":[OSD([sQuery(id+"F17.wireOp",EDGE,"E38"),sQuery(id+"F17.wireOp",EDGE,"E39.1.0.0"),sQuery(id+"F17.wireOp",EDGE,"E39.2.0.0"),sQuery(id+"F17.wireOp",EDGE,"E40.bottom"),sQuery(id+"F17.wireOp",EDGE,"E40.top"),sQuery(id+"F17.wireOp",EDGE,"E40.left"),sQuery(id+"F17.wireOp",EDGE,"E40.right")])]});
            hole(context, id + "F19", {"style" : HoleStyle.SIMPLE, "endStyle" : HoleEndStyle.THROUGH, "standardTappedOrClearance" : lookupTablePath({ "fit" : "Normal", "standard" : "ISO", "size" : "M4", "type" : "Clearance" }), "standardBlindInLast" : lookupTablePath({ "fit" : "Normal", "standard" : "ISO", "engagement" : "75%", "pitch" : "0.7 mm", "size" : "M4", "type" : "Clearance & tapped" }), "holeDiameter" : 4.5 * mm, "majorDiameter" : 5 * mm, "isTappedThrough" : true, "tappedDepth" : 12 * mm, "tapClearance" : 3, "locations" : qUnion([Q0, Q1, Q2]), "scope" : qUnion([Q3, Q4])});
        }
        {
            var Q0;
            Q0=makeQuery(id+"F11.opExtrude","SWEPT_FACE",FACE,{"disambiguationData":[OSD([sQuery(id+"F10.wireOp",EDGE,"E31.bottom")])]});
            var sketch = newSketch(context, id + "F20", { "sketchPlane" : qUnion([Q0])});
            skCircle(sketch, "E41", {"center": v(-20.34, 5.4) * mm, "radius": 0.5 * mm});
            skLineSegment(sketch, "E42.bottom", {"start": v(-22.34, 7.5) * mm, "end": v(-10.84, 7.5) * mm});
            skLineSegment(sketch, "E42.top", {"start": v(-22.34, 2.5) * mm, "end": v(-10.84, 2.5) * mm});
            skLineSegment(sketch, "E42.left", {"start": v(-22.34, 7.5) * mm, "end": v(-22.34, 2.5) * mm});
            skLineSegment(sketch, "E42.right", {"start": v(-10.84, 7.5) * mm, "end": v(-10.84, 2.5) * mm});
            skCircle(sketch, "E43.1.0.0", {"center": v(-17.84, 5.4) * mm, "radius": 0.5 * mm});
            skCircle(sketch, "E43.2.0.0", {"center": v(-15.34, 5.4) * mm, "radius": 0.5 * mm});
            skCircle(sketch, "E43.3.0.0", {"center": v(-12.84, 5.4) * mm, "radius": 0.5 * mm});
            skLineSegment(sketch, "E43.direction1", {"start": v(-20.34, 5.4) * mm, "end": v(-17.84, 5.4) * mm, "construction": true});
            skLineSegment(sketch, "E44.bottom", {"start": v(-9.34, 7.5) * mm, "end": v(32.16, 7.5) * mm});
            skLineSegment(sketch, "E44.top", {"start": v(-9.34, 2.5) * mm, "end": v(32.16, 2.5) * mm});
            skLineSegment(sketch, "E44.left", {"start": v(-9.34, 7.5) * mm, "end": v(-9.34, 2.5) * mm});
            skLineSegment(sketch, "E44.right", {"start": v(32.16, 7.5) * mm, "end": v(32.16, 2.5) * mm});
            skLineSegment(sketch, "E45.bottom", {"start": v(33.66, 7.5) * mm, "end": v(72.66, 7.5) * mm});
            skLineSegment(sketch, "E45.top", {"start": v(33.66, 2.5) * mm, "end": v(72.66, 2.5) * mm});
            skLineSegment(sketch, "E45.left", {"start": v(33.66, 7.5) * mm, "end": v(33.66, 2.5) * mm});
            skLineSegment(sketch, "E45.right", {"start": v(72.66, 7.5) * mm, "end": v(72.66, 2.5) * mm});
            skCircle(sketch, "E46", {"center": v(-7.34, 5.4) * mm, "radius": 0.5 * mm});
            skCircle(sketch, "E47.1.0.0", {"center": v(-4.84, 5.4) * mm, "radius": 0.5 * mm});
            skCircle(sketch, "E47.2.0.0", {"center": v(-2.34, 5.4) * mm, "radius": 0.5 * mm});
            skCircle(sketch, "E47.3.0.0", {"center": v(0.16, 5.4) * mm, "radius": 0.5 * mm});
            skCircle(sketch, "E47.4.0.0", {"center": v(2.66, 5.4) * mm, "radius": 0.5 * mm});
            skCircle(sketch, "E47.5.0.0", {"center": v(5.16, 5.4) * mm, "radius": 0.5 * mm});
            skCircle(sketch, "E47.6.0.0", {"center": v(7.66, 5.4) * mm, "radius": 0.5 * mm});
            skCircle(sketch, "E47.7.0.0", {"center": v(10.16, 5.4) * mm, "radius": 0.5 * mm});
            skCircle(sketch, "E47.8.0.0", {"center": v(12.66, 5.4) * mm, "radius": 0.5 * mm});
            skCircle(sketch, "E47.9.0.0", {"center": v(15.16, 5.4) * mm, "radius": 0.5 * mm});
            skCircle(sketch, "E47.10.0.0", {"center": v(17.66, 5.4) * mm, "radius": 0.5 * mm});
            skCircle(sketch, "E47.11.0.0", {"center": v(20.16, 5.4) * mm, "radius": 0.5 * mm});
            skCircle(sketch, "E47.12.0.0", {"center": v(22.66, 5.4) * mm, "radius": 0.5 * mm});
            skCircle(sketch, "E47.13.0.0", {"center": v(25.16, 5.4) * mm, "radius": 0.5 * mm});
            skCircle(sketch, "E47.14.0.0", {"center": v(27.66, 5.4) * mm, "radius": 0.5 * mm});
            skCircle(sketch, "E47.15.0.0", {"center": v(30.16, 5.4) * mm, "radius": 0.5 * mm});
            skLineSegment(sketch, "E47.direction1", {"start": v(-7.34, 5.4) * mm, "end": v(-4.84, 5.4) * mm, "construction": true});
            skCircle(sketch, "E48", {"center": v(35.66, 5.4) * mm, "radius": 0.5 * mm});
            skCircle(sketch, "E49.1.0.0", {"center": v(38.16, 5.4) * mm, "radius": 0.5 * mm});
            skCircle(sketch, "E49.2.0.0", {"center": v(40.66, 5.4) * mm, "radius": 0.5 * mm});
            skCircle(sketch, "E49.3.0.0", {"center": v(43.16, 5.4) * mm, "radius": 0.5 * mm});
            skCircle(sketch, "E49.4.0.0", {"center": v(45.66, 5.4) * mm, "radius": 0.5 * mm});
            skCircle(sketch, "E49.5.0.0", {"center": v(48.16, 5.4) * mm, "radius": 0.5 * mm});
            skCircle(sketch, "E49.6.0.0", {"center": v(50.66, 5.4) * mm, "radius": 0.5 * mm});
            skCircle(sketch, "E49.7.0.0", {"center": v(53.16, 5.4) * mm, "radius": 0.5 * mm});
            skCircle(sketch, "E49.8.0.0", {"center": v(55.66, 5.4) * mm, "radius": 0.5 * mm});
            skCircle(sketch, "E49.9.0.0", {"center": v(58.16, 5.4) * mm, "radius": 0.5 * mm});
            skCircle(sketch, "E49.10.0.0", {"center": v(60.66, 5.4) * mm, "radius": 0.5 * mm});
            skCircle(sketch, "E49.11.0.0", {"center": v(63.16, 5.4) * mm, "radius": 0.5 * mm});
            skCircle(sketch, "E49.12.0.0", {"center": v(65.66, 5.4) * mm, "radius": 0.5 * mm});
            skCircle(sketch, "E49.13.0.0", {"center": v(68.16, 5.4) * mm, "radius": 0.5 * mm});
            skCircle(sketch, "E49.14.0.0", {"center": v(70.66, 5.4) * mm, "radius": 0.5 * mm});
            skLineSegment(sketch, "E49.direction1", {"start": v(35.66, 5.4) * mm, "end": v(38.16, 5.4) * mm, "construction": true});
            skSolve(sketch);
        }
        {
            var Q0;
            Q0=makeQuery(id+"F20.imprint","IMPRINT",FACE,{"disambiguationData":[TD([[makeQuery(id+"F20.imprint","IMPRINT",EDGE,{"derivedFrom":sQuery(id+"F20.wireOp",EDGE,"E45.bottom")}),-1.0]])]});
            var Q1;
            Q1=makeQuery(id+"F20.imprint","IMPRINT",FACE,{"disambiguationData":[TD([[makeQuery(id+"F20.imprint","IMPRINT",EDGE,{"derivedFrom":sQuery(id+"F20.wireOp",EDGE,"E44.bottom")}),-1.0]])]});
            var Q2;
            Q2=makeQuery(id+"F20.imprint","IMPRINT",FACE,{"disambiguationData":[TD([[makeQuery(id+"F20.imprint","IMPRINT",EDGE,{"derivedFrom":sQuery(id+"F20.wireOp",EDGE,"E41")}),-1.0]])]});
            extrude(context, id + "F21", {"entities" : qUnion([Q0, Q1, Q2]), "operationType" : NewBodyOperationType.REMOVE, "oppositeDirection" : true, "depth" : 5 * mm, "offsetDistance" : 25 * mm});
        }
    });
